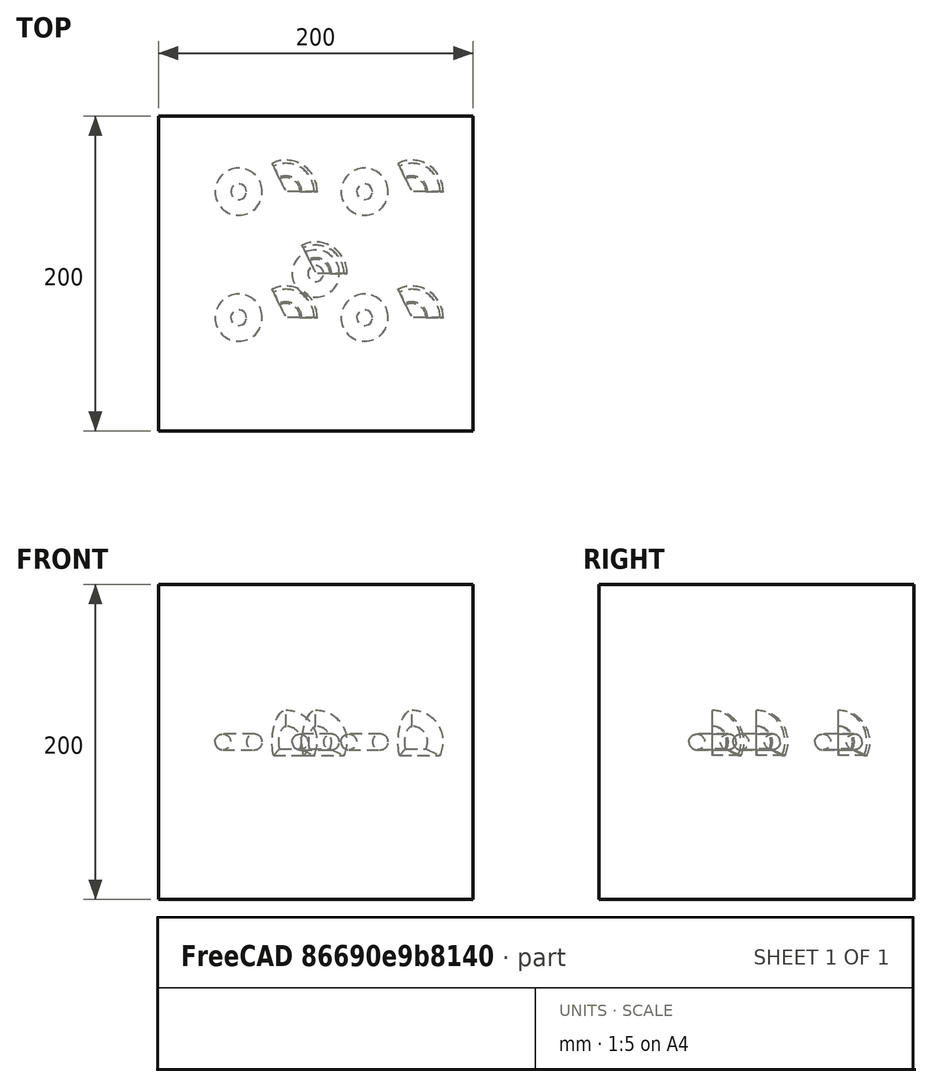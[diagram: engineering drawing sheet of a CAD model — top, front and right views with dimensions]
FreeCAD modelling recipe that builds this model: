
FCSTD DOCUMENT  (FreeCAD 0.19RUnknown)
Label: arrayTest-5
License: All rights reserved
LicenseURL: http://en.wikipedia.org/wiki/All_rights_reserved
objects: App::DocumentObjectGroupPython×1248, App::Part×5, Part::FeaturePython×4
note: 4 computed .brp shape members not serialized (recipe doc carries the construction recipe); baked Part::Feature solids carry a one-line shape summary decoded from their .brp

FEATURE [App::DocumentObjectGroupPython] HALFPI  # scripted group (container) (typed FeaturePython)
  name = HALFPI
  value = pi/2.
FEATURE [App::DocumentObjectGroupPython] PI  # scripted group (container) (typed FeaturePython)
  name = PI
  value = 1.*pi
FEATURE [App::DocumentObjectGroupPython] TWOPI  # scripted group (container) (typed FeaturePython)
  name = TWOPI
  value = 2.*pi
FEATURE [App::DocumentObjectGroupPython] Constants  # scripted group (container) (typed FeaturePython)
  Group = -> [HALFPI,PI,TWOPI]
FEATURE [App::DocumentObjectGroupPython] Variables  # scripted group (container) (typed FeaturePython)
FEATURE [App::DocumentObjectGroupPython] Quantities  # scripted group (container) (typed FeaturePython)
FEATURE [App::DocumentObjectGroupPython] Isotopes  # scripted group (container) (typed FeaturePython)
FEATURE [App::DocumentObjectGroupPython] Elements  # scripted group (container) (typed FeaturePython)
FEATURE [App::DocumentObjectGroupPython] G4Isotopes  # scripted group (container) (typed FeaturePython)
FEATURE [App::DocumentObjectGroupPython] H_element  # scripted group (container) (typed FeaturePython)
  Z = 1
  atom_value = 1.008
  formula = H
  name = H_element
FEATURE [App::DocumentObjectGroupPython] He_element  # scripted group (container) (typed FeaturePython)
  Z = 2
  atom_value = 4.0026
  formula = He
  name = He_element
FEATURE [App::DocumentObjectGroupPython] Li_element  # scripted group (container) (typed FeaturePython)
  Z = 3
  atom_value = 6.94
  formula = Li
  name = Li_element
FEATURE [App::DocumentObjectGroupPython] Be_element  # scripted group (container) (typed FeaturePython)
  Z = 4
  atom_value = 9.01218
  formula = Be
  name = Be_element
FEATURE [App::DocumentObjectGroupPython] B_element  # scripted group (container) (typed FeaturePython)
  Z = 5
  atom_value = 10.81
  formula = B
  name = B_element
FEATURE [App::DocumentObjectGroupPython] C_element  # scripted group (container) (typed FeaturePython)
  Z = 6
  atom_value = 12.011
  formula = C
  name = C_element
FEATURE [App::DocumentObjectGroupPython] N_element  # scripted group (container) (typed FeaturePython)
  Z = 7
  atom_value = 14.007
  formula = N
  name = N_element
FEATURE [App::DocumentObjectGroupPython] O_element  # scripted group (container) (typed FeaturePython)
  Z = 8
  atom_value = 15.999
  formula = O
  name = O_element
FEATURE [App::DocumentObjectGroupPython] F_element  # scripted group (container) (typed FeaturePython)
  Z = 9
  atom_value = 18.9984
  formula = F
  name = F_element
FEATURE [App::DocumentObjectGroupPython] Ne_element  # scripted group (container) (typed FeaturePython)
  Z = 10
  atom_value = 20.1797
  formula = Ne
  name = Ne_element
FEATURE [App::DocumentObjectGroupPython] Na_element  # scripted group (container) (typed FeaturePython)
  Z = 11
  atom_value = 22.9898
  formula = Na
  name = Na_element
FEATURE [App::DocumentObjectGroupPython] Mg_element  # scripted group (container) (typed FeaturePython)
  Z = 12
  atom_value = 24.305
  formula = Mg
  name = Mg_element
FEATURE [App::DocumentObjectGroupPython] Al_element  # scripted group (container) (typed FeaturePython)
  Z = 13
  atom_value = 26.9815
  formula = Al
  name = Al_element
FEATURE [App::DocumentObjectGroupPython] Si_element  # scripted group (container) (typed FeaturePython)
  Z = 14
  atom_value = 28.085
  formula = Si
  name = Si_element
FEATURE [App::DocumentObjectGroupPython] P_element  # scripted group (container) (typed FeaturePython)
  Z = 15
  atom_value = 30.9738
  formula = P
  name = P_element
FEATURE [App::DocumentObjectGroupPython] S_element  # scripted group (container) (typed FeaturePython)
  Z = 16
  atom_value = 32.06
  formula = S
  name = S_element
FEATURE [App::DocumentObjectGroupPython] Cl_element  # scripted group (container) (typed FeaturePython)
  Z = 17
  atom_value = 35.45
  formula = Cl
  name = Cl_element
FEATURE [App::DocumentObjectGroupPython] Ar_element  # scripted group (container) (typed FeaturePython)
  Z = 18
  atom_value = 39.95
  formula = Ar
  name = Ar_element
FEATURE [App::DocumentObjectGroupPython] K_element  # scripted group (container) (typed FeaturePython)
  Z = 19
  atom_value = 39.0983
  formula = K
  name = K_element
FEATURE [App::DocumentObjectGroupPython] Ca_element  # scripted group (container) (typed FeaturePython)
  Z = 20
  atom_value = 40.078
  formula = Ca
  name = Ca_element
FEATURE [App::DocumentObjectGroupPython] Sc_element  # scripted group (container) (typed FeaturePython)
  Z = 21
  atom_value = 44.9559
  formula = Sc
  name = Sc_element
FEATURE [App::DocumentObjectGroupPython] Ti_element  # scripted group (container) (typed FeaturePython)
  Z = 22
  atom_value = 47.867
  formula = Ti
  name = Ti_element
FEATURE [App::DocumentObjectGroupPython] V_element  # scripted group (container) (typed FeaturePython)
  Z = 23
  atom_value = 50.9415
  formula = V
  name = V_element
FEATURE [App::DocumentObjectGroupPython] Cr_element  # scripted group (container) (typed FeaturePython)
  Z = 24
  atom_value = 51.9961
  formula = Cr
  name = Cr_element
FEATURE [App::DocumentObjectGroupPython] Mn_element  # scripted group (container) (typed FeaturePython)
  Z = 25
  atom_value = 54.938
  formula = Mn
  name = Mn_element
FEATURE [App::DocumentObjectGroupPython] Fe_element  # scripted group (container) (typed FeaturePython)
  Z = 26
  atom_value = 55.845
  formula = Fe
  name = Fe_element
FEATURE [App::DocumentObjectGroupPython] Co_element  # scripted group (container) (typed FeaturePython)
  Z = 27
  atom_value = 58.9332
  formula = Co
  name = Co_element
FEATURE [App::DocumentObjectGroupPython] Ni_element  # scripted group (container) (typed FeaturePython)
  Z = 28
  atom_value = 58.6934
  formula = Ni
  name = Ni_element
FEATURE [App::DocumentObjectGroupPython] Cu_element  # scripted group (container) (typed FeaturePython)
  Z = 29
  atom_value = 63.546
  formula = Cu
  name = Cu_element
FEATURE [App::DocumentObjectGroupPython] Zn_element  # scripted group (container) (typed FeaturePython)
  Z = 30
  atom_value = 65.38
  formula = Zn
  name = Zn_element
FEATURE [App::DocumentObjectGroupPython] Ga_element  # scripted group (container) (typed FeaturePython)
  Z = 31
  atom_value = 69.723
  formula = Ga
  name = Ga_element
FEATURE [App::DocumentObjectGroupPython] Ge_element  # scripted group (container) (typed FeaturePython)
  Z = 32
  atom_value = 72.63
  formula = Ge
  name = Ge_element
FEATURE [App::DocumentObjectGroupPython] As_element  # scripted group (container) (typed FeaturePython)
  Z = 33
  atom_value = 74.9216
  formula = As
  name = As_element
FEATURE [App::DocumentObjectGroupPython] Se_element  # scripted group (container) (typed FeaturePython)
  Z = 34
  atom_value = 78.971
  formula = Se
  name = Se_element
FEATURE [App::DocumentObjectGroupPython] Br_element  # scripted group (container) (typed FeaturePython)
  Z = 35
  atom_value = 79.904
  formula = Br
  name = Br_element
FEATURE [App::DocumentObjectGroupPython] Kr_element  # scripted group (container) (typed FeaturePython)
  Z = 36
  atom_value = 83.798
  formula = Kr
  name = Kr_element
FEATURE [App::DocumentObjectGroupPython] Rb_element  # scripted group (container) (typed FeaturePython)
  Z = 37
  atom_value = 85.4678
  formula = Rb
  name = Rb_element
FEATURE [App::DocumentObjectGroupPython] Sr_element  # scripted group (container) (typed FeaturePython)
  Z = 38
  atom_value = 87.62
  formula = Sr
  name = Sr_element
FEATURE [App::DocumentObjectGroupPython] Y_element  # scripted group (container) (typed FeaturePython)
  Z = 39
  atom_value = 88.9058
  formula = Y
  name = Y_element
FEATURE [App::DocumentObjectGroupPython] Zr_element  # scripted group (container) (typed FeaturePython)
  Z = 40
  atom_value = 91.224
  formula = Zr
  name = Zr_element
FEATURE [App::DocumentObjectGroupPython] Nb_element  # scripted group (container) (typed FeaturePython)
  Z = 41
  atom_value = 92.9064
  formula = Nb
  name = Nb_element
FEATURE [App::DocumentObjectGroupPython] Mo_element  # scripted group (container) (typed FeaturePython)
  Z = 42
  atom_value = 95.95
  formula = Mo
  name = Mo_element
FEATURE [App::DocumentObjectGroupPython] Tc_element  # scripted group (container) (typed FeaturePython)
  Z = 43
  atom_value = 97
  formula = Tc
  name = Tc_element
FEATURE [App::DocumentObjectGroupPython] Ru_element  # scripted group (container) (typed FeaturePython)
  Z = 44
  atom_value = 101.07
  formula = Ru
  name = Ru_element
FEATURE [App::DocumentObjectGroupPython] Rh_element  # scripted group (container) (typed FeaturePython)
  Z = 45
  atom_value = 102.905
  formula = Rh
  name = Rh_element
FEATURE [App::DocumentObjectGroupPython] Pd_element  # scripted group (container) (typed FeaturePython)
  Z = 46
  atom_value = 106.42
  formula = Pd
  name = Pd_element
FEATURE [App::DocumentObjectGroupPython] Ag_element  # scripted group (container) (typed FeaturePython)
  Z = 47
  atom_value = 107.868
  formula = Ag
  name = Ag_element
FEATURE [App::DocumentObjectGroupPython] Cd_element  # scripted group (container) (typed FeaturePython)
  Z = 48
  atom_value = 112.414
  formula = Cd
  name = Cd_element
FEATURE [App::DocumentObjectGroupPython] In_element  # scripted group (container) (typed FeaturePython)
  Z = 49
  atom_value = 114.818
  formula = In
  name = In_element
FEATURE [App::DocumentObjectGroupPython] Sn_element  # scripted group (container) (typed FeaturePython)
  Z = 50
  atom_value = 118.71
  formula = Sn
  name = Sn_element
FEATURE [App::DocumentObjectGroupPython] Sb_element  # scripted group (container) (typed FeaturePython)
  Z = 51
  atom_value = 121.76
  formula = Sb
  name = Sb_element
FEATURE [App::DocumentObjectGroupPython] Te_element  # scripted group (container) (typed FeaturePython)
  Z = 52
  atom_value = 127.6
  formula = Te
  name = Te_element
FEATURE [App::DocumentObjectGroupPython] I_element  # scripted group (container) (typed FeaturePython)
  Z = 53
  atom_value = 126.904
  formula = I
  name = I_element
FEATURE [App::DocumentObjectGroupPython] Xe_element  # scripted group (container) (typed FeaturePython)
  Z = 54
  atom_value = 131.293
  formula = Xe
  name = Xe_element
FEATURE [App::DocumentObjectGroupPython] Cs_element  # scripted group (container) (typed FeaturePython)
  Z = 55
  atom_value = 132.905
  formula = Cs
  name = Cs_element
FEATURE [App::DocumentObjectGroupPython] Ba_element  # scripted group (container) (typed FeaturePython)
  Z = 56
  atom_value = 137.327
  formula = Ba
  name = Ba_element
FEATURE [App::DocumentObjectGroupPython] La_element  # scripted group (container) (typed FeaturePython)
  Z = 57
  atom_value = 138.905
  formula = La
  name = La_element
FEATURE [App::DocumentObjectGroupPython] Ce_element  # scripted group (container) (typed FeaturePython)
  Z = 58
  atom_value = 140.116
  formula = Ce
  name = Ce_element
FEATURE [App::DocumentObjectGroupPython] Pr_element  # scripted group (container) (typed FeaturePython)
  Z = 59
  atom_value = 140.908
  formula = Pr
  name = Pr_element
FEATURE [App::DocumentObjectGroupPython] Nd_element  # scripted group (container) (typed FeaturePython)
  Z = 60
  atom_value = 144.242
  formula = Nd
  name = Nd_element
FEATURE [App::DocumentObjectGroupPython] Pm_element  # scripted group (container) (typed FeaturePython)
  Z = 61
  atom_value = 145
  formula = Pm
  name = Pm_element
FEATURE [App::DocumentObjectGroupPython] Sm_element  # scripted group (container) (typed FeaturePython)
  Z = 62
  atom_value = 150.36
  formula = Sm
  name = Sm_element
FEATURE [App::DocumentObjectGroupPython] Eu_element  # scripted group (container) (typed FeaturePython)
  Z = 63
  atom_value = 151.964
  formula = Eu
  name = Eu_element
FEATURE [App::DocumentObjectGroupPython] Gd_element  # scripted group (container) (typed FeaturePython)
  Z = 64
  atom_value = 157.25
  formula = Gd
  name = Gd_element
FEATURE [App::DocumentObjectGroupPython] Tb_element  # scripted group (container) (typed FeaturePython)
  Z = 65
  atom_value = 158.925
  formula = Tb
  name = Tb_element
FEATURE [App::DocumentObjectGroupPython] Dy_element  # scripted group (container) (typed FeaturePython)
  Z = 66
  atom_value = 162.5
  formula = Dy
  name = Dy_element
FEATURE [App::DocumentObjectGroupPython] Ho_element  # scripted group (container) (typed FeaturePython)
  Z = 67
  atom_value = 164.93
  formula = Ho
  name = Ho_element
FEATURE [App::DocumentObjectGroupPython] Er_element  # scripted group (container) (typed FeaturePython)
  Z = 68
  atom_value = 167.259
  formula = Er
  name = Er_element
FEATURE [App::DocumentObjectGroupPython] Tm_element  # scripted group (container) (typed FeaturePython)
  Z = 69
  atom_value = 168.934
  formula = Tm
  name = Tm_element
FEATURE [App::DocumentObjectGroupPython] Yb_element  # scripted group (container) (typed FeaturePython)
  Z = 70
  atom_value = 173.045
  formula = Yb
  name = Yb_element
FEATURE [App::DocumentObjectGroupPython] Lu_element  # scripted group (container) (typed FeaturePython)
  Z = 71
  atom_value = 174.967
  formula = Lu
  name = Lu_element
FEATURE [App::DocumentObjectGroupPython] Hf_element  # scripted group (container) (typed FeaturePython)
  Z = 72
  atom_value = 178.49
  formula = Hf
  name = Hf_element
FEATURE [App::DocumentObjectGroupPython] Ta_element  # scripted group (container) (typed FeaturePython)
  Z = 73
  atom_value = 180.948
  formula = Ta
  name = Ta_element
FEATURE [App::DocumentObjectGroupPython] W_element  # scripted group (container) (typed FeaturePython)
  Z = 74
  atom_value = 183.84
  formula = W
  name = W_element
FEATURE [App::DocumentObjectGroupPython] Re_element  # scripted group (container) (typed FeaturePython)
  Z = 75
  atom_value = 186.207
  formula = Re
  name = Re_element
FEATURE [App::DocumentObjectGroupPython] Os_element  # scripted group (container) (typed FeaturePython)
  Z = 76
  atom_value = 190.23
  formula = Os
  name = Os_element
FEATURE [App::DocumentObjectGroupPython] Ir_element  # scripted group (container) (typed FeaturePython)
  Z = 77
  atom_value = 192.217
  formula = Ir
  name = Ir_element
FEATURE [App::DocumentObjectGroupPython] Pt_element  # scripted group (container) (typed FeaturePython)
  Z = 78
  atom_value = 195.084
  formula = Pt
  name = Pt_element
FEATURE [App::DocumentObjectGroupPython] Au_element  # scripted group (container) (typed FeaturePython)
  Z = 79
  atom_value = 196.967
  formula = Au
  name = Au_element
FEATURE [App::DocumentObjectGroupPython] Hg_element  # scripted group (container) (typed FeaturePython)
  Z = 80
  atom_value = 200.592
  formula = Hg
  name = Hg_element
FEATURE [App::DocumentObjectGroupPython] Tl_element  # scripted group (container) (typed FeaturePython)
  Z = 81
  atom_value = 204.38
  formula = Tl
  name = Tl_element
FEATURE [App::DocumentObjectGroupPython] Pb_element  # scripted group (container) (typed FeaturePython)
  Z = 82
  atom_value = 207.2
  formula = Pb
  name = Pb_element
FEATURE [App::DocumentObjectGroupPython] Bi_element  # scripted group (container) (typed FeaturePython)
  Z = 83
  atom_value = 208.98
  formula = Bi
  name = Bi_element
FEATURE [App::DocumentObjectGroupPython] Po_element  # scripted group (container) (typed FeaturePython)
  Z = 84
  atom_value = 209
  formula = Po
  name = Po_element
FEATURE [App::DocumentObjectGroupPython] At_element  # scripted group (container) (typed FeaturePython)
  Z = 85
  atom_value = 210
  formula = At
  name = At_element
FEATURE [App::DocumentObjectGroupPython] Rn_element  # scripted group (container) (typed FeaturePython)
  Z = 86
  atom_value = 222
  formula = Rn
  name = Rn_element
FEATURE [App::DocumentObjectGroupPython] Fr_element  # scripted group (container) (typed FeaturePython)
  Z = 87
  atom_value = 223
  formula = Fr
  name = Fr_element
FEATURE [App::DocumentObjectGroupPython] Ra_element  # scripted group (container) (typed FeaturePython)
  Z = 88
  atom_value = 226
  formula = Ra
  name = Ra_element
FEATURE [App::DocumentObjectGroupPython] Ac_element  # scripted group (container) (typed FeaturePython)
  Z = 89
  atom_value = 227
  formula = Ac
  name = Ac_element
FEATURE [App::DocumentObjectGroupPython] Th_element  # scripted group (container) (typed FeaturePython)
  Z = 90
  atom_value = 232.038
  formula = Th
  name = Th_element
FEATURE [App::DocumentObjectGroupPython] Pa_element  # scripted group (container) (typed FeaturePython)
  Z = 91
  atom_value = 231.036
  formula = Pa
  name = Pa_element
FEATURE [App::DocumentObjectGroupPython] U_element  # scripted group (container) (typed FeaturePython)
  Z = 92
  atom_value = 238.029
  formula = U
  name = U_element
FEATURE [App::DocumentObjectGroupPython] Np_element  # scripted group (container) (typed FeaturePython)
  Z = 93
  atom_value = 237
  formula = Np
  name = Np_element
FEATURE [App::DocumentObjectGroupPython] Pu_element  # scripted group (container) (typed FeaturePython)
  Z = 94
  atom_value = 244
  formula = Pu
  name = Pu_element
FEATURE [App::DocumentObjectGroupPython] Am_element  # scripted group (container) (typed FeaturePython)
  Z = 95
  atom_value = 243
  formula = Am
  name = Am_element
FEATURE [App::DocumentObjectGroupPython] Cm_element  # scripted group (container) (typed FeaturePython)
  Z = 96
  atom_value = 247
  formula = Cm
  name = Cm_element
FEATURE [App::DocumentObjectGroupPython] Bk_element  # scripted group (container) (typed FeaturePython)
  Z = 97
  atom_value = 247
  formula = Bk
  name = Bk_element
FEATURE [App::DocumentObjectGroupPython] Cf_element  # scripted group (container) (typed FeaturePython)
  Z = 98
  atom_value = 251
  formula = Cf
  name = Cf_element
FEATURE [App::DocumentObjectGroupPython] G4Elements  # scripted group (container) (typed FeaturePython)
  Group = -> [H_element,He_element,Li_element,Be_element,B_element,C_element,N_element,O_element,F_element,Ne_element,Na_element,Mg_element,Al_element,Si_element,P_element,S_element,Cl_element,Ar_element,K_element,Ca_element,Sc_element,Ti_element,V_element,Cr_element,Mn_element,Fe_element,Co_element,Ni_element,Cu_element,Zn_element,Ga_element,Ge_element,As_element,Se_element,Br_element,Kr_element,Rb_element,+61 more]
FEATURE [App::DocumentObjectGroupPython] H_element001  label="H_element : 0.101"  # scripted group (container) (typed FeaturePython)
  n = 0.101327
FEATURE [App::DocumentObjectGroupPython] C_element001  label="C_element : 0.775"  # scripted group (container) (typed FeaturePython)
  n = 0.7755
FEATURE [App::DocumentObjectGroupPython] N_element001  label="N_element : 0.035"  # scripted group (container) (typed FeaturePython)
  n = 0.035057
FEATURE [App::DocumentObjectGroupPython] O_element001  label="O_element : 0.052"  # scripted group (container) (typed FeaturePython)
  n = 0.0523159
FEATURE [App::DocumentObjectGroupPython] F_element001  label="F_element : 0.017"  # scripted group (container) (typed FeaturePython)
  n = 0.017422
FEATURE [App::DocumentObjectGroupPython] Ca_element001  label="Ca_element : 0.018"  # scripted group (container) (typed FeaturePython)
  n = 0.018378
FEATURE [App::DocumentObjectGroupPython] G4_A_150_TISSUE  label="G4_A-150_TISSUE"  # scripted group (container) (typed FeaturePython)
  Dunit = g/cm3
  Dvalue = 1.127
  Group = -> [H_element001,C_element001,N_element001,O_element001,F_element001,Ca_element001]
  conduct = 2
  density = 1
  expand = 3
  formula = G4_A-150_TISSUE
  name = G4_A-150_TISSUE
  specific = 4
FEATURE [App::DocumentObjectGroupPython] C_element002  label="C_element : 3"  # scripted group (container) (typed FeaturePython)
  n = 3
  ref = C_element
FEATURE [App::DocumentObjectGroupPython] H_element002  label="H_element : 6"  # scripted group (container) (typed FeaturePython)
  n = 6
  ref = H_element
FEATURE [App::DocumentObjectGroupPython] O_element002  label="O_element : 1"  # scripted group (container) (typed FeaturePython)
  n = 1
  ref = O_element
FEATURE [App::DocumentObjectGroupPython] G4_ACETONE  # scripted group (container) (typed FeaturePython)
  Dunit = g/cm3
  Dvalue = 0.7899
  Group = -> [C_element002,H_element002,O_element002]
  conduct = 2
  density = 1
  expand = 3
  formula = G4_ACETONE
  name = G4_ACETONE
  specific = 4
FEATURE [App::DocumentObjectGroupPython] C_element003  label="C_element : 2"  # scripted group (container) (typed FeaturePython)
  n = 2
  ref = C_element
FEATURE [App::DocumentObjectGroupPython] H_element003  label="H_element : 2"  # scripted group (container) (typed FeaturePython)
  n = 2
  ref = H_element
FEATURE [App::DocumentObjectGroupPython] G4_ACETYLENE  # scripted group (container) (typed FeaturePython)
  Dunit = g/cm3
  Dvalue = 0.0010967
  Group = -> [C_element003,H_element003]
  conduct = 2
  density = 1
  expand = 3
  formula = G4_ACETYLENE
  name = G4_ACETYLENE
  specific = 4
FEATURE [App::DocumentObjectGroupPython] C_element004  label="C_element : 5"  # scripted group (container) (typed FeaturePython)
  n = 5
  ref = C_element
FEATURE [App::DocumentObjectGroupPython] H_element004  label="H_element : 5"  # scripted group (container) (typed FeaturePython)
  n = 5
  ref = H_element
FEATURE [App::DocumentObjectGroupPython] N_element002  label="N_element : 5"  # scripted group (container) (typed FeaturePython)
  n = 5
  ref = N_element
FEATURE [App::DocumentObjectGroupPython] G4_ADENINE  # scripted group (container) (typed FeaturePython)
  Dunit = g/cm3
  Dvalue = 1.6
  Group = -> [C_element004,H_element004,N_element002]
  conduct = 2
  density = 1
  expand = 3
  formula = G4_ADENINE
  name = G4_ADENINE
  specific = 4
FEATURE [App::DocumentObjectGroupPython] H_element005  label="H_element : 0.114"  # scripted group (container) (typed FeaturePython)
  n = 0.114
FEATURE [App::DocumentObjectGroupPython] C_element005  label="C_element : 0.598"  # scripted group (container) (typed FeaturePython)
  n = 0.598
FEATURE [App::DocumentObjectGroupPython] N_element003  label="N_element : 0.007"  # scripted group (container) (typed FeaturePython)
  n = 0.007
FEATURE [App::DocumentObjectGroupPython] O_element003  label="O_element : 0.278"  # scripted group (container) (typed FeaturePython)
  n = 0.278
FEATURE [App::DocumentObjectGroupPython] Na_element001  label="Na_element : 0.001"  # scripted group (container) (typed FeaturePython)
  n = 0.001
FEATURE [App::DocumentObjectGroupPython] S_element001  label="S_element : 0.001"  # scripted group (container) (typed FeaturePython)
  n = 0.001
FEATURE [App::DocumentObjectGroupPython] Cl_element001  label="Cl_element : 0.001"  # scripted group (container) (typed FeaturePython)
  n = 0.001
FEATURE [App::DocumentObjectGroupPython] G4_ADIPOSE_TISSUE_ICRP  # scripted group (container) (typed FeaturePython)
  Dunit = g/cm3
  Dvalue = 0.95
  Group = -> [H_element005,C_element005,N_element003,O_element003,Na_element001,S_element001,Cl_element001]
  conduct = 2
  density = 1
  expand = 3
  formula = G4_ADIPOSE_TISSUE_ICRP
  name = G4_ADIPOSE_TISSUE_ICRP
  specific = 4
FEATURE [App::DocumentObjectGroupPython] C_element006  label="C_element : 0.000"  # scripted group (container) (typed FeaturePython)
  n = 0.000124
FEATURE [App::DocumentObjectGroupPython] N_element004  label="N_element : 0.755"  # scripted group (container) (typed FeaturePython)
  n = 0.755268
FEATURE [App::DocumentObjectGroupPython] O_element004  label="O_element : 0.232"  # scripted group (container) (typed FeaturePython)
  n = 0.231781
FEATURE [App::DocumentObjectGroupPython] Ar_element001  label="Ar_element : 0.013"  # scripted group (container) (typed FeaturePython)
  n = 0.012827
FEATURE [App::DocumentObjectGroupPython] G4_AIR  # scripted group (container) (typed FeaturePython)
  Dunit = g/cm3
  Dvalue = 0.00120479
  Group = -> [C_element006,N_element004,O_element004,Ar_element001]
  conduct = 2
  density = 1
  expand = 3
  formula = G4_AIR
  name = G4_AIR
  specific = 4
FEATURE [App::DocumentObjectGroupPython] C_element007  label="C_element : 006"  # scripted group (container) (typed FeaturePython)
  n = 3
  ref = C_element
FEATURE [App::DocumentObjectGroupPython] H_element006  label="H_element : 7"  # scripted group (container) (typed FeaturePython)
  n = 7
  ref = H_element
FEATURE [App::DocumentObjectGroupPython] N_element005  label="N_element : 1"  # scripted group (container) (typed FeaturePython)
  n = 1
  ref = N_element
FEATURE [App::DocumentObjectGroupPython] O_element005  label="O_element : 2"  # scripted group (container) (typed FeaturePython)
  n = 2
  ref = O_element
FEATURE [App::DocumentObjectGroupPython] G4_ALANINE  # scripted group (container) (typed FeaturePython)
  Dunit = g/cm3
  Dvalue = 1.42
  Group = -> [C_element007,H_element006,N_element005,O_element005]
  conduct = 2
  density = 1
  expand = 3
  formula = G4_ALANINE
  name = G4_ALANINE
  specific = 4
FEATURE [App::DocumentObjectGroupPython] Al_element001  label="Al_element : 2"  # scripted group (container) (typed FeaturePython)
  n = 2
  ref = Al_element
FEATURE [App::DocumentObjectGroupPython] O_element006  label="O_element : 3"  # scripted group (container) (typed FeaturePython)
  n = 3
  ref = O_element
FEATURE [App::DocumentObjectGroupPython] G4_ALUMINUM_OXIDE  # scripted group (container) (typed FeaturePython)
  Dunit = g/cm3
  Dvalue = 3.97
  Group = -> [Al_element001,O_element006]
  conduct = 2
  density = 1
  expand = 3
  formula = G4_ALUMINUM_OXIDE
  name = G4_ALUMINUM_OXIDE
  specific = 4
FEATURE [App::DocumentObjectGroupPython] H_element007  label="H_element : 0.106"  # scripted group (container) (typed FeaturePython)
  n = 0.10593
FEATURE [App::DocumentObjectGroupPython] C_element008  label="C_element : 0.789"  # scripted group (container) (typed FeaturePython)
  n = 0.788974
FEATURE [App::DocumentObjectGroupPython] O_element007  label="O_element : 0.105"  # scripted group (container) (typed FeaturePython)
  n = 0.105096
FEATURE [App::DocumentObjectGroupPython] G4_AMBER  # scripted group (container) (typed FeaturePython)
  Dunit = g/cm3
  Dvalue = 1.1
  Group = -> [H_element007,C_element008,O_element007]
  conduct = 2
  density = 1
  expand = 3
  formula = G4_AMBER
  name = G4_AMBER
  specific = 4
FEATURE [App::DocumentObjectGroupPython] N_element006  label="N_element : 006"  # scripted group (container) (typed FeaturePython)
  n = 1
  ref = N_element
FEATURE [App::DocumentObjectGroupPython] H_element008  label="H_element : 3"  # scripted group (container) (typed FeaturePython)
  n = 3
  ref = H_element
FEATURE [App::DocumentObjectGroupPython] G4_AMMONIA  # scripted group (container) (typed FeaturePython)
  Dunit = g/cm3
  Dvalue = 0.000826019
  Group = -> [N_element006,H_element008]
  conduct = 2
  density = 1
  expand = 3
  formula = G4_AMMONIA
  name = G4_AMMONIA
  specific = 4
FEATURE [App::DocumentObjectGroupPython] C_element009  label="C_element : 6"  # scripted group (container) (typed FeaturePython)
  n = 6
  ref = C_element
FEATURE [App::DocumentObjectGroupPython] H_element009  label="H_element : 008"  # scripted group (container) (typed FeaturePython)
  n = 7
  ref = H_element
FEATURE [App::DocumentObjectGroupPython] N_element007  label="N_element : 007"  # scripted group (container) (typed FeaturePython)
  n = 1
  ref = N_element
FEATURE [App::DocumentObjectGroupPython] G4_ANILINE  # scripted group (container) (typed FeaturePython)
  Dunit = g/cm3
  Dvalue = 1.0235
  Group = -> [C_element009,H_element009,N_element007]
  conduct = 2
  density = 1
  expand = 3
  formula = G4_ANILINE
  name = G4_ANILINE
  specific = 4
FEATURE [App::DocumentObjectGroupPython] C_element010  label="C_element : 14"  # scripted group (container) (typed FeaturePython)
  n = 14
  ref = C_element
FEATURE [App::DocumentObjectGroupPython] H_element010  label="H_element : 10"  # scripted group (container) (typed FeaturePython)
  n = 10
  ref = H_element
FEATURE [App::DocumentObjectGroupPython] G4_ANTHRACENE  # scripted group (container) (typed FeaturePython)
  Dunit = g/cm3
  Dvalue = 1.283
  Group = -> [C_element010,H_element010]
  conduct = 2
  density = 1
  expand = 3
  formula = G4_ANTHRACENE
  name = G4_ANTHRACENE
  specific = 4
FEATURE [App::DocumentObjectGroupPython] H_element011  label="H_element : 0.065"  # scripted group (container) (typed FeaturePython)
  n = 0.0654709
FEATURE [App::DocumentObjectGroupPython] C_element011  label="C_element : 0.537"  # scripted group (container) (typed FeaturePython)
  n = 0.536944
FEATURE [App::DocumentObjectGroupPython] N_element008  label="N_element : 0.021"  # scripted group (container) (typed FeaturePython)
  n = 0.0215
FEATURE [App::DocumentObjectGroupPython] O_element008  label="O_element : 0.032"  # scripted group (container) (typed FeaturePython)
  n = 0.032085
FEATURE [App::DocumentObjectGroupPython] F_element002  label="F_element : 0.167"  # scripted group (container) (typed FeaturePython)
  n = 0.167411
FEATURE [App::DocumentObjectGroupPython] Ca_element002  label="Ca_element : 0.177"  # scripted group (container) (typed FeaturePython)
  n = 0.176589
FEATURE [App::DocumentObjectGroupPython] G4_B_100_BONE  label="G4_B-100_BONE"  # scripted group (container) (typed FeaturePython)
  Dunit = g/cm3
  Dvalue = 1.45
  Group = -> [H_element011,C_element011,N_element008,O_element008,F_element002,Ca_element002]
  conduct = 2
  density = 1
  expand = 3
  formula = G4_B-100_BONE
  name = G4_B-100_BONE
  specific = 4
FEATURE [App::DocumentObjectGroupPython] H_element012  label="H_element : 0.057"  # scripted group (container) (typed FeaturePython)
  n = 0.057441
FEATURE [App::DocumentObjectGroupPython] C_element012  label="C_element : 0.790"  # scripted group (container) (typed FeaturePython)
  n = 0.774591
FEATURE [App::DocumentObjectGroupPython] O_element009  label="O_element : 0.168"  # scripted group (container) (typed FeaturePython)
  n = 0.167968
FEATURE [App::DocumentObjectGroupPython] G4_BAKELITE  # scripted group (container) (typed FeaturePython)
  Dunit = g/cm3
  Dvalue = 1.25
  Group = -> [H_element012,C_element012,O_element009]
  conduct = 2
  density = 1
  expand = 3
  formula = G4_BAKELITE
  name = G4_BAKELITE
  specific = 4
FEATURE [App::DocumentObjectGroupPython] Ba_element001  label="Ba_element : 1"  # scripted group (container) (typed FeaturePython)
  n = 1
  ref = Ba_element
FEATURE [App::DocumentObjectGroupPython] F_element003  label="F_element : 2"  # scripted group (container) (typed FeaturePython)
  n = 2
  ref = F_element
FEATURE [App::DocumentObjectGroupPython] G4_BARIUM_FLUORIDE  # scripted group (container) (typed FeaturePython)
  Dunit = g/cm3
  Dvalue = 4.89
  Group = -> [Ba_element001,F_element003]
  conduct = 2
  density = 1
  expand = 3
  formula = G4_BARIUM_FLUORIDE
  name = G4_BARIUM_FLUORIDE
  specific = 4
FEATURE [App::DocumentObjectGroupPython] Ba_element002  label="Ba_element : 002"  # scripted group (container) (typed FeaturePython)
  n = 1
  ref = Ba_element
FEATURE [App::DocumentObjectGroupPython] S_element002  label="S_element : 1"  # scripted group (container) (typed FeaturePython)
  n = 1
  ref = S_element
FEATURE [App::DocumentObjectGroupPython] O_element010  label="O_element : 4"  # scripted group (container) (typed FeaturePython)
  n = 4
  ref = O_element
FEATURE [App::DocumentObjectGroupPython] G4_BARIUM_SULFATE  # scripted group (container) (typed FeaturePython)
  Dunit = g/cm3
  Dvalue = 4.5
  Group = -> [Ba_element002,S_element002,O_element010]
  conduct = 2
  density = 1
  expand = 3
  formula = G4_BARIUM_SULFATE
  name = G4_BARIUM_SULFATE
  specific = 4
FEATURE [App::DocumentObjectGroupPython] C_element013  label="C_element : 007"  # scripted group (container) (typed FeaturePython)
  n = 6
  ref = C_element
FEATURE [App::DocumentObjectGroupPython] H_element013  label="H_element : 009"  # scripted group (container) (typed FeaturePython)
  n = 6
  ref = H_element
FEATURE [App::DocumentObjectGroupPython] G4_BENZENE  # scripted group (container) (typed FeaturePython)
  Dunit = g/cm3
  Dvalue = 0.87865
  Group = -> [C_element013,H_element013]
  conduct = 2
  density = 1
  expand = 3
  formula = G4_BENZENE
  name = G4_BENZENE
  specific = 4
FEATURE [App::DocumentObjectGroupPython] Be_element001  label="Be_element : 1"  # scripted group (container) (typed FeaturePython)
  n = 1
  ref = Be_element
FEATURE [App::DocumentObjectGroupPython] O_element011  label="O_element : 005"  # scripted group (container) (typed FeaturePython)
  n = 1
  ref = O_element
FEATURE [App::DocumentObjectGroupPython] G4_BERYLLIUM_OXIDE  # scripted group (container) (typed FeaturePython)
  Dunit = g/cm3
  Dvalue = 3.01
  Group = -> [Be_element001,O_element011]
  conduct = 2
  density = 1
  expand = 3
  formula = G4_BERYLLIUM_OXIDE
  name = G4_BERYLLIUM_OXIDE
  specific = 4
FEATURE [App::DocumentObjectGroupPython] Bi_element001  label="Bi_element : 4"  # scripted group (container) (typed FeaturePython)
  n = 4
  ref = Bi_element
FEATURE [App::DocumentObjectGroupPython] Ge_element001  label="Ge_element : 3"  # scripted group (container) (typed FeaturePython)
  n = 3
  ref = Ge_element
FEATURE [App::DocumentObjectGroupPython] O_element012  label="O_element : 12"  # scripted group (container) (typed FeaturePython)
  n = 12
  ref = O_element
FEATURE [App::DocumentObjectGroupPython] G4_BGO  # scripted group (container) (typed FeaturePython)
  Dunit = g/cm3
  Dvalue = 7.13
  Group = -> [Bi_element001,Ge_element001,O_element012]
  conduct = 2
  density = 1
  expand = 3
  formula = G4_BGO
  name = G4_BGO
  specific = 4
FEATURE [App::DocumentObjectGroupPython] H_element014  label="H_element : 0.102"  # scripted group (container) (typed FeaturePython)
  n = 0.102
FEATURE [App::DocumentObjectGroupPython] C_element014  label="C_element : 0.110"  # scripted group (container) (typed FeaturePython)
  n = 0.11
FEATURE [App::DocumentObjectGroupPython] N_element009  label="N_element : 0.033"  # scripted group (container) (typed FeaturePython)
  n = 0.033
FEATURE [App::DocumentObjectGroupPython] O_element013  label="O_element : 0.745"  # scripted group (container) (typed FeaturePython)
  n = 0.745
FEATURE [App::DocumentObjectGroupPython] Na_element002  label="Na_element : 0.002"  # scripted group (container) (typed FeaturePython)
  n = 0.001
FEATURE [App::DocumentObjectGroupPython] P_element001  label="P_element : 0.001"  # scripted group (container) (typed FeaturePython)
  n = 0.001
FEATURE [App::DocumentObjectGroupPython] S_element003  label="S_element : 0.002"  # scripted group (container) (typed FeaturePython)
  n = 0.002
FEATURE [App::DocumentObjectGroupPython] Cl_element002  label="Cl_element : 0.003"  # scripted group (container) (typed FeaturePython)
  n = 0.003
FEATURE [App::DocumentObjectGroupPython] K_element001  label="K_element : 0.002"  # scripted group (container) (typed FeaturePython)
  n = 0.002
FEATURE [App::DocumentObjectGroupPython] Fe_element001  label="Fe_element : 0.001"  # scripted group (container) (typed FeaturePython)
  n = 0.001
FEATURE [App::DocumentObjectGroupPython] G4_BLOOD_ICRP  # scripted group (container) (typed FeaturePython)
  Dunit = g/cm3
  Dvalue = 1.06
  Group = -> [H_element014,C_element014,N_element009,O_element013,Na_element002,P_element001,S_element003,Cl_element002,K_element001,Fe_element001]
  conduct = 2
  density = 1
  expand = 3
  formula = G4_BLOOD_ICRP
  name = G4_BLOOD_ICRP
  specific = 4
FEATURE [App::DocumentObjectGroupPython] H_element015  label="H_element : 0.064"  # scripted group (container) (typed FeaturePython)
  n = 0.064
FEATURE [App::DocumentObjectGroupPython] C_element015  label="C_element : 0.278"  # scripted group (container) (typed FeaturePython)
  n = 0.278
FEATURE [App::DocumentObjectGroupPython] N_element010  label="N_element : 0.027"  # scripted group (container) (typed FeaturePython)
  n = 0.027
FEATURE [App::DocumentObjectGroupPython] O_element014  label="O_element : 0.410"  # scripted group (container) (typed FeaturePython)
  n = 0.41
FEATURE [App::DocumentObjectGroupPython] Mg_element001  label="Mg_element : 0.002"  # scripted group (container) (typed FeaturePython)
  n = 0.002
FEATURE [App::DocumentObjectGroupPython] P_element002  label="P_element : 0.070"  # scripted group (container) (typed FeaturePython)
  n = 0.07
FEATURE [App::DocumentObjectGroupPython] S_element004  label="S_element : 0.003"  # scripted group (container) (typed FeaturePython)
  n = 0.002
FEATURE [App::DocumentObjectGroupPython] Ca_element003  label="Ca_element : 0.147"  # scripted group (container) (typed FeaturePython)
  n = 0.147
FEATURE [App::DocumentObjectGroupPython] G4_BONE_COMPACT_ICRU  # scripted group (container) (typed FeaturePython)
  Dunit = g/cm3
  Dvalue = 1.85
  Group = -> [H_element015,C_element015,N_element010,O_element014,Mg_element001,P_element002,S_element004,Ca_element003]
  conduct = 2
  density = 1
  expand = 3
  formula = G4_BONE_COMPACT_ICRU
  name = G4_BONE_COMPACT_ICRU
  specific = 4
FEATURE [App::DocumentObjectGroupPython] H_element016  label="H_element : 0.034"  # scripted group (container) (typed FeaturePython)
  n = 0.034
FEATURE [App::DocumentObjectGroupPython] C_element016  label="C_element : 0.155"  # scripted group (container) (typed FeaturePython)
  n = 0.155
FEATURE [App::DocumentObjectGroupPython] N_element011  label="N_element : 0.042"  # scripted group (container) (typed FeaturePython)
  n = 0.042
FEATURE [App::DocumentObjectGroupPython] O_element015  label="O_element : 0.435"  # scripted group (container) (typed FeaturePython)
  n = 0.435
FEATURE [App::DocumentObjectGroupPython] Na_element003  label="Na_element : 0.003"  # scripted group (container) (typed FeaturePython)
  n = 0.001
FEATURE [App::DocumentObjectGroupPython] Mg_element002  label="Mg_element : 0.003"  # scripted group (container) (typed FeaturePython)
  n = 0.002
FEATURE [App::DocumentObjectGroupPython] P_element003  label="P_element : 0.103"  # scripted group (container) (typed FeaturePython)
  n = 0.103
FEATURE [App::DocumentObjectGroupPython] S_element005  label="S_element : 0.004"  # scripted group (container) (typed FeaturePython)
  n = 0.003
FEATURE [App::DocumentObjectGroupPython] Ca_element004  label="Ca_element : 0.225"  # scripted group (container) (typed FeaturePython)
  n = 0.225
FEATURE [App::DocumentObjectGroupPython] G4_BONE_CORTICAL_ICRP  # scripted group (container) (typed FeaturePython)
  Dunit = g/cm3
  Dvalue = 1.92
  Group = -> [H_element016,C_element016,N_element011,O_element015,Na_element003,Mg_element002,P_element003,S_element005,Ca_element004]
  conduct = 2
  density = 1
  expand = 3
  formula = G4_BONE_CORTICAL_ICRP
  name = G4_BONE_CORTICAL_ICRP
  specific = 4
FEATURE [App::DocumentObjectGroupPython] B_element001  label="B_element : 4"  # scripted group (container) (typed FeaturePython)
  n = 4
  ref = B_element
FEATURE [App::DocumentObjectGroupPython] C_element017  label="C_element : 1"  # scripted group (container) (typed FeaturePython)
  n = 1
  ref = C_element
FEATURE [App::DocumentObjectGroupPython] G4_BORON_CARBIDE  # scripted group (container) (typed FeaturePython)
  Dunit = g/cm3
  Dvalue = 2.52
  Group = -> [B_element001,C_element017]
  conduct = 2
  density = 1
  expand = 3
  formula = G4_BORON_CARBIDE
  name = G4_BORON_CARBIDE
  specific = 4
FEATURE [App::DocumentObjectGroupPython] B_element002  label="B_element : 2"  # scripted group (container) (typed FeaturePython)
  n = 2
  ref = B_element
FEATURE [App::DocumentObjectGroupPython] O_element016  label="O_element : 006"  # scripted group (container) (typed FeaturePython)
  n = 3
  ref = O_element
FEATURE [App::DocumentObjectGroupPython] G4_BORON_OXIDE  # scripted group (container) (typed FeaturePython)
  Dunit = g/cm3
  Dvalue = 1.812
  Group = -> [B_element002,O_element016]
  conduct = 2
  density = 1
  expand = 3
  formula = G4_BORON_OXIDE
  name = G4_BORON_OXIDE
  specific = 4
FEATURE [App::DocumentObjectGroupPython] H_element017  label="H_element : 0.107"  # scripted group (container) (typed FeaturePython)
  n = 0.107
FEATURE [App::DocumentObjectGroupPython] C_element018  label="C_element : 0.145"  # scripted group (container) (typed FeaturePython)
  n = 0.145
FEATURE [App::DocumentObjectGroupPython] N_element012  label="N_element : 0.022"  # scripted group (container) (typed FeaturePython)
  n = 0.022
FEATURE [App::DocumentObjectGroupPython] O_element017  label="O_element : 0.712"  # scripted group (container) (typed FeaturePython)
  n = 0.712
FEATURE [App::DocumentObjectGroupPython] Na_element004  label="Na_element : 0.004"  # scripted group (container) (typed FeaturePython)
  n = 0.002
FEATURE [App::DocumentObjectGroupPython] P_element004  label="P_element : 0.004"  # scripted group (container) (typed FeaturePython)
  n = 0.004
FEATURE [App::DocumentObjectGroupPython] S_element006  label="S_element : 0.005"  # scripted group (container) (typed FeaturePython)
  n = 0.002
FEATURE [App::DocumentObjectGroupPython] Cl_element003  label="Cl_element : 0.004"  # scripted group (container) (typed FeaturePython)
  n = 0.003
FEATURE [App::DocumentObjectGroupPython] K_element002  label="K_element : 0.003"  # scripted group (container) (typed FeaturePython)
  n = 0.003
FEATURE [App::DocumentObjectGroupPython] G4_BRAIN_ICRP  # scripted group (container) (typed FeaturePython)
  Dunit = g/cm3
  Dvalue = 1.04
  Group = -> [H_element017,C_element018,N_element012,O_element017,Na_element004,P_element004,S_element006,Cl_element003,K_element002]
  conduct = 2
  density = 1
  expand = 3
  formula = G4_BRAIN_ICRP
  name = G4_BRAIN_ICRP
  specific = 4
FEATURE [App::DocumentObjectGroupPython] C_element019  label="C_element : 4"  # scripted group (container) (typed FeaturePython)
  n = 4
  ref = C_element
FEATURE [App::DocumentObjectGroupPython] H_element018  label="H_element : 010"  # scripted group (container) (typed FeaturePython)
  n = 10
  ref = H_element
FEATURE [App::DocumentObjectGroupPython] G4_BUTANE  # scripted group (container) (typed FeaturePython)
  Dunit = g/cm3
  Dvalue = 0.00249343
  Group = -> [C_element019,H_element018]
  conduct = 2
  density = 1
  expand = 3
  formula = G4_BUTANE
  name = G4_BUTANE
  specific = 4
FEATURE [App::DocumentObjectGroupPython] C_element020  label="C_element : 008"  # scripted group (container) (typed FeaturePython)
  n = 4
  ref = C_element
FEATURE [App::DocumentObjectGroupPython] H_element019  label="H_element : 011"  # scripted group (container) (typed FeaturePython)
  n = 10
  ref = H_element
FEATURE [App::DocumentObjectGroupPython] O_element018  label="O_element : 007"  # scripted group (container) (typed FeaturePython)
  n = 1
  ref = O_element
FEATURE [App::DocumentObjectGroupPython] G4_N_BUTYL_ALCOHOL  label="G4_N-BUTYL_ALCOHOL"  # scripted group (container) (typed FeaturePython)
  Dunit = g/cm3
  Dvalue = 0.8098
  Group = -> [C_element020,H_element019,O_element018]
  conduct = 2
  density = 1
  expand = 3
  formula = G4_N-BUTYL_ALCOHOL
  name = G4_N-BUTYL_ALCOHOL
  specific = 4
FEATURE [App::DocumentObjectGroupPython] H_element020  label="H_element : 0.025"  # scripted group (container) (typed FeaturePython)
  n = 0.02468
FEATURE [App::DocumentObjectGroupPython] C_element021  label="C_element : 0.502"  # scripted group (container) (typed FeaturePython)
  n = 0.501611
FEATURE [App::DocumentObjectGroupPython] O_element019  label="O_element : 0.005"  # scripted group (container) (typed FeaturePython)
  n = 0.004527
FEATURE [App::DocumentObjectGroupPython] F_element004  label="F_element : 0.465"  # scripted group (container) (typed FeaturePython)
  n = 0.465209
FEATURE [App::DocumentObjectGroupPython] Si_element001  label="Si_element : 0.004"  # scripted group (container) (typed FeaturePython)
  n = 0.003973
FEATURE [App::DocumentObjectGroupPython] G4_C_552  label="G4_C-552"  # scripted group (container) (typed FeaturePython)
  Dunit = g/cm3
  Dvalue = 1.76
  Group = -> [H_element020,C_element021,O_element019,F_element004,Si_element001]
  conduct = 2
  density = 1
  expand = 3
  formula = G4_C-552
  name = G4_C-552
  specific = 4
FEATURE [App::DocumentObjectGroupPython] Cd_element001  label="Cd_element : 1"  # scripted group (container) (typed FeaturePython)
  n = 1
  ref = Cd_element
FEATURE [App::DocumentObjectGroupPython] Te_element001  label="Te_element : 1"  # scripted group (container) (typed FeaturePython)
  n = 1
  ref = Te_element
FEATURE [App::DocumentObjectGroupPython] G4_CADMIUM_TELLURIDE  # scripted group (container) (typed FeaturePython)
  Dunit = g/cm3
  Dvalue = 6.2
  Group = -> [Cd_element001,Te_element001]
  conduct = 2
  density = 1
  expand = 3
  formula = G4_CADMIUM_TELLURIDE
  name = G4_CADMIUM_TELLURIDE
  specific = 4
FEATURE [App::DocumentObjectGroupPython] Cd_element002  label="Cd_element : 002"  # scripted group (container) (typed FeaturePython)
  n = 1
  ref = Cd_element
FEATURE [App::DocumentObjectGroupPython] W_element001  label="W_element : 1"  # scripted group (container) (typed FeaturePython)
  n = 1
  ref = W_element
FEATURE [App::DocumentObjectGroupPython] O_element020  label="O_element : 008"  # scripted group (container) (typed FeaturePython)
  n = 4
  ref = O_element
FEATURE [App::DocumentObjectGroupPython] G4_CADMIUM_TUNGSTATE  # scripted group (container) (typed FeaturePython)
  Dunit = g/cm3
  Dvalue = 7.9
  Group = -> [Cd_element002,W_element001,O_element020]
  conduct = 2
  density = 1
  expand = 3
  formula = G4_CADMIUM_TUNGSTATE
  name = G4_CADMIUM_TUNGSTATE
  specific = 4
FEATURE [App::DocumentObjectGroupPython] Ca_element005  label="Ca_element : 1"  # scripted group (container) (typed FeaturePython)
  n = 1
  ref = Ca_element
FEATURE [App::DocumentObjectGroupPython] C_element022  label="C_element : 009"  # scripted group (container) (typed FeaturePython)
  n = 1
  ref = C_element
FEATURE [App::DocumentObjectGroupPython] O_element021  label="O_element : 009"  # scripted group (container) (typed FeaturePython)
  n = 3
  ref = O_element
FEATURE [App::DocumentObjectGroupPython] G4_CALCIUM_CARBONATE  # scripted group (container) (typed FeaturePython)
  Dunit = g/cm3
  Dvalue = 2.8
  Group = -> [Ca_element005,C_element022,O_element021]
  conduct = 2
  density = 1
  expand = 3
  formula = G4_CALCIUM_CARBONATE
  name = G4_CALCIUM_CARBONATE
  specific = 4
FEATURE [App::DocumentObjectGroupPython] Ca_element006  label="Ca_element : 002"  # scripted group (container) (typed FeaturePython)
  n = 1
  ref = Ca_element
FEATURE [App::DocumentObjectGroupPython] F_element005  label="F_element : 003"  # scripted group (container) (typed FeaturePython)
  n = 2
  ref = F_element
FEATURE [App::DocumentObjectGroupPython] G4_CALCIUM_FLUORIDE  # scripted group (container) (typed FeaturePython)
  Dunit = g/cm3
  Dvalue = 3.18
  Group = -> [Ca_element006,F_element005]
  conduct = 2
  density = 1
  expand = 3
  formula = G4_CALCIUM_FLUORIDE
  name = G4_CALCIUM_FLUORIDE
  specific = 4
FEATURE [App::DocumentObjectGroupPython] Ca_element007  label="Ca_element : 003"  # scripted group (container) (typed FeaturePython)
  n = 1
  ref = Ca_element
FEATURE [App::DocumentObjectGroupPython] O_element022  label="O_element : 010"  # scripted group (container) (typed FeaturePython)
  n = 1
  ref = O_element
FEATURE [App::DocumentObjectGroupPython] G4_CALCIUM_OXIDE  # scripted group (container) (typed FeaturePython)
  Dunit = g/cm3
  Dvalue = 3.3
  Group = -> [Ca_element007,O_element022]
  conduct = 2
  density = 1
  expand = 3
  formula = G4_CALCIUM_OXIDE
  name = G4_CALCIUM_OXIDE
  specific = 4
FEATURE [App::DocumentObjectGroupPython] Ca_element008  label="Ca_element : 004"  # scripted group (container) (typed FeaturePython)
  n = 1
  ref = Ca_element
FEATURE [App::DocumentObjectGroupPython] S_element007  label="S_element : 002"  # scripted group (container) (typed FeaturePython)
  n = 1
  ref = S_element
FEATURE [App::DocumentObjectGroupPython] O_element023  label="O_element : 011"  # scripted group (container) (typed FeaturePython)
  n = 4
  ref = O_element
FEATURE [App::DocumentObjectGroupPython] G4_CALCIUM_SULFATE  # scripted group (container) (typed FeaturePython)
  Dunit = g/cm3
  Dvalue = 2.96
  Group = -> [Ca_element008,S_element007,O_element023]
  conduct = 2
  density = 1
  expand = 3
  formula = G4_CALCIUM_SULFATE
  name = G4_CALCIUM_SULFATE
  specific = 4
FEATURE [App::DocumentObjectGroupPython] Ca_element009  label="Ca_element : 005"  # scripted group (container) (typed FeaturePython)
  n = 1
  ref = Ca_element
FEATURE [App::DocumentObjectGroupPython] W_element002  label="W_element : 002"  # scripted group (container) (typed FeaturePython)
  n = 1
  ref = W_element
FEATURE [App::DocumentObjectGroupPython] O_element024  label="O_element : 012"  # scripted group (container) (typed FeaturePython)
  n = 4
  ref = O_element
FEATURE [App::DocumentObjectGroupPython] G4_CALCIUM_TUNGSTATE  # scripted group (container) (typed FeaturePython)
  Dunit = g/cm3
  Dvalue = 6.062
  Group = -> [Ca_element009,W_element002,O_element024]
  conduct = 2
  density = 1
  expand = 3
  formula = G4_CALCIUM_TUNGSTATE
  name = G4_CALCIUM_TUNGSTATE
  specific = 4
FEATURE [App::DocumentObjectGroupPython] C_element023  label="C_element : 010"  # scripted group (container) (typed FeaturePython)
  n = 1
  ref = C_element
FEATURE [App::DocumentObjectGroupPython] O_element025  label="O_element : 013"  # scripted group (container) (typed FeaturePython)
  n = 2
  ref = O_element
FEATURE [App::DocumentObjectGroupPython] G4_CARBON_DIOXIDE  # scripted group (container) (typed FeaturePython)
  Dunit = g/cm3
  Dvalue = 0.00184212
  Group = -> [C_element023,O_element025]
  conduct = 2
  density = 1
  expand = 3
  formula = G4_CARBON_DIOXIDE
  name = G4_CARBON_DIOXIDE
  specific = 4
FEATURE [App::DocumentObjectGroupPython] C_element024  label="C_element : 011"  # scripted group (container) (typed FeaturePython)
  n = 1
  ref = C_element
FEATURE [App::DocumentObjectGroupPython] Cl_element004  label="Cl_element : 4"  # scripted group (container) (typed FeaturePython)
  n = 4
  ref = Cl_element
FEATURE [App::DocumentObjectGroupPython] G4_CARBON_TETRACHLORIDE  # scripted group (container) (typed FeaturePython)
  Dunit = g/cm3
  Dvalue = 1.594
  Group = -> [C_element024,Cl_element004]
  conduct = 2
  density = 1
  expand = 3
  formula = G4_CARBON_TETRACHLORIDE
  name = G4_CARBON_TETRACHLORIDE
  specific = 4
FEATURE [App::DocumentObjectGroupPython] C_element025  label="C_element : 012"  # scripted group (container) (typed FeaturePython)
  n = 6
  ref = C_element
FEATURE [App::DocumentObjectGroupPython] H_element021  label="H_element : 012"  # scripted group (container) (typed FeaturePython)
  n = 10
  ref = H_element
FEATURE [App::DocumentObjectGroupPython] O_element026  label="O_element : 5"  # scripted group (container) (typed FeaturePython)
  n = 5
  ref = O_element
FEATURE [App::DocumentObjectGroupPython] G4_CELLULOSE_CELLOPHANE  # scripted group (container) (typed FeaturePython)
  Dunit = g/cm3
  Dvalue = 1.42
  Group = -> [C_element025,H_element021,O_element026]
  conduct = 2
  density = 1
  expand = 3
  formula = G4_CELLULOSE_CELLOPHANE
  name = G4_CELLULOSE_CELLOPHANE
  specific = 4
FEATURE [App::DocumentObjectGroupPython] H_element022  label="H_element : 0.067"  # scripted group (container) (typed FeaturePython)
  n = 0.067125
FEATURE [App::DocumentObjectGroupPython] C_element026  label="C_element : 0.545"  # scripted group (container) (typed FeaturePython)
  n = 0.545403
FEATURE [App::DocumentObjectGroupPython] O_element027  label="O_element : 0.387"  # scripted group (container) (typed FeaturePython)
  n = 0.387472
FEATURE [App::DocumentObjectGroupPython] G4_CELLULOSE_BUTYRATE  # scripted group (container) (typed FeaturePython)
  Dunit = g/cm3
  Dvalue = 1.2
  Group = -> [H_element022,C_element026,O_element027]
  conduct = 2
  density = 1
  expand = 3
  formula = G4_CELLULOSE_BUTYRATE
  name = G4_CELLULOSE_BUTYRATE
  specific = 4
FEATURE [App::DocumentObjectGroupPython] H_element023  label="H_element : 0.029"  # scripted group (container) (typed FeaturePython)
  n = 0.029216
FEATURE [App::DocumentObjectGroupPython] C_element027  label="C_element : 0.271"  # scripted group (container) (typed FeaturePython)
  n = 0.271296
FEATURE [App::DocumentObjectGroupPython] N_element013  label="N_element : 0.121"  # scripted group (container) (typed FeaturePython)
  n = 0.121276
FEATURE [App::DocumentObjectGroupPython] O_element028  label="O_element : 0.578"  # scripted group (container) (typed FeaturePython)
  n = 0.578212
FEATURE [App::DocumentObjectGroupPython] G4_CELLULOSE_NITRATE  # scripted group (container) (typed FeaturePython)
  Dunit = g/cm3
  Dvalue = 1.49
  Group = -> [H_element023,C_element027,N_element013,O_element028]
  conduct = 2
  density = 1
  expand = 3
  formula = G4_CELLULOSE_NITRATE
  name = G4_CELLULOSE_NITRATE
  specific = 4
FEATURE [App::DocumentObjectGroupPython] H_element024  label="H_element : 0.108"  # scripted group (container) (typed FeaturePython)
  n = 0.107596
FEATURE [App::DocumentObjectGroupPython] N_element014  label="N_element : 0.001"  # scripted group (container) (typed FeaturePython)
  n = 0.0008
FEATURE [App::DocumentObjectGroupPython] O_element029  label="O_element : 0.875"  # scripted group (container) (typed FeaturePython)
  n = 0.874976
FEATURE [App::DocumentObjectGroupPython] S_element008  label="S_element : 0.015"  # scripted group (container) (typed FeaturePython)
  n = 0.014627
FEATURE [App::DocumentObjectGroupPython] Ce_element001  label="Ce_element : 0.002"  # scripted group (container) (typed FeaturePython)
  n = 0.002001
FEATURE [App::DocumentObjectGroupPython] G4_CERIC_SULFATE  # scripted group (container) (typed FeaturePython)
  Dunit = g/cm3
  Dvalue = 1.03
  Group = -> [H_element024,N_element014,O_element029,S_element008,Ce_element001]
  conduct = 2
  density = 1
  expand = 3
  formula = G4_CERIC_SULFATE
  name = G4_CERIC_SULFATE
  specific = 4
FEATURE [App::DocumentObjectGroupPython] Cs_element001  label="Cs_element : 1"  # scripted group (container) (typed FeaturePython)
  n = 1
  ref = Cs_element
FEATURE [App::DocumentObjectGroupPython] F_element006  label="F_element : 1"  # scripted group (container) (typed FeaturePython)
  n = 1
  ref = F_element
FEATURE [App::DocumentObjectGroupPython] G4_CESIUM_FLUORIDE  # scripted group (container) (typed FeaturePython)
  Dunit = g/cm3
  Dvalue = 4.115
  Group = -> [Cs_element001,F_element006]
  conduct = 2
  density = 1
  expand = 3
  formula = G4_CESIUM_FLUORIDE
  name = G4_CESIUM_FLUORIDE
  specific = 4
FEATURE [App::DocumentObjectGroupPython] Cs_element002  label="Cs_element : 002"  # scripted group (container) (typed FeaturePython)
  n = 1
  ref = Cs_element
FEATURE [App::DocumentObjectGroupPython] I_element001  label="I_element : 1"  # scripted group (container) (typed FeaturePython)
  n = 1
  ref = I_element
FEATURE [App::DocumentObjectGroupPython] G4_CESIUM_IODIDE  # scripted group (container) (typed FeaturePython)
  Dunit = g/cm3
  Dvalue = 4.51
  Group = -> [Cs_element002,I_element001]
  conduct = 2
  density = 1
  expand = 3
  formula = G4_CESIUM_IODIDE
  name = G4_CESIUM_IODIDE
  specific = 4
FEATURE [App::DocumentObjectGroupPython] C_element028  label="C_element : 013"  # scripted group (container) (typed FeaturePython)
  n = 6
  ref = C_element
FEATURE [App::DocumentObjectGroupPython] H_element025  label="H_element : 013"  # scripted group (container) (typed FeaturePython)
  n = 5
  ref = H_element
FEATURE [App::DocumentObjectGroupPython] Cl_element005  label="Cl_element : 1"  # scripted group (container) (typed FeaturePython)
  n = 1
  ref = Cl_element
FEATURE [App::DocumentObjectGroupPython] G4_CHLOROBENZENE  # scripted group (container) (typed FeaturePython)
  Dunit = g/cm3
  Dvalue = 1.1058
  Group = -> [C_element028,H_element025,Cl_element005]
  conduct = 2
  density = 1
  expand = 3
  formula = G4_CHLOROBENZENE
  name = G4_CHLOROBENZENE
  specific = 4
FEATURE [App::DocumentObjectGroupPython] C_element029  label="C_element : 014"  # scripted group (container) (typed FeaturePython)
  n = 1
  ref = C_element
FEATURE [App::DocumentObjectGroupPython] H_element026  label="H_element : 1"  # scripted group (container) (typed FeaturePython)
  n = 1
  ref = H_element
FEATURE [App::DocumentObjectGroupPython] Cl_element006  label="Cl_element : 3"  # scripted group (container) (typed FeaturePython)
  n = 3
  ref = Cl_element
FEATURE [App::DocumentObjectGroupPython] G4_CHLOROFORM  # scripted group (container) (typed FeaturePython)
  Dunit = g/cm3
  Dvalue = 1.4832
  Group = -> [C_element029,H_element026,Cl_element006]
  conduct = 2
  density = 1
  expand = 3
  formula = G4_CHLOROFORM
  name = G4_CHLOROFORM
  specific = 4
FEATURE [App::DocumentObjectGroupPython] H_element027  label="H_element : 0.010"  # scripted group (container) (typed FeaturePython)
  n = 0.01
FEATURE [App::DocumentObjectGroupPython] C_element030  label="C_element : 0.001"  # scripted group (container) (typed FeaturePython)
  n = 0.001
FEATURE [App::DocumentObjectGroupPython] O_element030  label="O_element : 0.529"  # scripted group (container) (typed FeaturePython)
  n = 0.529107
FEATURE [App::DocumentObjectGroupPython] Na_element005  label="Na_element : 0.016"  # scripted group (container) (typed FeaturePython)
  n = 0.016
FEATURE [App::DocumentObjectGroupPython] Mg_element003  label="Mg_element : 0.004"  # scripted group (container) (typed FeaturePython)
  n = 0.002
FEATURE [App::DocumentObjectGroupPython] Al_element002  label="Al_element : 0.034"  # scripted group (container) (typed FeaturePython)
  n = 0.033872
FEATURE [App::DocumentObjectGroupPython] Si_element002  label="Si_element : 0.337"  # scripted group (container) (typed FeaturePython)
  n = 0.337021
FEATURE [App::DocumentObjectGroupPython] K_element003  label="K_element : 0.013"  # scripted group (container) (typed FeaturePython)
  n = 0.013
FEATURE [App::DocumentObjectGroupPython] Ca_element010  label="Ca_element : 0.044"  # scripted group (container) (typed FeaturePython)
  n = 0.044
FEATURE [App::DocumentObjectGroupPython] Fe_element002  label="Fe_element : 0.014"  # scripted group (container) (typed FeaturePython)
  n = 0.014
FEATURE [App::DocumentObjectGroupPython] G4_CONCRETE  # scripted group (container) (typed FeaturePython)
  Dunit = g/cm3
  Dvalue = 2.3
  Group = -> [H_element027,C_element030,O_element030,Na_element005,Mg_element003,Al_element002,Si_element002,K_element003,Ca_element010,Fe_element002]
  conduct = 2
  density = 1
  expand = 3
  formula = G4_CONCRETE
  name = G4_CONCRETE
  specific = 4
FEATURE [App::DocumentObjectGroupPython] C_element031  label="C_element : 015"  # scripted group (container) (typed FeaturePython)
  n = 6
  ref = C_element
FEATURE [App::DocumentObjectGroupPython] H_element028  label="H_element : 12"  # scripted group (container) (typed FeaturePython)
  n = 12
  ref = H_element
FEATURE [App::DocumentObjectGroupPython] G4_CYCLOHEXANE  # scripted group (container) (typed FeaturePython)
  Dunit = g/cm3
  Dvalue = 0.779
  Group = -> [C_element031,H_element028]
  conduct = 2
  density = 1
  expand = 3
  formula = G4_CYCLOHEXANE
  name = G4_CYCLOHEXANE
  specific = 4
FEATURE [App::DocumentObjectGroupPython] C_element032  label="C_element : 016"  # scripted group (container) (typed FeaturePython)
  n = 6
  ref = C_element
FEATURE [App::DocumentObjectGroupPython] H_element029  label="H_element : 4"  # scripted group (container) (typed FeaturePython)
  n = 4
  ref = H_element
FEATURE [App::DocumentObjectGroupPython] Cl_element007  label="Cl_element : 2"  # scripted group (container) (typed FeaturePython)
  n = 2
  ref = Cl_element
FEATURE [App::DocumentObjectGroupPython] G4_1_2_DICHLOROBENZENE  label="G4_1.2-DICHLOROBENZENE"  # scripted group (container) (typed FeaturePython)
  Dunit = g/cm3
  Dvalue = 1.3048
  Group = -> [C_element032,H_element029,Cl_element007]
  conduct = 2
  density = 1
  expand = 3
  formula = G4_1.2-DICHLOROBENZENE
  name = G4_1.2-DICHLOROBENZENE
  specific = 4
FEATURE [App::DocumentObjectGroupPython] C_element033  label="C_element : 017"  # scripted group (container) (typed FeaturePython)
  n = 4
  ref = C_element
FEATURE [App::DocumentObjectGroupPython] H_element030  label="H_element : 8"  # scripted group (container) (typed FeaturePython)
  n = 8
  ref = H_element
FEATURE [App::DocumentObjectGroupPython] O_element031  label="O_element : 014"  # scripted group (container) (typed FeaturePython)
  n = 1
  ref = O_element
FEATURE [App::DocumentObjectGroupPython] Cl_element008  label="Cl_element : 005"  # scripted group (container) (typed FeaturePython)
  n = 2
  ref = Cl_element
FEATURE [App::DocumentObjectGroupPython] G4_DICHLORODIETHYL_ETHER  # scripted group (container) (typed FeaturePython)
  Dunit = g/cm3
  Dvalue = 1.2199
  Group = -> [C_element033,H_element030,O_element031,Cl_element008]
  conduct = 2
  density = 1
  expand = 3
  formula = G4_DICHLORODIETHYL_ETHER
  name = G4_DICHLORODIETHYL_ETHER
  specific = 4
FEATURE [App::DocumentObjectGroupPython] C_element034  label="C_element : 018"  # scripted group (container) (typed FeaturePython)
  n = 2
  ref = C_element
FEATURE [App::DocumentObjectGroupPython] H_element031  label="H_element : 014"  # scripted group (container) (typed FeaturePython)
  n = 4
  ref = H_element
FEATURE [App::DocumentObjectGroupPython] Cl_element009  label="Cl_element : 006"  # scripted group (container) (typed FeaturePython)
  n = 2
  ref = Cl_element
FEATURE [App::DocumentObjectGroupPython] G4_1_2_DICHLOROETHANE  label="G4_1.2-DICHLOROETHANE"  # scripted group (container) (typed FeaturePython)
  Dunit = g/cm3
  Dvalue = 1.2351
  Group = -> [C_element034,H_element031,Cl_element009]
  conduct = 2
  density = 1
  expand = 3
  formula = G4_1.2-DICHLOROETHANE
  name = G4_1.2-DICHLOROETHANE
  specific = 4
FEATURE [App::DocumentObjectGroupPython] C_element035  label="C_element : 019"  # scripted group (container) (typed FeaturePython)
  n = 4
  ref = C_element
FEATURE [App::DocumentObjectGroupPython] H_element032  label="H_element : 015"  # scripted group (container) (typed FeaturePython)
  n = 10
  ref = H_element
FEATURE [App::DocumentObjectGroupPython] O_element032  label="O_element : 015"  # scripted group (container) (typed FeaturePython)
  n = 1
  ref = O_element
FEATURE [App::DocumentObjectGroupPython] G4_DIETHYL_ETHER  # scripted group (container) (typed FeaturePython)
  Dunit = g/cm3
  Dvalue = 0.71378
  Group = -> [C_element035,H_element032,O_element032]
  conduct = 2
  density = 1
  expand = 3
  formula = G4_DIETHYL_ETHER
  name = G4_DIETHYL_ETHER
  specific = 4
FEATURE [App::DocumentObjectGroupPython] C_element036  label="C_element : 020"  # scripted group (container) (typed FeaturePython)
  n = 3
  ref = C_element
FEATURE [App::DocumentObjectGroupPython] H_element033  label="H_element : 016"  # scripted group (container) (typed FeaturePython)
  n = 7
  ref = H_element
FEATURE [App::DocumentObjectGroupPython] N_element015  label="N_element : 008"  # scripted group (container) (typed FeaturePython)
  n = 1
  ref = N_element
FEATURE [App::DocumentObjectGroupPython] O_element033  label="O_element : 016"  # scripted group (container) (typed FeaturePython)
  n = 1
  ref = O_element
FEATURE [App::DocumentObjectGroupPython] G4_N_N_DIMETHYL_FORMAMIDE  label="G4_N.N-DIMETHYL_FORMAMIDE"  # scripted group (container) (typed FeaturePython)
  Dunit = g/cm3
  Dvalue = 0.9487
  Group = -> [C_element036,H_element033,N_element015,O_element033]
  conduct = 2
  density = 1
  expand = 3
  formula = G4_N.N-DIMETHYL_FORMAMIDE
  name = G4_N.N-DIMETHYL_FORMAMIDE
  specific = 4
FEATURE [App::DocumentObjectGroupPython] C_element037  label="C_element : 021"  # scripted group (container) (typed FeaturePython)
  n = 2
  ref = C_element
FEATURE [App::DocumentObjectGroupPython] H_element034  label="H_element : 017"  # scripted group (container) (typed FeaturePython)
  n = 6
  ref = H_element
FEATURE [App::DocumentObjectGroupPython] O_element034  label="O_element : 017"  # scripted group (container) (typed FeaturePython)
  n = 1
  ref = O_element
FEATURE [App::DocumentObjectGroupPython] S_element009  label="S_element : 003"  # scripted group (container) (typed FeaturePython)
  n = 1
  ref = S_element
FEATURE [App::DocumentObjectGroupPython] G4_DIMETHYL_SULFOXIDE  # scripted group (container) (typed FeaturePython)
  Dunit = g/cm3
  Dvalue = 1.1014
  Group = -> [C_element037,H_element034,O_element034,S_element009]
  conduct = 2
  density = 1
  expand = 3
  formula = G4_DIMETHYL_SULFOXIDE
  name = G4_DIMETHYL_SULFOXIDE
  specific = 4
FEATURE [App::DocumentObjectGroupPython] C_element038  label="C_element : 022"  # scripted group (container) (typed FeaturePython)
  n = 2
  ref = C_element
FEATURE [App::DocumentObjectGroupPython] H_element035  label="H_element : 018"  # scripted group (container) (typed FeaturePython)
  n = 6
  ref = H_element
FEATURE [App::DocumentObjectGroupPython] G4_ETHANE  # scripted group (container) (typed FeaturePython)
  Dunit = g/cm3
  Dvalue = 0.00125324
  Group = -> [C_element038,H_element035]
  conduct = 2
  density = 1
  expand = 3
  formula = G4_ETHANE
  name = G4_ETHANE
  specific = 4
FEATURE [App::DocumentObjectGroupPython] C_element039  label="C_element : 023"  # scripted group (container) (typed FeaturePython)
  n = 2
  ref = C_element
FEATURE [App::DocumentObjectGroupPython] H_element036  label="H_element : 019"  # scripted group (container) (typed FeaturePython)
  n = 6
  ref = H_element
FEATURE [App::DocumentObjectGroupPython] O_element035  label="O_element : 018"  # scripted group (container) (typed FeaturePython)
  n = 1
  ref = O_element
FEATURE [App::DocumentObjectGroupPython] G4_ETHYL_ALCOHOL  # scripted group (container) (typed FeaturePython)
  Dunit = g/cm3
  Dvalue = 0.7893
  Group = -> [C_element039,H_element036,O_element035]
  conduct = 2
  density = 1
  expand = 3
  formula = G4_ETHYL_ALCOHOL
  name = G4_ETHYL_ALCOHOL
  specific = 4
FEATURE [App::DocumentObjectGroupPython] H_element037  label="H_element : 0.090"  # scripted group (container) (typed FeaturePython)
  n = 0.090027
FEATURE [App::DocumentObjectGroupPython] C_element040  label="C_element : 0.585"  # scripted group (container) (typed FeaturePython)
  n = 0.585182
FEATURE [App::DocumentObjectGroupPython] O_element036  label="O_element : 0.325"  # scripted group (container) (typed FeaturePython)
  n = 0.324791
FEATURE [App::DocumentObjectGroupPython] G4_ETHYL_CELLULOSE  # scripted group (container) (typed FeaturePython)
  Dunit = g/cm3
  Dvalue = 1.13
  Group = -> [H_element037,C_element040,O_element036]
  conduct = 2
  density = 1
  expand = 3
  formula = G4_ETHYL_CELLULOSE
  name = G4_ETHYL_CELLULOSE
  specific = 4
FEATURE [App::DocumentObjectGroupPython] C_element041  label="C_element : 024"  # scripted group (container) (typed FeaturePython)
  n = 2
  ref = C_element
FEATURE [App::DocumentObjectGroupPython] H_element038  label="H_element : 020"  # scripted group (container) (typed FeaturePython)
  n = 4
  ref = H_element
FEATURE [App::DocumentObjectGroupPython] G4_ETHYLENE  # scripted group (container) (typed FeaturePython)
  Dunit = g/cm3
  Dvalue = 0.00117497
  Group = -> [C_element041,H_element038]
  conduct = 2
  density = 1
  expand = 3
  formula = G4_ETHYLENE
  name = G4_ETHYLENE
  specific = 4
FEATURE [App::DocumentObjectGroupPython] H_element039  label="H_element : 0.096"  # scripted group (container) (typed FeaturePython)
  n = 0.096
FEATURE [App::DocumentObjectGroupPython] C_element042  label="C_element : 0.195"  # scripted group (container) (typed FeaturePython)
  n = 0.195
FEATURE [App::DocumentObjectGroupPython] N_element016  label="N_element : 0.057"  # scripted group (container) (typed FeaturePython)
  n = 0.057
FEATURE [App::DocumentObjectGroupPython] O_element037  label="O_element : 0.646"  # scripted group (container) (typed FeaturePython)
  n = 0.646
FEATURE [App::DocumentObjectGroupPython] Na_element006  label="Na_element : 0.017"  # scripted group (container) (typed FeaturePython)
  n = 0.001
FEATURE [App::DocumentObjectGroupPython] P_element005  label="P_element : 0.104"  # scripted group (container) (typed FeaturePython)
  n = 0.001
FEATURE [App::DocumentObjectGroupPython] S_element010  label="S_element : 0.016"  # scripted group (container) (typed FeaturePython)
  n = 0.003
FEATURE [App::DocumentObjectGroupPython] Cl_element010  label="Cl_element : 0.005"  # scripted group (container) (typed FeaturePython)
  n = 0.001
FEATURE [App::DocumentObjectGroupPython] G4_EYE_LENS_ICRP  # scripted group (container) (typed FeaturePython)
  Dunit = g/cm3
  Dvalue = 1.07
  Group = -> [H_element039,C_element042,N_element016,O_element037,Na_element006,P_element005,S_element010,Cl_element010]
  conduct = 2
  density = 1
  expand = 3
  formula = G4_EYE_LENS_ICRP
  name = G4_EYE_LENS_ICRP
  specific = 4
FEATURE [App::DocumentObjectGroupPython] Fe_element003  label="Fe_element : 2"  # scripted group (container) (typed FeaturePython)
  n = 2
  ref = Fe_element
FEATURE [App::DocumentObjectGroupPython] O_element038  label="O_element : 019"  # scripted group (container) (typed FeaturePython)
  n = 3
  ref = O_element
FEATURE [App::DocumentObjectGroupPython] G4_FERRIC_OXIDE  # scripted group (container) (typed FeaturePython)
  Dunit = g/cm3
  Dvalue = 5.2
  Group = -> [Fe_element003,O_element038]
  conduct = 2
  density = 1
  expand = 3
  formula = G4_FERRIC_OXIDE
  name = G4_FERRIC_OXIDE
  specific = 4
FEATURE [App::DocumentObjectGroupPython] Fe_element004  label="Fe_element : 1"  # scripted group (container) (typed FeaturePython)
  n = 1
  ref = Fe_element
FEATURE [App::DocumentObjectGroupPython] B_element003  label="B_element : 1"  # scripted group (container) (typed FeaturePython)
  n = 1
  ref = B_element
FEATURE [App::DocumentObjectGroupPython] G4_FERROBORIDE  # scripted group (container) (typed FeaturePython)
  Dunit = g/cm3
  Dvalue = 7.15
  Group = -> [Fe_element004,B_element003]
  conduct = 2
  density = 1
  expand = 3
  formula = G4_FERROBORIDE
  name = G4_FERROBORIDE
  specific = 4
FEATURE [App::DocumentObjectGroupPython] Fe_element005  label="Fe_element : 003"  # scripted group (container) (typed FeaturePython)
  n = 1
  ref = Fe_element
FEATURE [App::DocumentObjectGroupPython] O_element039  label="O_element : 020"  # scripted group (container) (typed FeaturePython)
  n = 1
  ref = O_element
FEATURE [App::DocumentObjectGroupPython] G4_FERROUS_OXIDE  # scripted group (container) (typed FeaturePython)
  Dunit = g/cm3
  Dvalue = 5.7
  Group = -> [Fe_element005,O_element039]
  conduct = 2
  density = 1
  expand = 3
  formula = G4_FERROUS_OXIDE
  name = G4_FERROUS_OXIDE
  specific = 4
FEATURE [App::DocumentObjectGroupPython] H_element040  label="H_element : 0.115"  # scripted group (container) (typed FeaturePython)
  n = 0.108259
FEATURE [App::DocumentObjectGroupPython] N_element017  label="N_element : 0.000"  # scripted group (container) (typed FeaturePython)
  n = 2.7e-05
FEATURE [App::DocumentObjectGroupPython] O_element040  label="O_element : 0.879"  # scripted group (container) (typed FeaturePython)
  n = 0.878636
FEATURE [App::DocumentObjectGroupPython] Na_element007  label="Na_element : 0.000"  # scripted group (container) (typed FeaturePython)
  n = 2.2e-05
FEATURE [App::DocumentObjectGroupPython] S_element011  label="S_element : 0.013"  # scripted group (container) (typed FeaturePython)
  n = 0.012968
FEATURE [App::DocumentObjectGroupPython] Cl_element011  label="Cl_element : 0.000"  # scripted group (container) (typed FeaturePython)
  n = 3.4e-05
FEATURE [App::DocumentObjectGroupPython] Fe_element006  label="Fe_element : 0.000"  # scripted group (container) (typed FeaturePython)
  n = 5.4e-05
FEATURE [App::DocumentObjectGroupPython] G4_FERROUS_SULFATE  # scripted group (container) (typed FeaturePython)
  Dunit = g/cm3
  Dvalue = 1.024
  Group = -> [H_element040,N_element017,O_element040,Na_element007,S_element011,Cl_element011,Fe_element006]
  conduct = 2
  density = 1
  expand = 3
  formula = G4_FERROUS_SULFATE
  name = G4_FERROUS_SULFATE
  specific = 4
FEATURE [App::DocumentObjectGroupPython] C_element043  label="C_element : 0.099"  # scripted group (container) (typed FeaturePython)
  n = 0.099335
FEATURE [App::DocumentObjectGroupPython] F_element007  label="F_element : 0.314"  # scripted group (container) (typed FeaturePython)
  n = 0.314247
FEATURE [App::DocumentObjectGroupPython] Cl_element012  label="Cl_element : 0.586"  # scripted group (container) (typed FeaturePython)
  n = 0.586418
FEATURE [App::DocumentObjectGroupPython] G4_FREON_12  label="G4_FREON-12"  # scripted group (container) (typed FeaturePython)
  Dunit = g/cm3
  Dvalue = 1.12
  Group = -> [C_element043,F_element007,Cl_element012]
  conduct = 2
  density = 1
  expand = 3
  formula = G4_FREON-12
  name = G4_FREON-12
  specific = 4
FEATURE [App::DocumentObjectGroupPython] C_element044  label="C_element : 0.057"  # scripted group (container) (typed FeaturePython)
  n = 0.057245
FEATURE [App::DocumentObjectGroupPython] F_element008  label="F_element : 0.181"  # scripted group (container) (typed FeaturePython)
  n = 0.181096
FEATURE [App::DocumentObjectGroupPython] Br_element001  label="Br_element : 0.762"  # scripted group (container) (typed FeaturePython)
  n = 0.761659
FEATURE [App::DocumentObjectGroupPython] G4_FREON_12B2  label="G4_FREON-12B2"  # scripted group (container) (typed FeaturePython)
  Dunit = g/cm3
  Dvalue = 1.8
  Group = -> [C_element044,F_element008,Br_element001]
  conduct = 2
  density = 1
  expand = 3
  formula = G4_FREON-12B2
  name = G4_FREON-12B2
  specific = 4
FEATURE [App::DocumentObjectGroupPython] C_element045  label="C_element : 0.115"  # scripted group (container) (typed FeaturePython)
  n = 0.114983
FEATURE [App::DocumentObjectGroupPython] F_element009  label="F_element : 0.546"  # scripted group (container) (typed FeaturePython)
  n = 0.545621
FEATURE [App::DocumentObjectGroupPython] Cl_element013  label="Cl_element : 0.339"  # scripted group (container) (typed FeaturePython)
  n = 0.339396
FEATURE [App::DocumentObjectGroupPython] G4_FREON_13  label="G4_FREON-13"  # scripted group (container) (typed FeaturePython)
  Dunit = g/cm3
  Dvalue = 0.95
  Group = -> [C_element045,F_element009,Cl_element013]
  conduct = 2
  density = 1
  expand = 3
  formula = G4_FREON-13
  name = G4_FREON-13
  specific = 4
FEATURE [App::DocumentObjectGroupPython] C_element046  label="C_element : 025"  # scripted group (container) (typed FeaturePython)
  n = 1
  ref = C_element
FEATURE [App::DocumentObjectGroupPython] F_element010  label="F_element : 3"  # scripted group (container) (typed FeaturePython)
  n = 3
  ref = F_element
FEATURE [App::DocumentObjectGroupPython] Br_element002  label="Br_element : 1"  # scripted group (container) (typed FeaturePython)
  n = 1
  ref = Br_element
FEATURE [App::DocumentObjectGroupPython] G4_FREON_13B1  label="G4_FREON-13B1"  # scripted group (container) (typed FeaturePython)
  Dunit = g/cm3
  Dvalue = 1.5
  Group = -> [C_element046,F_element010,Br_element002]
  conduct = 2
  density = 1
  expand = 3
  formula = G4_FREON-13B1
  name = G4_FREON-13B1
  specific = 4
FEATURE [App::DocumentObjectGroupPython] C_element047  label="C_element : 0.061"  # scripted group (container) (typed FeaturePython)
  n = 0.061309
FEATURE [App::DocumentObjectGroupPython] F_element011  label="F_element : 0.291"  # scripted group (container) (typed FeaturePython)
  n = 0.290924
FEATURE [App::DocumentObjectGroupPython] I_element002  label="I_element : 0.648"  # scripted group (container) (typed FeaturePython)
  n = 0.647767
FEATURE [App::DocumentObjectGroupPython] G4_FREON_13I1  label="G4_FREON-13I1"  # scripted group (container) (typed FeaturePython)
  Dunit = g/cm3
  Dvalue = 1.8
  Group = -> [C_element047,F_element011,I_element002]
  conduct = 2
  density = 1
  expand = 3
  formula = G4_FREON-13I1
  name = G4_FREON-13I1
  specific = 4
FEATURE [App::DocumentObjectGroupPython] Gd_element001  label="Gd_element : 2"  # scripted group (container) (typed FeaturePython)
  n = 2
  ref = Gd_element
FEATURE [App::DocumentObjectGroupPython] O_element041  label="O_element : 021"  # scripted group (container) (typed FeaturePython)
  n = 2
  ref = O_element
FEATURE [App::DocumentObjectGroupPython] S_element012  label="S_element : 004"  # scripted group (container) (typed FeaturePython)
  n = 1
  ref = S_element
FEATURE [App::DocumentObjectGroupPython] G4_GADOLINIUM_OXYSULFIDE  # scripted group (container) (typed FeaturePython)
  Dunit = g/cm3
  Dvalue = 7.44
  Group = -> [Gd_element001,O_element041,S_element012]
  conduct = 2
  density = 1
  expand = 3
  formula = G4_GADOLINIUM_OXYSULFIDE
  name = G4_GADOLINIUM_OXYSULFIDE
  specific = 4
FEATURE [App::DocumentObjectGroupPython] Ga_element001  label="Ga_element : 1"  # scripted group (container) (typed FeaturePython)
  n = 1
  ref = Ga_element
FEATURE [App::DocumentObjectGroupPython] As_element001  label="As_element : 1"  # scripted group (container) (typed FeaturePython)
  n = 1
  ref = As_element
FEATURE [App::DocumentObjectGroupPython] G4_GALLIUM_ARSENIDE  # scripted group (container) (typed FeaturePython)
  Dunit = g/cm3
  Dvalue = 5.31
  Group = -> [Ga_element001,As_element001]
  conduct = 2
  density = 1
  expand = 3
  formula = G4_GALLIUM_ARSENIDE
  name = G4_GALLIUM_ARSENIDE
  specific = 4
FEATURE [App::DocumentObjectGroupPython] H_element041  label="H_element : 0.081"  # scripted group (container) (typed FeaturePython)
  n = 0.08118
FEATURE [App::DocumentObjectGroupPython] C_element048  label="C_element : 0.416"  # scripted group (container) (typed FeaturePython)
  n = 0.41606
FEATURE [App::DocumentObjectGroupPython] N_element018  label="N_element : 0.111"  # scripted group (container) (typed FeaturePython)
  n = 0.11124
FEATURE [App::DocumentObjectGroupPython] O_element042  label="O_element : 0.381"  # scripted group (container) (typed FeaturePython)
  n = 0.38064
FEATURE [App::DocumentObjectGroupPython] S_element013  label="S_element : 0.011"  # scripted group (container) (typed FeaturePython)
  n = 0.01088
FEATURE [App::DocumentObjectGroupPython] G4_GEL_PHOTO_EMULSION  # scripted group (container) (typed FeaturePython)
  Dunit = g/cm3
  Dvalue = 1.2914
  Group = -> [H_element041,C_element048,N_element018,O_element042,S_element013]
  conduct = 2
  density = 1
  expand = 3
  formula = G4_GEL_PHOTO_EMULSION
  name = G4_GEL_PHOTO_EMULSION
  specific = 4
FEATURE [App::DocumentObjectGroupPython] B_element004  label="B_element : 0.040"  # scripted group (container) (typed FeaturePython)
  n = 0.0400639
FEATURE [App::DocumentObjectGroupPython] O_element043  label="O_element : 0.540"  # scripted group (container) (typed FeaturePython)
  n = 0.539561
FEATURE [App::DocumentObjectGroupPython] Na_element008  label="Na_element : 0.028"  # scripted group (container) (typed FeaturePython)
  n = 0.0281909
FEATURE [App::DocumentObjectGroupPython] Al_element003  label="Al_element : 0.012"  # scripted group (container) (typed FeaturePython)
  n = 0.011644
FEATURE [App::DocumentObjectGroupPython] Si_element003  label="Si_element : 0.377"  # scripted group (container) (typed FeaturePython)
  n = 0.377219
FEATURE [App::DocumentObjectGroupPython] K_element004  label="K_element : 0.014"  # scripted group (container) (typed FeaturePython)
  n = 0.00332099
FEATURE [App::DocumentObjectGroupPython] G4_Pyrex_Glass  # scripted group (container) (typed FeaturePython)
  Dunit = g/cm3
  Dvalue = 2.23
  Group = -> [B_element004,O_element043,Na_element008,Al_element003,Si_element003,K_element004]
  conduct = 2
  density = 1
  expand = 3
  formula = G4_Pyrex_Glass
  name = G4_Pyrex_Glass
  specific = 4
FEATURE [App::DocumentObjectGroupPython] O_element044  label="O_element : 0.156"  # scripted group (container) (typed FeaturePython)
  n = 0.156453
FEATURE [App::DocumentObjectGroupPython] Si_element004  label="Si_element : 0.081"  # scripted group (container) (typed FeaturePython)
  n = 0.080866
FEATURE [App::DocumentObjectGroupPython] Ti_element001  label="Ti_element : 0.008"  # scripted group (container) (typed FeaturePython)
  n = 0.008092
FEATURE [App::DocumentObjectGroupPython] As_element002  label="As_element : 0.003"  # scripted group (container) (typed FeaturePython)
  n = 0.002651
FEATURE [App::DocumentObjectGroupPython] Pb_element001  label="Pb_element : 0.752"  # scripted group (container) (typed FeaturePython)
  n = 0.751938
FEATURE [App::DocumentObjectGroupPython] G4_GLASS_LEAD  # scripted group (container) (typed FeaturePython)
  Dunit = g/cm3
  Dvalue = 6.22
  Group = -> [O_element044,Si_element004,Ti_element001,As_element002,Pb_element001]
  conduct = 2
  density = 1
  expand = 3
  formula = G4_GLASS_LEAD
  name = G4_GLASS_LEAD
  specific = 4
FEATURE [App::DocumentObjectGroupPython] O_element045  label="O_element : 0.460"  # scripted group (container) (typed FeaturePython)
  n = 0.4598
FEATURE [App::DocumentObjectGroupPython] Na_element009  label="Na_element : 0.096"  # scripted group (container) (typed FeaturePython)
  n = 0.0964411
FEATURE [App::DocumentObjectGroupPython] Si_element005  label="Si_element : 0.378"  # scripted group (container) (typed FeaturePython)
  n = 0.336553
FEATURE [App::DocumentObjectGroupPython] Ca_element011  label="Ca_element : 0.107"  # scripted group (container) (typed FeaturePython)
  n = 0.107205
FEATURE [App::DocumentObjectGroupPython] G4_GLASS_PLATE  # scripted group (container) (typed FeaturePython)
  Dunit = g/cm3
  Dvalue = 2.4
  Group = -> [O_element045,Na_element009,Si_element005,Ca_element011]
  conduct = 2
  density = 1
  expand = 3
  formula = G4_GLASS_PLATE
  name = G4_GLASS_PLATE
  specific = 4
FEATURE [App::DocumentObjectGroupPython] C_element049  label="C_element : 026"  # scripted group (container) (typed FeaturePython)
  n = 5
  ref = C_element
FEATURE [App::DocumentObjectGroupPython] H_element042  label="H_element : 021"  # scripted group (container) (typed FeaturePython)
  n = 10
  ref = H_element
FEATURE [App::DocumentObjectGroupPython] N_element019  label="N_element : 2"  # scripted group (container) (typed FeaturePython)
  n = 2
  ref = N_element
FEATURE [App::DocumentObjectGroupPython] O_element046  label="O_element : 022"  # scripted group (container) (typed FeaturePython)
  n = 3
  ref = O_element
FEATURE [App::DocumentObjectGroupPython] G4_GLUTAMINE  # scripted group (container) (typed FeaturePython)
  Dunit = g/cm3
  Dvalue = 1.46
  Group = -> [C_element049,H_element042,N_element019,O_element046]
  conduct = 2
  density = 1
  expand = 3
  formula = G4_GLUTAMINE
  name = G4_GLUTAMINE
  specific = 4
FEATURE [App::DocumentObjectGroupPython] C_element050  label="C_element : 027"  # scripted group (container) (typed FeaturePython)
  n = 3
  ref = C_element
FEATURE [App::DocumentObjectGroupPython] H_element043  label="H_element : 022"  # scripted group (container) (typed FeaturePython)
  n = 8
  ref = H_element
FEATURE [App::DocumentObjectGroupPython] O_element047  label="O_element : 023"  # scripted group (container) (typed FeaturePython)
  n = 3
  ref = O_element
FEATURE [App::DocumentObjectGroupPython] G4_GLYCEROL  # scripted group (container) (typed FeaturePython)
  Dunit = g/cm3
  Dvalue = 1.2613
  Group = -> [C_element050,H_element043,O_element047]
  conduct = 2
  density = 1
  expand = 3
  formula = G4_GLYCEROL
  name = G4_GLYCEROL
  specific = 4
FEATURE [App::DocumentObjectGroupPython] C_element051  label="C_element : 028"  # scripted group (container) (typed FeaturePython)
  n = 5
  ref = C_element
FEATURE [App::DocumentObjectGroupPython] H_element044  label="H_element : 023"  # scripted group (container) (typed FeaturePython)
  n = 5
  ref = H_element
FEATURE [App::DocumentObjectGroupPython] N_element020  label="N_element : 009"  # scripted group (container) (typed FeaturePython)
  n = 5
  ref = N_element
FEATURE [App::DocumentObjectGroupPython] O_element048  label="O_element : 024"  # scripted group (container) (typed FeaturePython)
  n = 1
  ref = O_element
FEATURE [App::DocumentObjectGroupPython] G4_GUANINE  # scripted group (container) (typed FeaturePython)
  Dunit = g/cm3
  Dvalue = 2.2
  Group = -> [C_element051,H_element044,N_element020,O_element048]
  conduct = 2
  density = 1
  expand = 3
  formula = G4_GUANINE
  name = G4_GUANINE
  specific = 4
FEATURE [App::DocumentObjectGroupPython] Ca_element012  label="Ca_element : 006"  # scripted group (container) (typed FeaturePython)
  n = 1
  ref = Ca_element
FEATURE [App::DocumentObjectGroupPython] S_element014  label="S_element : 005"  # scripted group (container) (typed FeaturePython)
  n = 1
  ref = S_element
FEATURE [App::DocumentObjectGroupPython] O_element049  label="O_element : 6"  # scripted group (container) (typed FeaturePython)
  n = 6
  ref = O_element
FEATURE [App::DocumentObjectGroupPython] H_element045  label="H_element : 024"  # scripted group (container) (typed FeaturePython)
  n = 4
  ref = H_element
FEATURE [App::DocumentObjectGroupPython] G4_GYPSUM  # scripted group (container) (typed FeaturePython)
  Dunit = g/cm3
  Dvalue = 2.32
  Group = -> [Ca_element012,S_element014,O_element049,H_element045]
  conduct = 2
  density = 1
  expand = 3
  formula = G4_GYPSUM
  name = G4_GYPSUM
  specific = 4
FEATURE [App::DocumentObjectGroupPython] C_element052  label="C_element : 7"  # scripted group (container) (typed FeaturePython)
  n = 7
  ref = C_element
FEATURE [App::DocumentObjectGroupPython] H_element046  label="H_element : 16"  # scripted group (container) (typed FeaturePython)
  n = 16
  ref = H_element
FEATURE [App::DocumentObjectGroupPython] G4_N_HEPTANE  label="G4_N-HEPTANE"  # scripted group (container) (typed FeaturePython)
  Dunit = g/cm3
  Dvalue = 0.68376
  Group = -> [C_element052,H_element046]
  conduct = 2
  density = 1
  expand = 3
  formula = G4_N-HEPTANE
  name = G4_N-HEPTANE
  specific = 4
FEATURE [App::DocumentObjectGroupPython] C_element053  label="C_element : 029"  # scripted group (container) (typed FeaturePython)
  n = 6
  ref = C_element
FEATURE [App::DocumentObjectGroupPython] H_element047  label="H_element : 14"  # scripted group (container) (typed FeaturePython)
  n = 14
  ref = H_element
FEATURE [App::DocumentObjectGroupPython] G4_N_HEXANE  label="G4_N-HEXANE"  # scripted group (container) (typed FeaturePython)
  Dunit = g/cm3
  Dvalue = 0.6603
  Group = -> [C_element053,H_element047]
  conduct = 2
  density = 1
  expand = 3
  formula = G4_N-HEXANE
  name = G4_N-HEXANE
  specific = 4
FEATURE [App::DocumentObjectGroupPython] C_element054  label="C_element : 22"  # scripted group (container) (typed FeaturePython)
  n = 22
  ref = C_element
FEATURE [App::DocumentObjectGroupPython] H_element048  label="H_element : 025"  # scripted group (container) (typed FeaturePython)
  n = 10
  ref = H_element
FEATURE [App::DocumentObjectGroupPython] N_element021  label="N_element : 010"  # scripted group (container) (typed FeaturePython)
  n = 2
  ref = N_element
FEATURE [App::DocumentObjectGroupPython] O_element050  label="O_element : 025"  # scripted group (container) (typed FeaturePython)
  n = 5
  ref = O_element
FEATURE [App::DocumentObjectGroupPython] G4_KAPTON  # scripted group (container) (typed FeaturePython)
  Dunit = g/cm3
  Dvalue = 1.42
  Group = -> [C_element054,H_element048,N_element021,O_element050]
  conduct = 2
  density = 1
  expand = 3
  formula = G4_KAPTON
  name = G4_KAPTON
  specific = 4
FEATURE [App::DocumentObjectGroupPython] La_element001  label="La_element : 1"  # scripted group (container) (typed FeaturePython)
  n = 1
  ref = La_element
FEATURE [App::DocumentObjectGroupPython] Br_element003  label="Br_element : 002"  # scripted group (container) (typed FeaturePython)
  n = 1
  ref = Br_element
FEATURE [App::DocumentObjectGroupPython] O_element051  label="O_element : 026"  # scripted group (container) (typed FeaturePython)
  n = 1
  ref = O_element
FEATURE [App::DocumentObjectGroupPython] G4_LANTHANUM_OXYBROMIDE  # scripted group (container) (typed FeaturePython)
  Dunit = g/cm3
  Dvalue = 6.28
  Group = -> [La_element001,Br_element003,O_element051]
  conduct = 2
  density = 1
  expand = 3
  formula = G4_LANTHANUM_OXYBROMIDE
  name = G4_LANTHANUM_OXYBROMIDE
  specific = 4
FEATURE [App::DocumentObjectGroupPython] La_element002  label="La_element : 2"  # scripted group (container) (typed FeaturePython)
  n = 2
  ref = La_element
FEATURE [App::DocumentObjectGroupPython] O_element052  label="O_element : 027"  # scripted group (container) (typed FeaturePython)
  n = 2
  ref = O_element
FEATURE [App::DocumentObjectGroupPython] S_element015  label="S_element : 006"  # scripted group (container) (typed FeaturePython)
  n = 1
  ref = S_element
FEATURE [App::DocumentObjectGroupPython] G4_LANTHANUM_OXYSULFIDE  # scripted group (container) (typed FeaturePython)
  Dunit = g/cm3
  Dvalue = 5.86
  Group = -> [La_element002,O_element052,S_element015]
  conduct = 2
  density = 1
  expand = 3
  formula = G4_LANTHANUM_OXYSULFIDE
  name = G4_LANTHANUM_OXYSULFIDE
  specific = 4
FEATURE [App::DocumentObjectGroupPython] O_element053  label="O_element : 0.072"  # scripted group (container) (typed FeaturePython)
  n = 0.071682
FEATURE [App::DocumentObjectGroupPython] Pb_element002  label="Pb_element : 0.928"  # scripted group (container) (typed FeaturePython)
  n = 0.928318
FEATURE [App::DocumentObjectGroupPython] G4_LEAD_OXIDE  # scripted group (container) (typed FeaturePython)
  Dunit = g/cm3
  Dvalue = 9.53
  Group = -> [O_element053,Pb_element002]
  conduct = 2
  density = 1
  expand = 3
  formula = G4_LEAD_OXIDE
  name = G4_LEAD_OXIDE
  specific = 4
FEATURE [App::DocumentObjectGroupPython] Li_element001  label="Li_element : 1"  # scripted group (container) (typed FeaturePython)
  n = 1
  ref = Li_element
FEATURE [App::DocumentObjectGroupPython] N_element022  label="N_element : 011"  # scripted group (container) (typed FeaturePython)
  n = 1
  ref = N_element
FEATURE [App::DocumentObjectGroupPython] H_element049  label="H_element : 026"  # scripted group (container) (typed FeaturePython)
  n = 2
  ref = H_element
FEATURE [App::DocumentObjectGroupPython] G4_LITHIUM_AMIDE  # scripted group (container) (typed FeaturePython)
  Dunit = g/cm3
  Dvalue = 1.178
  Group = -> [Li_element001,N_element022,H_element049]
  conduct = 2
  density = 1
  expand = 3
  formula = G4_LITHIUM_AMIDE
  name = G4_LITHIUM_AMIDE
  specific = 4
FEATURE [App::DocumentObjectGroupPython] Li_element002  label="Li_element : 2"  # scripted group (container) (typed FeaturePython)
  n = 2
  ref = Li_element
FEATURE [App::DocumentObjectGroupPython] C_element055  label="C_element : 030"  # scripted group (container) (typed FeaturePython)
  n = 1
  ref = C_element
FEATURE [App::DocumentObjectGroupPython] O_element054  label="O_element : 028"  # scripted group (container) (typed FeaturePython)
  n = 3
  ref = O_element
FEATURE [App::DocumentObjectGroupPython] G4_LITHIUM_CARBONATE  # scripted group (container) (typed FeaturePython)
  Dunit = g/cm3
  Dvalue = 2.11
  Group = -> [Li_element002,C_element055,O_element054]
  conduct = 2
  density = 1
  expand = 3
  formula = G4_LITHIUM_CARBONATE
  name = G4_LITHIUM_CARBONATE
  specific = 4
FEATURE [App::DocumentObjectGroupPython] Li_element003  label="Li_element : 003"  # scripted group (container) (typed FeaturePython)
  n = 1
  ref = Li_element
FEATURE [App::DocumentObjectGroupPython] F_element012  label="F_element : 004"  # scripted group (container) (typed FeaturePython)
  n = 1
  ref = F_element
FEATURE [App::DocumentObjectGroupPython] G4_LITHIUM_FLUORIDE  # scripted group (container) (typed FeaturePython)
  Dunit = g/cm3
  Dvalue = 2.635
  Group = -> [Li_element003,F_element012]
  conduct = 2
  density = 1
  expand = 3
  formula = G4_LITHIUM_FLUORIDE
  name = G4_LITHIUM_FLUORIDE
  specific = 4
FEATURE [App::DocumentObjectGroupPython] Li_element004  label="Li_element : 004"  # scripted group (container) (typed FeaturePython)
  n = 1
  ref = Li_element
FEATURE [App::DocumentObjectGroupPython] H_element050  label="H_element : 027"  # scripted group (container) (typed FeaturePython)
  n = 1
  ref = H_element
FEATURE [App::DocumentObjectGroupPython] G4_LITHIUM_HYDRIDE  # scripted group (container) (typed FeaturePython)
  Dunit = g/cm3
  Dvalue = 0.82
  Group = -> [Li_element004,H_element050]
  conduct = 2
  density = 1
  expand = 3
  formula = G4_LITHIUM_HYDRIDE
  name = G4_LITHIUM_HYDRIDE
  specific = 4
FEATURE [App::DocumentObjectGroupPython] Li_element005  label="Li_element : 005"  # scripted group (container) (typed FeaturePython)
  n = 1
  ref = Li_element
FEATURE [App::DocumentObjectGroupPython] I_element003  label="I_element : 002"  # scripted group (container) (typed FeaturePython)
  n = 1
  ref = I_element
FEATURE [App::DocumentObjectGroupPython] G4_LITHIUM_IODIDE  # scripted group (container) (typed FeaturePython)
  Dunit = g/cm3
  Dvalue = 3.494
  Group = -> [Li_element005,I_element003]
  conduct = 2
  density = 1
  expand = 3
  formula = G4_LITHIUM_IODIDE
  name = G4_LITHIUM_IODIDE
  specific = 4
FEATURE [App::DocumentObjectGroupPython] Li_element006  label="Li_element : 006"  # scripted group (container) (typed FeaturePython)
  n = 2
  ref = Li_element
FEATURE [App::DocumentObjectGroupPython] O_element055  label="O_element : 029"  # scripted group (container) (typed FeaturePython)
  n = 1
  ref = O_element
FEATURE [App::DocumentObjectGroupPython] G4_LITHIUM_OXIDE  # scripted group (container) (typed FeaturePython)
  Dunit = g/cm3
  Dvalue = 2.013
  Group = -> [Li_element006,O_element055]
  conduct = 2
  density = 1
  expand = 3
  formula = G4_LITHIUM_OXIDE
  name = G4_LITHIUM_OXIDE
  specific = 4
FEATURE [App::DocumentObjectGroupPython] Li_element007  label="Li_element : 007"  # scripted group (container) (typed FeaturePython)
  n = 2
  ref = Li_element
FEATURE [App::DocumentObjectGroupPython] B_element005  label="B_element : 005"  # scripted group (container) (typed FeaturePython)
  n = 4
  ref = B_element
FEATURE [App::DocumentObjectGroupPython] O_element056  label="O_element : 7"  # scripted group (container) (typed FeaturePython)
  n = 7
  ref = O_element
FEATURE [App::DocumentObjectGroupPython] G4_LITHIUM_TETRABORATE  # scripted group (container) (typed FeaturePython)
  Dunit = g/cm3
  Dvalue = 2.44
  Group = -> [Li_element007,B_element005,O_element056]
  conduct = 2
  density = 1
  expand = 3
  formula = G4_LITHIUM_TETRABORATE
  name = G4_LITHIUM_TETRABORATE
  specific = 4
FEATURE [App::DocumentObjectGroupPython] H_element051  label="H_element : 0.105"  # scripted group (container) (typed FeaturePython)
  n = 0.105
FEATURE [App::DocumentObjectGroupPython] C_element056  label="C_element : 0.083"  # scripted group (container) (typed FeaturePython)
  n = 0.083
FEATURE [App::DocumentObjectGroupPython] N_element023  label="N_element : 0.023"  # scripted group (container) (typed FeaturePython)
  n = 0.023
FEATURE [App::DocumentObjectGroupPython] O_element057  label="O_element : 0.779"  # scripted group (container) (typed FeaturePython)
  n = 0.779
FEATURE [App::DocumentObjectGroupPython] Na_element010  label="Na_element : 0.097"  # scripted group (container) (typed FeaturePython)
  n = 0.002
FEATURE [App::DocumentObjectGroupPython] P_element006  label="P_element : 0.105"  # scripted group (container) (typed FeaturePython)
  n = 0.001
FEATURE [App::DocumentObjectGroupPython] S_element016  label="S_element : 0.017"  # scripted group (container) (typed FeaturePython)
  n = 0.002
FEATURE [App::DocumentObjectGroupPython] Cl_element014  label="Cl_element : 0.587"  # scripted group (container) (typed FeaturePython)
  n = 0.003
FEATURE [App::DocumentObjectGroupPython] K_element005  label="K_element : 0.015"  # scripted group (container) (typed FeaturePython)
  n = 0.002
FEATURE [App::DocumentObjectGroupPython] G4_LUNG_ICRP  # scripted group (container) (typed FeaturePython)
  Dunit = g/cm3
  Dvalue = 1.04
  Group = -> [H_element051,C_element056,N_element023,O_element057,Na_element010,P_element006,S_element016,Cl_element014,K_element005]
  conduct = 2
  density = 1
  expand = 3
  formula = G4_LUNG_ICRP
  name = G4_LUNG_ICRP
  specific = 4
FEATURE [App::DocumentObjectGroupPython] H_element052  label="H_element : 0.116"  # scripted group (container) (typed FeaturePython)
  n = 0.114318
FEATURE [App::DocumentObjectGroupPython] C_element057  label="C_element : 0.656"  # scripted group (container) (typed FeaturePython)
  n = 0.655824
FEATURE [App::DocumentObjectGroupPython] O_element058  label="O_element : 0.092"  # scripted group (container) (typed FeaturePython)
  n = 0.0921831
FEATURE [App::DocumentObjectGroupPython] Mg_element004  label="Mg_element : 0.135"  # scripted group (container) (typed FeaturePython)
  n = 0.134792
FEATURE [App::DocumentObjectGroupPython] Ca_element013  label="Ca_element : 0.003"  # scripted group (container) (typed FeaturePython)
  n = 0.002883
FEATURE [App::DocumentObjectGroupPython] G4_M3_WAX  # scripted group (container) (typed FeaturePython)
  Dunit = g/cm3
  Dvalue = 1.05
  Group = -> [H_element052,C_element057,O_element058,Mg_element004,Ca_element013]
  conduct = 2
  density = 1
  expand = 3
  formula = G4_M3_WAX
  name = G4_M3_WAX
  specific = 4
FEATURE [App::DocumentObjectGroupPython] Mg_element005  label="Mg_element : 1"  # scripted group (container) (typed FeaturePython)
  n = 1
  ref = Mg_element
FEATURE [App::DocumentObjectGroupPython] C_element058  label="C_element : 031"  # scripted group (container) (typed FeaturePython)
  n = 1
  ref = C_element
FEATURE [App::DocumentObjectGroupPython] O_element059  label="O_element : 030"  # scripted group (container) (typed FeaturePython)
  n = 3
  ref = O_element
FEATURE [App::DocumentObjectGroupPython] G4_MAGNESIUM_CARBONATE  # scripted group (container) (typed FeaturePython)
  Dunit = g/cm3
  Dvalue = 2.958
  Group = -> [Mg_element005,C_element058,O_element059]
  conduct = 2
  density = 1
  expand = 3
  formula = G4_MAGNESIUM_CARBONATE
  name = G4_MAGNESIUM_CARBONATE
  specific = 4
FEATURE [App::DocumentObjectGroupPython] Mg_element006  label="Mg_element : 002"  # scripted group (container) (typed FeaturePython)
  n = 1
  ref = Mg_element
FEATURE [App::DocumentObjectGroupPython] F_element013  label="F_element : 005"  # scripted group (container) (typed FeaturePython)
  n = 2
  ref = F_element
FEATURE [App::DocumentObjectGroupPython] G4_MAGNESIUM_FLUORIDE  # scripted group (container) (typed FeaturePython)
  Dunit = g/cm3
  Dvalue = 3
  Group = -> [Mg_element006,F_element013]
  conduct = 2
  density = 1
  expand = 3
  formula = G4_MAGNESIUM_FLUORIDE
  name = G4_MAGNESIUM_FLUORIDE
  specific = 4
FEATURE [App::DocumentObjectGroupPython] Mg_element007  label="Mg_element : 003"  # scripted group (container) (typed FeaturePython)
  n = 1
  ref = Mg_element
FEATURE [App::DocumentObjectGroupPython] O_element060  label="O_element : 031"  # scripted group (container) (typed FeaturePython)
  n = 1
  ref = O_element
FEATURE [App::DocumentObjectGroupPython] G4_MAGNESIUM_OXIDE  # scripted group (container) (typed FeaturePython)
  Dunit = g/cm3
  Dvalue = 3.58
  Group = -> [Mg_element007,O_element060]
  conduct = 2
  density = 1
  expand = 3
  formula = G4_MAGNESIUM_OXIDE
  name = G4_MAGNESIUM_OXIDE
  specific = 4
FEATURE [App::DocumentObjectGroupPython] Mg_element008  label="Mg_element : 004"  # scripted group (container) (typed FeaturePython)
  n = 1
  ref = Mg_element
FEATURE [App::DocumentObjectGroupPython] B_element006  label="B_element : 006"  # scripted group (container) (typed FeaturePython)
  n = 4
  ref = B_element
FEATURE [App::DocumentObjectGroupPython] O_element061  label="O_element : 032"  # scripted group (container) (typed FeaturePython)
  n = 7
  ref = O_element
FEATURE [App::DocumentObjectGroupPython] G4_MAGNESIUM_TETRABORATE  # scripted group (container) (typed FeaturePython)
  Dunit = g/cm3
  Dvalue = 2.53
  Group = -> [Mg_element008,B_element006,O_element061]
  conduct = 2
  density = 1
  expand = 3
  formula = G4_MAGNESIUM_TETRABORATE
  name = G4_MAGNESIUM_TETRABORATE
  specific = 4
FEATURE [App::DocumentObjectGroupPython] Hg_element001  label="Hg_element : 1"  # scripted group (container) (typed FeaturePython)
  n = 1
  ref = Hg_element
FEATURE [App::DocumentObjectGroupPython] I_element004  label="I_element : 2"  # scripted group (container) (typed FeaturePython)
  n = 2
  ref = I_element
FEATURE [App::DocumentObjectGroupPython] G4_MERCURIC_IODIDE  # scripted group (container) (typed FeaturePython)
  Dunit = g/cm3
  Dvalue = 6.36
  Group = -> [Hg_element001,I_element004]
  conduct = 2
  density = 1
  expand = 3
  formula = G4_MERCURIC_IODIDE
  name = G4_MERCURIC_IODIDE
  specific = 4
FEATURE [App::DocumentObjectGroupPython] C_element059  label="C_element : 032"  # scripted group (container) (typed FeaturePython)
  n = 1
  ref = C_element
FEATURE [App::DocumentObjectGroupPython] H_element053  label="H_element : 028"  # scripted group (container) (typed FeaturePython)
  n = 4
  ref = H_element
FEATURE [App::DocumentObjectGroupPython] G4_METHANE  # scripted group (container) (typed FeaturePython)
  Dunit = g/cm3
  Dvalue = 0.000667151
  Group = -> [C_element059,H_element053]
  conduct = 2
  density = 1
  expand = 3
  formula = G4_METHANE
  name = G4_METHANE
  specific = 4
FEATURE [App::DocumentObjectGroupPython] C_element060  label="C_element : 033"  # scripted group (container) (typed FeaturePython)
  n = 1
  ref = C_element
FEATURE [App::DocumentObjectGroupPython] H_element054  label="H_element : 029"  # scripted group (container) (typed FeaturePython)
  n = 4
  ref = H_element
FEATURE [App::DocumentObjectGroupPython] O_element062  label="O_element : 033"  # scripted group (container) (typed FeaturePython)
  n = 1
  ref = O_element
FEATURE [App::DocumentObjectGroupPython] G4_METHANOL  # scripted group (container) (typed FeaturePython)
  Dunit = g/cm3
  Dvalue = 0.7914
  Group = -> [C_element060,H_element054,O_element062]
  conduct = 2
  density = 1
  expand = 3
  formula = G4_METHANOL
  name = G4_METHANOL
  specific = 4
FEATURE [App::DocumentObjectGroupPython] H_element055  label="H_element : 0.134"  # scripted group (container) (typed FeaturePython)
  n = 0.13404
FEATURE [App::DocumentObjectGroupPython] C_element061  label="C_element : 0.778"  # scripted group (container) (typed FeaturePython)
  n = 0.77796
FEATURE [App::DocumentObjectGroupPython] O_element063  label="O_element : 0.035"  # scripted group (container) (typed FeaturePython)
  n = 0.03502
FEATURE [App::DocumentObjectGroupPython] Mg_element009  label="Mg_element : 0.039"  # scripted group (container) (typed FeaturePython)
  n = 0.038594
FEATURE [App::DocumentObjectGroupPython] Ti_element002  label="Ti_element : 0.014"  # scripted group (container) (typed FeaturePython)
  n = 0.014386
FEATURE [App::DocumentObjectGroupPython] G4_MIX_D_WAX  # scripted group (container) (typed FeaturePython)
  Dunit = g/cm3
  Dvalue = 0.99
  Group = -> [H_element055,C_element061,O_element063,Mg_element009,Ti_element002]
  conduct = 2
  density = 1
  expand = 3
  formula = G4_MIX_D_WAX
  name = G4_MIX_D_WAX
  specific = 4
FEATURE [App::DocumentObjectGroupPython] H_element056  label="H_element : 0.135"  # scripted group (container) (typed FeaturePython)
  n = 0.081192
FEATURE [App::DocumentObjectGroupPython] C_element062  label="C_element : 0.583"  # scripted group (container) (typed FeaturePython)
  n = 0.583442
FEATURE [App::DocumentObjectGroupPython] N_element024  label="N_element : 0.018"  # scripted group (container) (typed FeaturePython)
  n = 0.017798
FEATURE [App::DocumentObjectGroupPython] O_element064  label="O_element : 0.186"  # scripted group (container) (typed FeaturePython)
  n = 0.186381
FEATURE [App::DocumentObjectGroupPython] Mg_element010  label="Mg_element : 0.130"  # scripted group (container) (typed FeaturePython)
  n = 0.130287
FEATURE [App::DocumentObjectGroupPython] Cl_element015  label="Cl_element : 0.588"  # scripted group (container) (typed FeaturePython)
  n = 0.0009
FEATURE [App::DocumentObjectGroupPython] G4_MS20_TISSUE  # scripted group (container) (typed FeaturePython)
  Dunit = g/cm3
  Dvalue = 1
  Group = -> [H_element056,C_element062,N_element024,O_element064,Mg_element010,Cl_element015]
  conduct = 2
  density = 1
  expand = 3
  formula = G4_MS20_TISSUE
  name = G4_MS20_TISSUE
  specific = 4
FEATURE [App::DocumentObjectGroupPython] H_element057  label="H_element : 0.136"  # scripted group (container) (typed FeaturePython)
  n = 0.102
FEATURE [App::DocumentObjectGroupPython] C_element063  label="C_element : 0.143"  # scripted group (container) (typed FeaturePython)
  n = 0.143
FEATURE [App::DocumentObjectGroupPython] N_element025  label="N_element : 0.034"  # scripted group (container) (typed FeaturePython)
  n = 0.034
FEATURE [App::DocumentObjectGroupPython] O_element065  label="O_element : 0.710"  # scripted group (container) (typed FeaturePython)
  n = 0.71
FEATURE [App::DocumentObjectGroupPython] Na_element011  label="Na_element : 0.098"  # scripted group (container) (typed FeaturePython)
  n = 0.001
FEATURE [App::DocumentObjectGroupPython] P_element007  label="P_element : 0.002"  # scripted group (container) (typed FeaturePython)
  n = 0.002
FEATURE [App::DocumentObjectGroupPython] S_element017  label="S_element : 0.018"  # scripted group (container) (typed FeaturePython)
  n = 0.003
FEATURE [App::DocumentObjectGroupPython] Cl_element016  label="Cl_element : 0.589"  # scripted group (container) (typed FeaturePython)
  n = 0.001
FEATURE [App::DocumentObjectGroupPython] K_element006  label="K_element : 0.004"  # scripted group (container) (typed FeaturePython)
  n = 0.004
FEATURE [App::DocumentObjectGroupPython] G4_MUSCLE_SKELETAL_ICRP  # scripted group (container) (typed FeaturePython)
  Dunit = g/cm3
  Dvalue = 1.05
  Group = -> [H_element057,C_element063,N_element025,O_element065,Na_element011,P_element007,S_element017,Cl_element016,K_element006]
  conduct = 2
  density = 1
  expand = 3
  formula = G4_MUSCLE_SKELETAL_ICRP
  name = G4_MUSCLE_SKELETAL_ICRP
  specific = 4
FEATURE [App::DocumentObjectGroupPython] H_element058  label="H_element : 0.137"  # scripted group (container) (typed FeaturePython)
  n = 0.102102
FEATURE [App::DocumentObjectGroupPython] C_element064  label="C_element : 0.123"  # scripted group (container) (typed FeaturePython)
  n = 0.123123
FEATURE [App::DocumentObjectGroupPython] N_element026  label="N_element : 0.756"  # scripted group (container) (typed FeaturePython)
  n = 0.035035
FEATURE [App::DocumentObjectGroupPython] O_element066  label="O_element : 0.730"  # scripted group (container) (typed FeaturePython)
  n = 0.72973
FEATURE [App::DocumentObjectGroupPython] Na_element012  label="Na_element : 0.099"  # scripted group (container) (typed FeaturePython)
  n = 0.001001
FEATURE [App::DocumentObjectGroupPython] P_element008  label="P_element : 0.106"  # scripted group (container) (typed FeaturePython)
  n = 0.002002
FEATURE [App::DocumentObjectGroupPython] S_element018  label="S_element : 0.019"  # scripted group (container) (typed FeaturePython)
  n = 0.004004
FEATURE [App::DocumentObjectGroupPython] K_element007  label="K_element : 0.016"  # scripted group (container) (typed FeaturePython)
  n = 0.003003
FEATURE [App::DocumentObjectGroupPython] G4_MUSCLE_STRIATED_ICRU  # scripted group (container) (typed FeaturePython)
  Dunit = g/cm3
  Dvalue = 1.04
  Group = -> [H_element058,C_element064,N_element026,O_element066,Na_element012,P_element008,S_element018,K_element007]
  conduct = 2
  density = 1
  expand = 3
  formula = G4_MUSCLE_STRIATED_ICRU
  name = G4_MUSCLE_STRIATED_ICRU
  specific = 4
FEATURE [App::DocumentObjectGroupPython] H_element059  label="H_element : 0.098"  # scripted group (container) (typed FeaturePython)
  n = 0.0982341
FEATURE [App::DocumentObjectGroupPython] C_element065  label="C_element : 0.156"  # scripted group (container) (typed FeaturePython)
  n = 0.156214
FEATURE [App::DocumentObjectGroupPython] N_element027  label="N_element : 0.757"  # scripted group (container) (typed FeaturePython)
  n = 0.035451
FEATURE [App::DocumentObjectGroupPython] O_element067  label="O_element : 0.880"  # scripted group (container) (typed FeaturePython)
  n = 0.710101
FEATURE [App::DocumentObjectGroupPython] G4_MUSCLE_WITH_SUCROSE  # scripted group (container) (typed FeaturePython)
  Dunit = g/cm3
  Dvalue = 1.11
  Group = -> [H_element059,C_element065,N_element027,O_element067]
  conduct = 2
  density = 1
  expand = 3
  formula = G4_MUSCLE_WITH_SUCROSE
  name = G4_MUSCLE_WITH_SUCROSE
  specific = 4
FEATURE [App::DocumentObjectGroupPython] H_element060  label="H_element : 0.138"  # scripted group (container) (typed FeaturePython)
  n = 0.101969
FEATURE [App::DocumentObjectGroupPython] C_element066  label="C_element : 0.120"  # scripted group (container) (typed FeaturePython)
  n = 0.120058
FEATURE [App::DocumentObjectGroupPython] N_element028  label="N_element : 0.758"  # scripted group (container) (typed FeaturePython)
  n = 0.035451
FEATURE [App::DocumentObjectGroupPython] O_element068  label="O_element : 0.743"  # scripted group (container) (typed FeaturePython)
  n = 0.742522
FEATURE [App::DocumentObjectGroupPython] G4_MUSCLE_WITHOUT_SUCROSE  # scripted group (container) (typed FeaturePython)
  Dunit = g/cm3
  Dvalue = 1.07
  Group = -> [H_element060,C_element066,N_element028,O_element068]
  conduct = 2
  density = 1
  expand = 3
  formula = G4_MUSCLE_WITHOUT_SUCROSE
  name = G4_MUSCLE_WITHOUT_SUCROSE
  specific = 4
FEATURE [App::DocumentObjectGroupPython] C_element067  label="C_element : 10"  # scripted group (container) (typed FeaturePython)
  n = 10
  ref = C_element
FEATURE [App::DocumentObjectGroupPython] H_element061  label="H_element : 030"  # scripted group (container) (typed FeaturePython)
  n = 8
  ref = H_element
FEATURE [App::DocumentObjectGroupPython] G4_NAPHTHALENE  # scripted group (container) (typed FeaturePython)
  Dunit = g/cm3
  Dvalue = 1.145
  Group = -> [C_element067,H_element061]
  conduct = 2
  density = 1
  expand = 3
  formula = G4_NAPHTHALENE
  name = G4_NAPHTHALENE
  specific = 4
FEATURE [App::DocumentObjectGroupPython] C_element068  label="C_element : 034"  # scripted group (container) (typed FeaturePython)
  n = 6
  ref = C_element
FEATURE [App::DocumentObjectGroupPython] H_element062  label="H_element : 031"  # scripted group (container) (typed FeaturePython)
  n = 5
  ref = H_element
FEATURE [App::DocumentObjectGroupPython] N_element029  label="N_element : 012"  # scripted group (container) (typed FeaturePython)
  n = 1
  ref = N_element
FEATURE [App::DocumentObjectGroupPython] O_element069  label="O_element : 034"  # scripted group (container) (typed FeaturePython)
  n = 2
  ref = O_element
FEATURE [App::DocumentObjectGroupPython] G4_NITROBENZENE  # scripted group (container) (typed FeaturePython)
  Dunit = g/cm3
  Dvalue = 1.19867
  Group = -> [C_element068,H_element062,N_element029,O_element069]
  conduct = 2
  density = 1
  expand = 3
  formula = G4_NITROBENZENE
  name = G4_NITROBENZENE
  specific = 4
FEATURE [App::DocumentObjectGroupPython] N_element030  label="N_element : 013"  # scripted group (container) (typed FeaturePython)
  n = 2
  ref = N_element
FEATURE [App::DocumentObjectGroupPython] O_element070  label="O_element : 035"  # scripted group (container) (typed FeaturePython)
  n = 1
  ref = O_element
FEATURE [App::DocumentObjectGroupPython] G4_NITROUS_OXIDE  # scripted group (container) (typed FeaturePython)
  Dunit = g/cm3
  Dvalue = 0.00183094
  Group = -> [N_element030,O_element070]
  conduct = 2
  density = 1
  expand = 3
  formula = G4_NITROUS_OXIDE
  name = G4_NITROUS_OXIDE
  specific = 4
FEATURE [App::DocumentObjectGroupPython] H_element063  label="H_element : 0.104"  # scripted group (container) (typed FeaturePython)
  n = 0.103509
FEATURE [App::DocumentObjectGroupPython] C_element069  label="C_element : 0.648"  # scripted group (container) (typed FeaturePython)
  n = 0.648416
FEATURE [App::DocumentObjectGroupPython] N_element031  label="N_element : 0.100"  # scripted group (container) (typed FeaturePython)
  n = 0.0995361
FEATURE [App::DocumentObjectGroupPython] O_element071  label="O_element : 0.149"  # scripted group (container) (typed FeaturePython)
  n = 0.148539
FEATURE [App::DocumentObjectGroupPython] G4_NYLON_8062  label="G4_NYLON-8062"  # scripted group (container) (typed FeaturePython)
  Dunit = g/cm3
  Dvalue = 1.08
  Group = -> [H_element063,C_element069,N_element031,O_element071]
  conduct = 2
  density = 1
  expand = 3
  formula = G4_NYLON-8062
  name = G4_NYLON-8062
  specific = 4
FEATURE [App::DocumentObjectGroupPython] C_element070  label="C_element : 035"  # scripted group (container) (typed FeaturePython)
  n = 6
  ref = C_element
FEATURE [App::DocumentObjectGroupPython] H_element064  label="H_element : 11"  # scripted group (container) (typed FeaturePython)
  n = 11
  ref = H_element
FEATURE [App::DocumentObjectGroupPython] N_element032  label="N_element : 014"  # scripted group (container) (typed FeaturePython)
  n = 1
  ref = N_element
FEATURE [App::DocumentObjectGroupPython] O_element072  label="O_element : 036"  # scripted group (container) (typed FeaturePython)
  n = 1
  ref = O_element
FEATURE [App::DocumentObjectGroupPython] G4_NYLON_6_6  label="G4_NYLON-6-6"  # scripted group (container) (typed FeaturePython)
  Dunit = g/cm3
  Dvalue = 1.14
  Group = -> [C_element070,H_element064,N_element032,O_element072]
  conduct = 2
  density = 1
  expand = 3
  formula = G4_NYLON-6-6
  name = G4_NYLON-6-6
  specific = 4
FEATURE [App::DocumentObjectGroupPython] H_element065  label="H_element : 0.139"  # scripted group (container) (typed FeaturePython)
  n = 0.107062
FEATURE [App::DocumentObjectGroupPython] C_element071  label="C_element : 0.680"  # scripted group (container) (typed FeaturePython)
  n = 0.680449
FEATURE [App::DocumentObjectGroupPython] N_element033  label="N_element : 0.099"  # scripted group (container) (typed FeaturePython)
  n = 0.099189
FEATURE [App::DocumentObjectGroupPython] O_element073  label="O_element : 0.113"  # scripted group (container) (typed FeaturePython)
  n = 0.1133
FEATURE [App::DocumentObjectGroupPython] G4_NYLON_6_10  label="G4_NYLON-6-10"  # scripted group (container) (typed FeaturePython)
  Dunit = g/cm3
  Dvalue = 1.14
  Group = -> [H_element065,C_element071,N_element033,O_element073]
  conduct = 2
  density = 1
  expand = 3
  formula = G4_NYLON-6-10
  name = G4_NYLON-6-10
  specific = 4
FEATURE [App::DocumentObjectGroupPython] H_element066  label="H_element : 0.140"  # scripted group (container) (typed FeaturePython)
  n = 0.115476
FEATURE [App::DocumentObjectGroupPython] C_element072  label="C_element : 0.721"  # scripted group (container) (typed FeaturePython)
  n = 0.720818
FEATURE [App::DocumentObjectGroupPython] N_element034  label="N_element : 0.076"  # scripted group (container) (typed FeaturePython)
  n = 0.0764169
FEATURE [App::DocumentObjectGroupPython] O_element074  label="O_element : 0.087"  # scripted group (container) (typed FeaturePython)
  n = 0.0872889
FEATURE [App::DocumentObjectGroupPython] G4_NYLON_11_RILSAN  label="G4_NYLON-11_RILSAN"  # scripted group (container) (typed FeaturePython)
  Dunit = g/cm3
  Dvalue = 1.425
  Group = -> [H_element066,C_element072,N_element034,O_element074]
  conduct = 2
  density = 1
  expand = 3
  formula = G4_NYLON-11_RILSAN
  name = G4_NYLON-11_RILSAN
  specific = 4
FEATURE [App::DocumentObjectGroupPython] C_element073  label="C_element : 8"  # scripted group (container) (typed FeaturePython)
  n = 8
  ref = C_element
FEATURE [App::DocumentObjectGroupPython] H_element067  label="H_element : 18"  # scripted group (container) (typed FeaturePython)
  n = 18
  ref = H_element
FEATURE [App::DocumentObjectGroupPython] G4_OCTANE  # scripted group (container) (typed FeaturePython)
  Dunit = g/cm3
  Dvalue = 0.7026
  Group = -> [C_element073,H_element067]
  conduct = 2
  density = 1
  expand = 3
  formula = G4_OCTANE
  name = G4_OCTANE
  specific = 4
FEATURE [App::DocumentObjectGroupPython] C_element074  label="C_element : 25"  # scripted group (container) (typed FeaturePython)
  n = 25
  ref = C_element
FEATURE [App::DocumentObjectGroupPython] H_element068  label="H_element : 52"  # scripted group (container) (typed FeaturePython)
  n = 52
  ref = H_element
FEATURE [App::DocumentObjectGroupPython] G4_PARAFFIN  # scripted group (container) (typed FeaturePython)
  Dunit = g/cm3
  Dvalue = 0.93
  Group = -> [C_element074,H_element068]
  conduct = 2
  density = 1
  expand = 3
  formula = G4_PARAFFIN
  name = G4_PARAFFIN
  specific = 4
FEATURE [App::DocumentObjectGroupPython] C_element075  label="C_element : 036"  # scripted group (container) (typed FeaturePython)
  n = 5
  ref = C_element
FEATURE [App::DocumentObjectGroupPython] H_element069  label="H_element : 032"  # scripted group (container) (typed FeaturePython)
  n = 12
  ref = H_element
FEATURE [App::DocumentObjectGroupPython] G4_N_PENTANE  label="G4_N-PENTANE"  # scripted group (container) (typed FeaturePython)
  Dunit = g/cm3
  Dvalue = 0.6262
  Group = -> [C_element075,H_element069]
  conduct = 2
  density = 1
  expand = 3
  formula = G4_N-PENTANE
  name = G4_N-PENTANE
  specific = 4
FEATURE [App::DocumentObjectGroupPython] H_element070  label="H_element : 0.014"  # scripted group (container) (typed FeaturePython)
  n = 0.0141
FEATURE [App::DocumentObjectGroupPython] C_element076  label="C_element : 0.072"  # scripted group (container) (typed FeaturePython)
  n = 0.072261
FEATURE [App::DocumentObjectGroupPython] N_element035  label="N_element : 0.019"  # scripted group (container) (typed FeaturePython)
  n = 0.01932
FEATURE [App::DocumentObjectGroupPython] O_element075  label="O_element : 0.066"  # scripted group (container) (typed FeaturePython)
  n = 0.066101
FEATURE [App::DocumentObjectGroupPython] S_element019  label="S_element : 0.020"  # scripted group (container) (typed FeaturePython)
  n = 0.00189
FEATURE [App::DocumentObjectGroupPython] Br_element004  label="Br_element : 0.349"  # scripted group (container) (typed FeaturePython)
  n = 0.349103
FEATURE [App::DocumentObjectGroupPython] Ag_element001  label="Ag_element : 0.474"  # scripted group (container) (typed FeaturePython)
  n = 0.474105
FEATURE [App::DocumentObjectGroupPython] I_element005  label="I_element : 0.003"  # scripted group (container) (typed FeaturePython)
  n = 0.00312
FEATURE [App::DocumentObjectGroupPython] G4_PHOTO_EMULSION  # scripted group (container) (typed FeaturePython)
  Dunit = g/cm3
  Dvalue = 3.815
  Group = -> [H_element070,C_element076,N_element035,O_element075,S_element019,Br_element004,Ag_element001,I_element005]
  conduct = 2
  density = 1
  expand = 3
  formula = G4_PHOTO_EMULSION
  name = G4_PHOTO_EMULSION
  specific = 4
FEATURE [App::DocumentObjectGroupPython] C_element077  label="C_element : 9"  # scripted group (container) (typed FeaturePython)
  n = 9
  ref = C_element
FEATURE [App::DocumentObjectGroupPython] H_element071  label="H_element : 033"  # scripted group (container) (typed FeaturePython)
  n = 10
  ref = H_element
FEATURE [App::DocumentObjectGroupPython] G4_PLASTIC_SC_VINYLTOLUENE  # scripted group (container) (typed FeaturePython)
  Dunit = g/cm3
  Dvalue = 1.032
  Group = -> [C_element077,H_element071]
  conduct = 2
  density = 1
  expand = 3
  formula = G4_PLASTIC_SC_VINYLTOLUENE
  name = G4_PLASTIC_SC_VINYLTOLUENE
  specific = 4
FEATURE [App::DocumentObjectGroupPython] Pu_element001  label="Pu_element : 1"  # scripted group (container) (typed FeaturePython)
  n = 1
  ref = Pu_element
FEATURE [App::DocumentObjectGroupPython] O_element076  label="O_element : 037"  # scripted group (container) (typed FeaturePython)
  n = 2
  ref = O_element
FEATURE [App::DocumentObjectGroupPython] G4_PLUTONIUM_DIOXIDE  # scripted group (container) (typed FeaturePython)
  Dunit = g/cm3
  Dvalue = 11.46
  Group = -> [Pu_element001,O_element076]
  conduct = 2
  density = 1
  expand = 3
  formula = G4_PLUTONIUM_DIOXIDE
  name = G4_PLUTONIUM_DIOXIDE
  specific = 4
FEATURE [App::DocumentObjectGroupPython] C_element078  label="C_element : 037"  # scripted group (container) (typed FeaturePython)
  n = 3
  ref = C_element
FEATURE [App::DocumentObjectGroupPython] H_element072  label="H_element : 034"  # scripted group (container) (typed FeaturePython)
  n = 3
  ref = H_element
FEATURE [App::DocumentObjectGroupPython] N_element036  label="N_element : 015"  # scripted group (container) (typed FeaturePython)
  n = 1
  ref = N_element
FEATURE [App::DocumentObjectGroupPython] G4_POLYACRYLONITRILE  # scripted group (container) (typed FeaturePython)
  Dunit = g/cm3
  Dvalue = 1.17
  Group = -> [C_element078,H_element072,N_element036]
  conduct = 2
  density = 1
  expand = 3
  formula = G4_POLYACRYLONITRILE
  name = G4_POLYACRYLONITRILE
  specific = 4
FEATURE [App::DocumentObjectGroupPython] C_element079  label="C_element : 16"  # scripted group (container) (typed FeaturePython)
  n = 16
  ref = C_element
FEATURE [App::DocumentObjectGroupPython] H_element073  label="H_element : 035"  # scripted group (container) (typed FeaturePython)
  n = 14
  ref = H_element
FEATURE [App::DocumentObjectGroupPython] O_element077  label="O_element : 038"  # scripted group (container) (typed FeaturePython)
  n = 3
  ref = O_element
FEATURE [App::DocumentObjectGroupPython] G4_POLYCARBONATE  # scripted group (container) (typed FeaturePython)
  Dunit = g/cm3
  Dvalue = 1.2
  Group = -> [C_element079,H_element073,O_element077]
  conduct = 2
  density = 1
  expand = 3
  formula = G4_POLYCARBONATE
  name = G4_POLYCARBONATE
  specific = 4
FEATURE [App::DocumentObjectGroupPython] C_element080  label="C_element : 038"  # scripted group (container) (typed FeaturePython)
  n = 8
  ref = C_element
FEATURE [App::DocumentObjectGroupPython] H_element074  label="H_element : 036"  # scripted group (container) (typed FeaturePython)
  n = 7
  ref = H_element
FEATURE [App::DocumentObjectGroupPython] Cl_element017  label="Cl_element : 007"  # scripted group (container) (typed FeaturePython)
  n = 1
  ref = Cl_element
FEATURE [App::DocumentObjectGroupPython] G4_POLYCHLOROSTYRENE  # scripted group (container) (typed FeaturePython)
  Dunit = g/cm3
  Dvalue = 1.3
  Group = -> [C_element080,H_element074,Cl_element017]
  conduct = 2
  density = 1
  expand = 3
  formula = G4_POLYCHLOROSTYRENE
  name = G4_POLYCHLOROSTYRENE
  specific = 4
FEATURE [App::DocumentObjectGroupPython] C_element081  label="C_element : 039"  # scripted group (container) (typed FeaturePython)
  n = 1
  ref = C_element
FEATURE [App::DocumentObjectGroupPython] H_element075  label="H_element : 037"  # scripted group (container) (typed FeaturePython)
  n = 2
  ref = H_element
FEATURE [App::DocumentObjectGroupPython] G4_POLYETHYLENE  # scripted group (container) (typed FeaturePython)
  Dunit = g/cm3
  Dvalue = 0.94
  Group = -> [C_element081,H_element075]
  conduct = 2
  density = 1
  expand = 3
  formula = G4_POLYETHYLENE
  name = G4_POLYETHYLENE
  specific = 4
FEATURE [App::DocumentObjectGroupPython] C_element082  label="C_element : 040"  # scripted group (container) (typed FeaturePython)
  n = 10
  ref = C_element
FEATURE [App::DocumentObjectGroupPython] H_element076  label="H_element : 038"  # scripted group (container) (typed FeaturePython)
  n = 8
  ref = H_element
FEATURE [App::DocumentObjectGroupPython] O_element078  label="O_element : 039"  # scripted group (container) (typed FeaturePython)
  n = 4
  ref = O_element
FEATURE [App::DocumentObjectGroupPython] G4_MYLAR  # scripted group (container) (typed FeaturePython)
  Dunit = g/cm3
  Dvalue = 1.4
  Group = -> [C_element082,H_element076,O_element078]
  conduct = 2
  density = 1
  expand = 3
  formula = G4_MYLAR
  name = G4_MYLAR
  specific = 4
FEATURE [App::DocumentObjectGroupPython] C_element083  label="C_element : 041"  # scripted group (container) (typed FeaturePython)
  n = 5
  ref = C_element
FEATURE [App::DocumentObjectGroupPython] H_element077  label="H_element : 039"  # scripted group (container) (typed FeaturePython)
  n = 8
  ref = H_element
FEATURE [App::DocumentObjectGroupPython] O_element079  label="O_element : 040"  # scripted group (container) (typed FeaturePython)
  n = 2
  ref = O_element
FEATURE [App::DocumentObjectGroupPython] G4_PLEXIGLASS  # scripted group (container) (typed FeaturePython)
  Dunit = g/cm3
  Dvalue = 1.19
  Group = -> [C_element083,H_element077,O_element079]
  conduct = 2
  density = 1
  expand = 3
  formula = G4_PLEXIGLASS
  name = G4_PLEXIGLASS
  specific = 4
FEATURE [App::DocumentObjectGroupPython] C_element084  label="C_element : 042"  # scripted group (container) (typed FeaturePython)
  n = 1
  ref = C_element
FEATURE [App::DocumentObjectGroupPython] H_element078  label="H_element : 040"  # scripted group (container) (typed FeaturePython)
  n = 2
  ref = H_element
FEATURE [App::DocumentObjectGroupPython] O_element080  label="O_element : 041"  # scripted group (container) (typed FeaturePython)
  n = 1
  ref = O_element
FEATURE [App::DocumentObjectGroupPython] G4_POLYOXYMETHYLENE  # scripted group (container) (typed FeaturePython)
  Dunit = g/cm3
  Dvalue = 1.425
  Group = -> [C_element084,H_element078,O_element080]
  conduct = 2
  density = 1
  expand = 3
  formula = G4_POLYOXYMETHYLENE
  name = G4_POLYOXYMETHYLENE
  specific = 4
FEATURE [App::DocumentObjectGroupPython] C_element085  label="C_element : 043"  # scripted group (container) (typed FeaturePython)
  n = 2
  ref = C_element
FEATURE [App::DocumentObjectGroupPython] H_element079  label="H_element : 041"  # scripted group (container) (typed FeaturePython)
  n = 4
  ref = H_element
FEATURE [App::DocumentObjectGroupPython] G4_POLYPROPYLENE  # scripted group (container) (typed FeaturePython)
  Dunit = g/cm3
  Dvalue = 0.9
  Group = -> [C_element085,H_element079]
  conduct = 2
  density = 1
  expand = 3
  formula = G4_POLYPROPYLENE
  name = G4_POLYPROPYLENE
  specific = 4
FEATURE [App::DocumentObjectGroupPython] C_element086  label="C_element : 044"  # scripted group (container) (typed FeaturePython)
  n = 8
  ref = C_element
FEATURE [App::DocumentObjectGroupPython] H_element080  label="H_element : 042"  # scripted group (container) (typed FeaturePython)
  n = 8
  ref = H_element
FEATURE [App::DocumentObjectGroupPython] G4_POLYSTYRENE  # scripted group (container) (typed FeaturePython)
  Dunit = g/cm3
  Dvalue = 1.06
  Group = -> [C_element086,H_element080]
  conduct = 2
  density = 1
  expand = 3
  formula = G4_POLYSTYRENE
  name = G4_POLYSTYRENE
  specific = 4
FEATURE [App::DocumentObjectGroupPython] C_element087  label="C_element : 045"  # scripted group (container) (typed FeaturePython)
  n = 2
  ref = C_element
FEATURE [App::DocumentObjectGroupPython] F_element014  label="F_element : 4"  # scripted group (container) (typed FeaturePython)
  n = 4
  ref = F_element
FEATURE [App::DocumentObjectGroupPython] G4_TEFLON  # scripted group (container) (typed FeaturePython)
  Dunit = g/cm3
  Dvalue = 2.2
  Group = -> [C_element087,F_element014]
  conduct = 2
  density = 1
  expand = 3
  formula = G4_TEFLON
  name = G4_TEFLON
  specific = 4
FEATURE [App::DocumentObjectGroupPython] C_element088  label="C_element : 046"  # scripted group (container) (typed FeaturePython)
  n = 2
  ref = C_element
FEATURE [App::DocumentObjectGroupPython] F_element015  label="F_element : 006"  # scripted group (container) (typed FeaturePython)
  n = 3
  ref = F_element
FEATURE [App::DocumentObjectGroupPython] Cl_element018  label="Cl_element : 008"  # scripted group (container) (typed FeaturePython)
  n = 1
  ref = Cl_element
FEATURE [App::DocumentObjectGroupPython] G4_POLYTRIFLUOROCHLOROETHYLENE  # scripted group (container) (typed FeaturePython)
  Dunit = g/cm3
  Dvalue = 2.1
  Group = -> [C_element088,F_element015,Cl_element018]
  conduct = 2
  density = 1
  expand = 3
  formula = G4_POLYTRIFLUOROCHLOROETHYLENE
  name = G4_POLYTRIFLUOROCHLOROETHYLENE
  specific = 4
FEATURE [App::DocumentObjectGroupPython] C_element089  label="C_element : 047"  # scripted group (container) (typed FeaturePython)
  n = 4
  ref = C_element
FEATURE [App::DocumentObjectGroupPython] H_element081  label="H_element : 043"  # scripted group (container) (typed FeaturePython)
  n = 6
  ref = H_element
FEATURE [App::DocumentObjectGroupPython] O_element081  label="O_element : 042"  # scripted group (container) (typed FeaturePython)
  n = 2
  ref = O_element
FEATURE [App::DocumentObjectGroupPython] G4_POLYVINYL_ACETATE  # scripted group (container) (typed FeaturePython)
  Dunit = g/cm3
  Dvalue = 1.19
  Group = -> [C_element089,H_element081,O_element081]
  conduct = 2
  density = 1
  expand = 3
  formula = G4_POLYVINYL_ACETATE
  name = G4_POLYVINYL_ACETATE
  specific = 4
FEATURE [App::DocumentObjectGroupPython] C_element090  label="C_element : 048"  # scripted group (container) (typed FeaturePython)
  n = 2
  ref = C_element
FEATURE [App::DocumentObjectGroupPython] H_element082  label="H_element : 044"  # scripted group (container) (typed FeaturePython)
  n = 4
  ref = H_element
FEATURE [App::DocumentObjectGroupPython] O_element082  label="O_element : 043"  # scripted group (container) (typed FeaturePython)
  n = 1
  ref = O_element
FEATURE [App::DocumentObjectGroupPython] G4_POLYVINYL_ALCOHOL  # scripted group (container) (typed FeaturePython)
  Dunit = g/cm3
  Dvalue = 1.3
  Group = -> [C_element090,H_element082,O_element082]
  conduct = 2
  density = 1
  expand = 3
  formula = G4_POLYVINYL_ALCOHOL
  name = G4_POLYVINYL_ALCOHOL
  specific = 4
FEATURE [App::DocumentObjectGroupPython] C_element091  label="C_element : 049"  # scripted group (container) (typed FeaturePython)
  n = 8
  ref = C_element
FEATURE [App::DocumentObjectGroupPython] H_element083  label="H_element : 045"  # scripted group (container) (typed FeaturePython)
  n = 14
  ref = H_element
FEATURE [App::DocumentObjectGroupPython] O_element083  label="O_element : 044"  # scripted group (container) (typed FeaturePython)
  n = 2
  ref = O_element
FEATURE [App::DocumentObjectGroupPython] G4_POLYVINYL_BUTYRAL  # scripted group (container) (typed FeaturePython)
  Dunit = g/cm3
  Dvalue = 1.12
  Group = -> [C_element091,H_element083,O_element083]
  conduct = 2
  density = 1
  expand = 3
  formula = G4_POLYVINYL_BUTYRAL
  name = G4_POLYVINYL_BUTYRAL
  specific = 4
FEATURE [App::DocumentObjectGroupPython] C_element092  label="C_element : 050"  # scripted group (container) (typed FeaturePython)
  n = 2
  ref = C_element
FEATURE [App::DocumentObjectGroupPython] H_element084  label="H_element : 046"  # scripted group (container) (typed FeaturePython)
  n = 3
  ref = H_element
FEATURE [App::DocumentObjectGroupPython] Cl_element019  label="Cl_element : 009"  # scripted group (container) (typed FeaturePython)
  n = 1
  ref = Cl_element
FEATURE [App::DocumentObjectGroupPython] G4_POLYVINYL_CHLORIDE  # scripted group (container) (typed FeaturePython)
  Dunit = g/cm3
  Dvalue = 1.3
  Group = -> [C_element092,H_element084,Cl_element019]
  conduct = 2
  density = 1
  expand = 3
  formula = G4_POLYVINYL_CHLORIDE
  name = G4_POLYVINYL_CHLORIDE
  specific = 4
FEATURE [App::DocumentObjectGroupPython] C_element093  label="C_element : 051"  # scripted group (container) (typed FeaturePython)
  n = 2
  ref = C_element
FEATURE [App::DocumentObjectGroupPython] H_element085  label="H_element : 047"  # scripted group (container) (typed FeaturePython)
  n = 2
  ref = H_element
FEATURE [App::DocumentObjectGroupPython] Cl_element020  label="Cl_element : 010"  # scripted group (container) (typed FeaturePython)
  n = 2
  ref = Cl_element
FEATURE [App::DocumentObjectGroupPython] G4_POLYVINYLIDENE_CHLORIDE  # scripted group (container) (typed FeaturePython)
  Dunit = g/cm3
  Dvalue = 1.7
  Group = -> [C_element093,H_element085,Cl_element020]
  conduct = 2
  density = 1
  expand = 3
  formula = G4_POLYVINYLIDENE_CHLORIDE
  name = G4_POLYVINYLIDENE_CHLORIDE
  specific = 4
FEATURE [App::DocumentObjectGroupPython] C_element094  label="C_element : 052"  # scripted group (container) (typed FeaturePython)
  n = 2
  ref = C_element
FEATURE [App::DocumentObjectGroupPython] H_element086  label="H_element : 048"  # scripted group (container) (typed FeaturePython)
  n = 2
  ref = H_element
FEATURE [App::DocumentObjectGroupPython] F_element016  label="F_element : 007"  # scripted group (container) (typed FeaturePython)
  n = 2
  ref = F_element
FEATURE [App::DocumentObjectGroupPython] G4_POLYVINYLIDENE_FLUORIDE  # scripted group (container) (typed FeaturePython)
  Dunit = g/cm3
  Dvalue = 1.76
  Group = -> [C_element094,H_element086,F_element016]
  conduct = 2
  density = 1
  expand = 3
  formula = G4_POLYVINYLIDENE_FLUORIDE
  name = G4_POLYVINYLIDENE_FLUORIDE
  specific = 4
FEATURE [App::DocumentObjectGroupPython] C_element095  label="C_element : 053"  # scripted group (container) (typed FeaturePython)
  n = 6
  ref = C_element
FEATURE [App::DocumentObjectGroupPython] H_element087  label="H_element : 9"  # scripted group (container) (typed FeaturePython)
  n = 9
  ref = H_element
FEATURE [App::DocumentObjectGroupPython] N_element037  label="N_element : 016"  # scripted group (container) (typed FeaturePython)
  n = 1
  ref = N_element
FEATURE [App::DocumentObjectGroupPython] O_element084  label="O_element : 045"  # scripted group (container) (typed FeaturePython)
  n = 1
  ref = O_element
FEATURE [App::DocumentObjectGroupPython] G4_POLYVINYL_PYRROLIDONE  # scripted group (container) (typed FeaturePython)
  Dunit = g/cm3
  Dvalue = 1.25
  Group = -> [C_element095,H_element087,N_element037,O_element084]
  conduct = 2
  density = 1
  expand = 3
  formula = G4_POLYVINYL_PYRROLIDONE
  name = G4_POLYVINYL_PYRROLIDONE
  specific = 4
FEATURE [App::DocumentObjectGroupPython] K_element008  label="K_element : 1"  # scripted group (container) (typed FeaturePython)
  n = 1
  ref = K_element
FEATURE [App::DocumentObjectGroupPython] I_element006  label="I_element : 003"  # scripted group (container) (typed FeaturePython)
  n = 1
  ref = I_element
FEATURE [App::DocumentObjectGroupPython] G4_POTASSIUM_IODIDE  # scripted group (container) (typed FeaturePython)
  Dunit = g/cm3
  Dvalue = 3.13
  Group = -> [K_element008,I_element006]
  conduct = 2
  density = 1
  expand = 3
  formula = G4_POTASSIUM_IODIDE
  name = G4_POTASSIUM_IODIDE
  specific = 4
FEATURE [App::DocumentObjectGroupPython] K_element009  label="K_element : 2"  # scripted group (container) (typed FeaturePython)
  n = 2
  ref = K_element
FEATURE [App::DocumentObjectGroupPython] O_element085  label="O_element : 046"  # scripted group (container) (typed FeaturePython)
  n = 1
  ref = O_element
FEATURE [App::DocumentObjectGroupPython] G4_POTASSIUM_OXIDE  # scripted group (container) (typed FeaturePython)
  Dunit = g/cm3
  Dvalue = 2.32
  Group = -> [K_element009,O_element085]
  conduct = 2
  density = 1
  expand = 3
  formula = G4_POTASSIUM_OXIDE
  name = G4_POTASSIUM_OXIDE
  specific = 4
FEATURE [App::DocumentObjectGroupPython] C_element096  label="C_element : 054"  # scripted group (container) (typed FeaturePython)
  n = 3
  ref = C_element
FEATURE [App::DocumentObjectGroupPython] H_element088  label="H_element : 049"  # scripted group (container) (typed FeaturePython)
  n = 8
  ref = H_element
FEATURE [App::DocumentObjectGroupPython] G4_PROPANE  # scripted group (container) (typed FeaturePython)
  Dunit = g/cm3
  Dvalue = 0.00187939
  Group = -> [C_element096,H_element088]
  conduct = 2
  density = 1
  expand = 3
  formula = G4_PROPANE
  name = G4_PROPANE
  specific = 4
FEATURE [App::DocumentObjectGroupPython] C_element097  label="C_element : 055"  # scripted group (container) (typed FeaturePython)
  n = 3
  ref = C_element
FEATURE [App::DocumentObjectGroupPython] H_element089  label="H_element : 050"  # scripted group (container) (typed FeaturePython)
  n = 8
  ref = H_element
FEATURE [App::DocumentObjectGroupPython] G4_lPROPANE  # scripted group (container) (typed FeaturePython)
  Dunit = g/cm3
  Dvalue = 0.43
  Group = -> [C_element097,H_element089]
  conduct = 2
  density = 1
  expand = 3
  formula = G4_lPROPANE
  name = G4_lPROPANE
  specific = 4
FEATURE [App::DocumentObjectGroupPython] C_element098  label="C_element : 056"  # scripted group (container) (typed FeaturePython)
  n = 3
  ref = C_element
FEATURE [App::DocumentObjectGroupPython] H_element090  label="H_element : 051"  # scripted group (container) (typed FeaturePython)
  n = 8
  ref = H_element
FEATURE [App::DocumentObjectGroupPython] O_element086  label="O_element : 047"  # scripted group (container) (typed FeaturePython)
  n = 1
  ref = O_element
FEATURE [App::DocumentObjectGroupPython] G4_N_PROPYL_ALCOHOL  label="G4_N-PROPYL_ALCOHOL"  # scripted group (container) (typed FeaturePython)
  Dunit = g/cm3
  Dvalue = 0.8035
  Group = -> [C_element098,H_element090,O_element086]
  conduct = 2
  density = 1
  expand = 3
  formula = G4_N-PROPYL_ALCOHOL
  name = G4_N-PROPYL_ALCOHOL
  specific = 4
FEATURE [App::DocumentObjectGroupPython] C_element099  label="C_element : 057"  # scripted group (container) (typed FeaturePython)
  n = 5
  ref = C_element
FEATURE [App::DocumentObjectGroupPython] H_element091  label="H_element : 052"  # scripted group (container) (typed FeaturePython)
  n = 5
  ref = H_element
FEATURE [App::DocumentObjectGroupPython] N_element038  label="N_element : 017"  # scripted group (container) (typed FeaturePython)
  n = 1
  ref = N_element
FEATURE [App::DocumentObjectGroupPython] G4_PYRIDINE  # scripted group (container) (typed FeaturePython)
  Dunit = g/cm3
  Dvalue = 0.9819
  Group = -> [C_element099,H_element091,N_element038]
  conduct = 2
  density = 1
  expand = 3
  formula = G4_PYRIDINE
  name = G4_PYRIDINE
  specific = 4
FEATURE [App::DocumentObjectGroupPython] H_element092  label="H_element : 0.144"  # scripted group (container) (typed FeaturePython)
  n = 0.143711
FEATURE [App::DocumentObjectGroupPython] C_element100  label="C_element : 0.856"  # scripted group (container) (typed FeaturePython)
  n = 0.856289
FEATURE [App::DocumentObjectGroupPython] G4_RUBBER_BUTYL  # scripted group (container) (typed FeaturePython)
  Dunit = g/cm3
  Dvalue = 0.92
  Group = -> [H_element092,C_element100]
  conduct = 2
  density = 1
  expand = 3
  formula = G4_RUBBER_BUTYL
  name = G4_RUBBER_BUTYL
  specific = 4
FEATURE [App::DocumentObjectGroupPython] H_element093  label="H_element : 0.118"  # scripted group (container) (typed FeaturePython)
  n = 0.118371
FEATURE [App::DocumentObjectGroupPython] C_element101  label="C_element : 0.882"  # scripted group (container) (typed FeaturePython)
  n = 0.881629
FEATURE [App::DocumentObjectGroupPython] G4_RUBBER_NATURAL  # scripted group (container) (typed FeaturePython)
  Dunit = g/cm3
  Dvalue = 0.92
  Group = -> [H_element093,C_element101]
  conduct = 2
  density = 1
  expand = 3
  formula = G4_RUBBER_NATURAL
  name = G4_RUBBER_NATURAL
  specific = 4
FEATURE [App::DocumentObjectGroupPython] H_element094  label="H_element : 0.145"  # scripted group (container) (typed FeaturePython)
  n = 0.05692
FEATURE [App::DocumentObjectGroupPython] C_element102  label="C_element : 0.543"  # scripted group (container) (typed FeaturePython)
  n = 0.542646
FEATURE [App::DocumentObjectGroupPython] Cl_element021  label="Cl_element : 0.400"  # scripted group (container) (typed FeaturePython)
  n = 0.400434
FEATURE [App::DocumentObjectGroupPython] G4_RUBBER_NEOPRENE  # scripted group (container) (typed FeaturePython)
  Dunit = g/cm3
  Dvalue = 1.23
  Group = -> [H_element094,C_element102,Cl_element021]
  conduct = 2
  density = 1
  expand = 3
  formula = G4_RUBBER_NEOPRENE
  name = G4_RUBBER_NEOPRENE
  specific = 4
FEATURE [App::DocumentObjectGroupPython] Si_element006  label="Si_element : 1"  # scripted group (container) (typed FeaturePython)
  n = 1
  ref = Si_element
FEATURE [App::DocumentObjectGroupPython] O_element087  label="O_element : 048"  # scripted group (container) (typed FeaturePython)
  n = 2
  ref = O_element
FEATURE [App::DocumentObjectGroupPython] G4_SILICON_DIOXIDE  # scripted group (container) (typed FeaturePython)
  Dunit = g/cm3
  Dvalue = 2.32
  Group = -> [Si_element006,O_element087]
  conduct = 2
  density = 1
  expand = 3
  formula = G4_SILICON_DIOXIDE
  name = G4_SILICON_DIOXIDE
  specific = 4
FEATURE [App::DocumentObjectGroupPython] Ag_element002  label="Ag_element : 1"  # scripted group (container) (typed FeaturePython)
  n = 1
  ref = Ag_element
FEATURE [App::DocumentObjectGroupPython] Br_element005  label="Br_element : 003"  # scripted group (container) (typed FeaturePython)
  n = 1
  ref = Br_element
FEATURE [App::DocumentObjectGroupPython] G4_SILVER_BROMIDE  # scripted group (container) (typed FeaturePython)
  Dunit = g/cm3
  Dvalue = 6.473
  Group = -> [Ag_element002,Br_element005]
  conduct = 2
  density = 1
  expand = 3
  formula = G4_SILVER_BROMIDE
  name = G4_SILVER_BROMIDE
  specific = 4
FEATURE [App::DocumentObjectGroupPython] Ag_element003  label="Ag_element : 002"  # scripted group (container) (typed FeaturePython)
  n = 1
  ref = Ag_element
FEATURE [App::DocumentObjectGroupPython] Cl_element022  label="Cl_element : 011"  # scripted group (container) (typed FeaturePython)
  n = 1
  ref = Cl_element
FEATURE [App::DocumentObjectGroupPython] G4_SILVER_CHLORIDE  # scripted group (container) (typed FeaturePython)
  Dunit = g/cm3
  Dvalue = 5.56
  Group = -> [Ag_element003,Cl_element022]
  conduct = 2
  density = 1
  expand = 3
  formula = G4_SILVER_CHLORIDE
  name = G4_SILVER_CHLORIDE
  specific = 4
FEATURE [App::DocumentObjectGroupPython] Br_element006  label="Br_element : 0.423"  # scripted group (container) (typed FeaturePython)
  n = 0.422895
FEATURE [App::DocumentObjectGroupPython] Ag_element004  label="Ag_element : 0.574"  # scripted group (container) (typed FeaturePython)
  n = 0.573748
FEATURE [App::DocumentObjectGroupPython] I_element007  label="I_element : 0.649"  # scripted group (container) (typed FeaturePython)
  n = 0.003357
FEATURE [App::DocumentObjectGroupPython] G4_SILVER_HALIDES  # scripted group (container) (typed FeaturePython)
  Dunit = g/cm3
  Dvalue = 6.47
  Group = -> [Br_element006,Ag_element004,I_element007]
  conduct = 2
  density = 1
  expand = 3
  formula = G4_SILVER_HALIDES
  name = G4_SILVER_HALIDES
  specific = 4
FEATURE [App::DocumentObjectGroupPython] Ag_element005  label="Ag_element : 003"  # scripted group (container) (typed FeaturePython)
  n = 1
  ref = Ag_element
FEATURE [App::DocumentObjectGroupPython] I_element008  label="I_element : 004"  # scripted group (container) (typed FeaturePython)
  n = 1
  ref = I_element
FEATURE [App::DocumentObjectGroupPython] G4_SILVER_IODIDE  # scripted group (container) (typed FeaturePython)
  Dunit = g/cm3
  Dvalue = 6.01
  Group = -> [Ag_element005,I_element008]
  conduct = 2
  density = 1
  expand = 3
  formula = G4_SILVER_IODIDE
  name = G4_SILVER_IODIDE
  specific = 4
FEATURE [App::DocumentObjectGroupPython] H_element095  label="H_element : 0.100"  # scripted group (container) (typed FeaturePython)
  n = 0.1
FEATURE [App::DocumentObjectGroupPython] C_element103  label="C_element : 0.204"  # scripted group (container) (typed FeaturePython)
  n = 0.204
FEATURE [App::DocumentObjectGroupPython] N_element039  label="N_element : 0.759"  # scripted group (container) (typed FeaturePython)
  n = 0.042
FEATURE [App::DocumentObjectGroupPython] O_element088  label="O_element : 0.645"  # scripted group (container) (typed FeaturePython)
  n = 0.645
FEATURE [App::DocumentObjectGroupPython] Na_element013  label="Na_element : 0.100"  # scripted group (container) (typed FeaturePython)
  n = 0.002
FEATURE [App::DocumentObjectGroupPython] P_element009  label="P_element : 0.107"  # scripted group (container) (typed FeaturePython)
  n = 0.001
FEATURE [App::DocumentObjectGroupPython] S_element020  label="S_element : 0.021"  # scripted group (container) (typed FeaturePython)
  n = 0.002
FEATURE [App::DocumentObjectGroupPython] Cl_element023  label="Cl_element : 0.590"  # scripted group (container) (typed FeaturePython)
  n = 0.003
FEATURE [App::DocumentObjectGroupPython] K_element010  label="K_element : 0.001"  # scripted group (container) (typed FeaturePython)
  n = 0.001
FEATURE [App::DocumentObjectGroupPython] G4_SKIN_ICRP  # scripted group (container) (typed FeaturePython)
  Dunit = g/cm3
  Dvalue = 1.09
  Group = -> [H_element095,C_element103,N_element039,O_element088,Na_element013,P_element009,S_element020,Cl_element023,K_element010]
  conduct = 2
  density = 1
  expand = 3
  formula = G4_SKIN_ICRP
  name = G4_SKIN_ICRP
  specific = 4
FEATURE [App::DocumentObjectGroupPython] Na_element014  label="Na_element : 2"  # scripted group (container) (typed FeaturePython)
  n = 2
  ref = Na_element
FEATURE [App::DocumentObjectGroupPython] C_element104  label="C_element : 058"  # scripted group (container) (typed FeaturePython)
  n = 1
  ref = C_element
FEATURE [App::DocumentObjectGroupPython] O_element089  label="O_element : 049"  # scripted group (container) (typed FeaturePython)
  n = 3
  ref = O_element
FEATURE [App::DocumentObjectGroupPython] G4_SODIUM_CARBONATE  # scripted group (container) (typed FeaturePython)
  Dunit = g/cm3
  Dvalue = 2.532
  Group = -> [Na_element014,C_element104,O_element089]
  conduct = 2
  density = 1
  expand = 3
  formula = G4_SODIUM_CARBONATE
  name = G4_SODIUM_CARBONATE
  specific = 4
FEATURE [App::DocumentObjectGroupPython] Na_element015  label="Na_element : 1"  # scripted group (container) (typed FeaturePython)
  n = 1
  ref = Na_element
FEATURE [App::DocumentObjectGroupPython] I_element009  label="I_element : 005"  # scripted group (container) (typed FeaturePython)
  n = 1
  ref = I_element
FEATURE [App::DocumentObjectGroupPython] G4_SODIUM_IODIDE  # scripted group (container) (typed FeaturePython)
  Dunit = g/cm3
  Dvalue = 3.667
  Group = -> [Na_element015,I_element009]
  conduct = 2
  density = 1
  expand = 3
  formula = G4_SODIUM_IODIDE
  name = G4_SODIUM_IODIDE
  specific = 4
FEATURE [App::DocumentObjectGroupPython] Na_element016  label="Na_element : 003"  # scripted group (container) (typed FeaturePython)
  n = 2
  ref = Na_element
FEATURE [App::DocumentObjectGroupPython] O_element090  label="O_element : 050"  # scripted group (container) (typed FeaturePython)
  n = 1
  ref = O_element
FEATURE [App::DocumentObjectGroupPython] G4_SODIUM_MONOXIDE  # scripted group (container) (typed FeaturePython)
  Dunit = g/cm3
  Dvalue = 2.27
  Group = -> [Na_element016,O_element090]
  conduct = 2
  density = 1
  expand = 3
  formula = G4_SODIUM_MONOXIDE
  name = G4_SODIUM_MONOXIDE
  specific = 4
FEATURE [App::DocumentObjectGroupPython] Na_element017  label="Na_element : 004"  # scripted group (container) (typed FeaturePython)
  n = 1
  ref = Na_element
FEATURE [App::DocumentObjectGroupPython] N_element040  label="N_element : 018"  # scripted group (container) (typed FeaturePython)
  n = 1
  ref = N_element
FEATURE [App::DocumentObjectGroupPython] O_element091  label="O_element : 051"  # scripted group (container) (typed FeaturePython)
  n = 3
  ref = O_element
FEATURE [App::DocumentObjectGroupPython] G4_SODIUM_NITRATE  # scripted group (container) (typed FeaturePython)
  Dunit = g/cm3
  Dvalue = 2.261
  Group = -> [Na_element017,N_element040,O_element091]
  conduct = 2
  density = 1
  expand = 3
  formula = G4_SODIUM_NITRATE
  name = G4_SODIUM_NITRATE
  specific = 4
FEATURE [App::DocumentObjectGroupPython] C_element105  label="C_element : 059"  # scripted group (container) (typed FeaturePython)
  n = 14
  ref = C_element
FEATURE [App::DocumentObjectGroupPython] H_element096  label="H_element : 053"  # scripted group (container) (typed FeaturePython)
  n = 12
  ref = H_element
FEATURE [App::DocumentObjectGroupPython] G4_STILBENE  # scripted group (container) (typed FeaturePython)
  Dunit = g/cm3
  Dvalue = 0.9707
  Group = -> [C_element105,H_element096]
  conduct = 2
  density = 1
  expand = 3
  formula = G4_STILBENE
  name = G4_STILBENE
  specific = 4
FEATURE [App::DocumentObjectGroupPython] C_element106  label="C_element : 12"  # scripted group (container) (typed FeaturePython)
  n = 12
  ref = C_element
FEATURE [App::DocumentObjectGroupPython] H_element097  label="H_element : 22"  # scripted group (container) (typed FeaturePython)
  n = 22
  ref = H_element
FEATURE [App::DocumentObjectGroupPython] O_element092  label="O_element : 11"  # scripted group (container) (typed FeaturePython)
  n = 11
  ref = O_element
FEATURE [App::DocumentObjectGroupPython] G4_SUCROSE  # scripted group (container) (typed FeaturePython)
  Dunit = g/cm3
  Dvalue = 1.5805
  Group = -> [C_element106,H_element097,O_element092]
  conduct = 2
  density = 1
  expand = 3
  formula = G4_SUCROSE
  name = G4_SUCROSE
  specific = 4
FEATURE [App::DocumentObjectGroupPython] C_element107  label="C_element : 18"  # scripted group (container) (typed FeaturePython)
  n = 18
  ref = C_element
FEATURE [App::DocumentObjectGroupPython] H_element098  label="H_element : 054"  # scripted group (container) (typed FeaturePython)
  n = 14
  ref = H_element
FEATURE [App::DocumentObjectGroupPython] G4_TERPHENYL  # scripted group (container) (typed FeaturePython)
  Dunit = g/cm3
  Dvalue = 1.24
  Group = -> [C_element107,H_element098]
  conduct = 2
  density = 1
  expand = 3
  formula = G4_TERPHENYL
  name = G4_TERPHENYL
  specific = 4
FEATURE [App::DocumentObjectGroupPython] H_element099  label="H_element : 0.146"  # scripted group (container) (typed FeaturePython)
  n = 0.106
FEATURE [App::DocumentObjectGroupPython] C_element108  label="C_element : 0.883"  # scripted group (container) (typed FeaturePython)
  n = 0.099
FEATURE [App::DocumentObjectGroupPython] N_element041  label="N_element : 0.020"  # scripted group (container) (typed FeaturePython)
  n = 0.02
FEATURE [App::DocumentObjectGroupPython] O_element093  label="O_element : 0.766"  # scripted group (container) (typed FeaturePython)
  n = 0.766
FEATURE [App::DocumentObjectGroupPython] Na_element018  label="Na_element : 0.101"  # scripted group (container) (typed FeaturePython)
  n = 0.002
FEATURE [App::DocumentObjectGroupPython] P_element010  label="P_element : 0.108"  # scripted group (container) (typed FeaturePython)
  n = 0.001
FEATURE [App::DocumentObjectGroupPython] S_element021  label="S_element : 0.022"  # scripted group (container) (typed FeaturePython)
  n = 0.002
FEATURE [App::DocumentObjectGroupPython] Cl_element024  label="Cl_element : 0.002"  # scripted group (container) (typed FeaturePython)
  n = 0.002
FEATURE [App::DocumentObjectGroupPython] K_element011  label="K_element : 0.017"  # scripted group (container) (typed FeaturePython)
  n = 0.002
FEATURE [App::DocumentObjectGroupPython] G4_TESTIS_ICRP  # scripted group (container) (typed FeaturePython)
  Dunit = g/cm3
  Dvalue = 1.04
  Group = -> [H_element099,C_element108,N_element041,O_element093,Na_element018,P_element010,S_element021,Cl_element024,K_element011]
  conduct = 2
  density = 1
  expand = 3
  formula = G4_TESTIS_ICRP
  name = G4_TESTIS_ICRP
  specific = 4
FEATURE [App::DocumentObjectGroupPython] C_element109  label="C_element : 060"  # scripted group (container) (typed FeaturePython)
  n = 2
  ref = C_element
FEATURE [App::DocumentObjectGroupPython] Cl_element025  label="Cl_element : 012"  # scripted group (container) (typed FeaturePython)
  n = 4
  ref = Cl_element
FEATURE [App::DocumentObjectGroupPython] G4_TETRACHLOROETHYLENE  # scripted group (container) (typed FeaturePython)
  Dunit = g/cm3
  Dvalue = 1.625
  Group = -> [C_element109,Cl_element025]
  conduct = 2
  density = 1
  expand = 3
  formula = G4_TETRACHLOROETHYLENE
  name = G4_TETRACHLOROETHYLENE
  specific = 4
FEATURE [App::DocumentObjectGroupPython] Tl_element001  label="Tl_element : 1"  # scripted group (container) (typed FeaturePython)
  n = 1
  ref = Tl_element
FEATURE [App::DocumentObjectGroupPython] Cl_element026  label="Cl_element : 013"  # scripted group (container) (typed FeaturePython)
  n = 1
  ref = Cl_element
FEATURE [App::DocumentObjectGroupPython] G4_THALLIUM_CHLORIDE  # scripted group (container) (typed FeaturePython)
  Dunit = g/cm3
  Dvalue = 7.004
  Group = -> [Tl_element001,Cl_element026]
  conduct = 2
  density = 1
  expand = 3
  formula = G4_THALLIUM_CHLORIDE
  name = G4_THALLIUM_CHLORIDE
  specific = 4
FEATURE [App::DocumentObjectGroupPython] H_element100  label="H_element : 0.147"  # scripted group (container) (typed FeaturePython)
  n = 0.105
FEATURE [App::DocumentObjectGroupPython] C_element110  label="C_element : 0.256"  # scripted group (container) (typed FeaturePython)
  n = 0.256
FEATURE [App::DocumentObjectGroupPython] N_element042  label="N_element : 0.760"  # scripted group (container) (typed FeaturePython)
  n = 0.027
FEATURE [App::DocumentObjectGroupPython] O_element094  label="O_element : 0.602"  # scripted group (container) (typed FeaturePython)
  n = 0.602
FEATURE [App::DocumentObjectGroupPython] Na_element019  label="Na_element : 0.102"  # scripted group (container) (typed FeaturePython)
  n = 0.001
FEATURE [App::DocumentObjectGroupPython] P_element011  label="P_element : 0.109"  # scripted group (container) (typed FeaturePython)
  n = 0.002
FEATURE [App::DocumentObjectGroupPython] S_element022  label="S_element : 0.023"  # scripted group (container) (typed FeaturePython)
  n = 0.003
FEATURE [App::DocumentObjectGroupPython] Cl_element027  label="Cl_element : 0.591"  # scripted group (container) (typed FeaturePython)
  n = 0.002
FEATURE [App::DocumentObjectGroupPython] K_element012  label="K_element : 0.018"  # scripted group (container) (typed FeaturePython)
  n = 0.002
FEATURE [App::DocumentObjectGroupPython] G4_TISSUE_SOFT_ICRP  # scripted group (container) (typed FeaturePython)
  Dunit = g/cm3
  Dvalue = 1.03
  Group = -> [H_element100,C_element110,N_element042,O_element094,Na_element019,P_element011,S_element022,Cl_element027,K_element012]
  conduct = 2
  density = 1
  expand = 3
  formula = G4_TISSUE_SOFT_ICRP
  name = G4_TISSUE_SOFT_ICRP
  specific = 4
FEATURE [App::DocumentObjectGroupPython] H_element101  label="H_element : 0.148"  # scripted group (container) (typed FeaturePython)
  n = 0.101
FEATURE [App::DocumentObjectGroupPython] C_element111  label="C_element : 0.111"  # scripted group (container) (typed FeaturePython)
  n = 0.111
FEATURE [App::DocumentObjectGroupPython] N_element043  label="N_element : 0.026"  # scripted group (container) (typed FeaturePython)
  n = 0.026
FEATURE [App::DocumentObjectGroupPython] O_element095  label="O_element : 0.762"  # scripted group (container) (typed FeaturePython)
  n = 0.762
FEATURE [App::DocumentObjectGroupPython] G4_TISSUE_SOFT_ICRU_4  label="G4_TISSUE_SOFT_ICRU-4"  # scripted group (container) (typed FeaturePython)
  Dunit = g/cm3
  Dvalue = 1
  Group = -> [H_element101,C_element111,N_element043,O_element095]
  conduct = 2
  density = 1
  expand = 3
  formula = G4_TISSUE_SOFT_ICRU-4
  name = G4_TISSUE_SOFT_ICRU-4
  specific = 4
FEATURE [App::DocumentObjectGroupPython] H_element102  label="H_element : 0.149"  # scripted group (container) (typed FeaturePython)
  n = 0.101869
FEATURE [App::DocumentObjectGroupPython] C_element112  label="C_element : 0.456"  # scripted group (container) (typed FeaturePython)
  n = 0.456179
FEATURE [App::DocumentObjectGroupPython] N_element044  label="N_element : 0.761"  # scripted group (container) (typed FeaturePython)
  n = 0.035172
FEATURE [App::DocumentObjectGroupPython] O_element096  label="O_element : 0.407"  # scripted group (container) (typed FeaturePython)
  n = 0.40678
FEATURE [App::DocumentObjectGroupPython] G4_TISSUE_METHANE  label="G4_TISSUE-METHANE"  # scripted group (container) (typed FeaturePython)
  Dunit = g/cm3
  Dvalue = 0.00106409
  Group = -> [H_element102,C_element112,N_element044,O_element096]
  conduct = 2
  density = 1
  expand = 3
  formula = G4_TISSUE-METHANE
  name = G4_TISSUE-METHANE
  specific = 4
FEATURE [App::DocumentObjectGroupPython] H_element103  label="H_element : 0.103"  # scripted group (container) (typed FeaturePython)
  n = 0.102672
FEATURE [App::DocumentObjectGroupPython] C_element113  label="C_element : 0.569"  # scripted group (container) (typed FeaturePython)
  n = 0.56894
FEATURE [App::DocumentObjectGroupPython] N_element045  label="N_element : 0.762"  # scripted group (container) (typed FeaturePython)
  n = 0.035022
FEATURE [App::DocumentObjectGroupPython] O_element097  label="O_element : 0.293"  # scripted group (container) (typed FeaturePython)
  n = 0.293366
FEATURE [App::DocumentObjectGroupPython] G4_TISSUE_PROPANE  label="G4_TISSUE-PROPANE"  # scripted group (container) (typed FeaturePython)
  Dunit = g/cm3
  Dvalue = 0.00182628
  Group = -> [H_element103,C_element113,N_element045,O_element097]
  conduct = 2
  density = 1
  expand = 3
  formula = G4_TISSUE-PROPANE
  name = G4_TISSUE-PROPANE
  specific = 4
FEATURE [App::DocumentObjectGroupPython] Ti_element003  label="Ti_element : 1"  # scripted group (container) (typed FeaturePython)
  n = 1
  ref = Ti_element
FEATURE [App::DocumentObjectGroupPython] O_element098  label="O_element : 052"  # scripted group (container) (typed FeaturePython)
  n = 2
  ref = O_element
FEATURE [App::DocumentObjectGroupPython] G4_TITANIUM_DIOXIDE  # scripted group (container) (typed FeaturePython)
  Dunit = g/cm3
  Dvalue = 4.26
  Group = -> [Ti_element003,O_element098]
  conduct = 2
  density = 1
  expand = 3
  formula = G4_TITANIUM_DIOXIDE
  name = G4_TITANIUM_DIOXIDE
  specific = 4
FEATURE [App::DocumentObjectGroupPython] C_element114  label="C_element : 061"  # scripted group (container) (typed FeaturePython)
  n = 7
  ref = C_element
FEATURE [App::DocumentObjectGroupPython] H_element104  label="H_element : 055"  # scripted group (container) (typed FeaturePython)
  n = 8
  ref = H_element
FEATURE [App::DocumentObjectGroupPython] G4_TOLUENE  # scripted group (container) (typed FeaturePython)
  Dunit = g/cm3
  Dvalue = 0.8669
  Group = -> [C_element114,H_element104]
  conduct = 2
  density = 1
  expand = 3
  formula = G4_TOLUENE
  name = G4_TOLUENE
  specific = 4
FEATURE [App::DocumentObjectGroupPython] C_element115  label="C_element : 062"  # scripted group (container) (typed FeaturePython)
  n = 2
  ref = C_element
FEATURE [App::DocumentObjectGroupPython] H_element105  label="H_element : 056"  # scripted group (container) (typed FeaturePython)
  n = 1
  ref = H_element
FEATURE [App::DocumentObjectGroupPython] Cl_element028  label="Cl_element : 014"  # scripted group (container) (typed FeaturePython)
  n = 3
  ref = Cl_element
FEATURE [App::DocumentObjectGroupPython] G4_TRICHLOROETHYLENE  # scripted group (container) (typed FeaturePython)
  Dunit = g/cm3
  Dvalue = 1.46
  Group = -> [C_element115,H_element105,Cl_element028]
  conduct = 2
  density = 1
  expand = 3
  formula = G4_TRICHLOROETHYLENE
  name = G4_TRICHLOROETHYLENE
  specific = 4
FEATURE [App::DocumentObjectGroupPython] C_element116  label="C_element : 063"  # scripted group (container) (typed FeaturePython)
  n = 6
  ref = C_element
FEATURE [App::DocumentObjectGroupPython] H_element106  label="H_element : 15"  # scripted group (container) (typed FeaturePython)
  n = 15
  ref = H_element
FEATURE [App::DocumentObjectGroupPython] O_element099  label="O_element : 053"  # scripted group (container) (typed FeaturePython)
  n = 4
  ref = O_element
FEATURE [App::DocumentObjectGroupPython] P_element012  label="P_element : 1"  # scripted group (container) (typed FeaturePython)
  n = 1
  ref = P_element
FEATURE [App::DocumentObjectGroupPython] G4_TRIETHYL_PHOSPHATE  # scripted group (container) (typed FeaturePython)
  Dunit = g/cm3
  Dvalue = 1.07
  Group = -> [C_element116,H_element106,O_element099,P_element012]
  conduct = 2
  density = 1
  expand = 3
  formula = G4_TRIETHYL_PHOSPHATE
  name = G4_TRIETHYL_PHOSPHATE
  specific = 4
FEATURE [App::DocumentObjectGroupPython] W_element003  label="W_element : 003"  # scripted group (container) (typed FeaturePython)
  n = 1
  ref = W_element
FEATURE [App::DocumentObjectGroupPython] F_element017  label="F_element : 6"  # scripted group (container) (typed FeaturePython)
  n = 6
  ref = F_element
FEATURE [App::DocumentObjectGroupPython] G4_TUNGSTEN_HEXAFLUORIDE  # scripted group (container) (typed FeaturePython)
  Dunit = g/cm3
  Dvalue = 2.4
  Group = -> [W_element003,F_element017]
  conduct = 2
  density = 1
  expand = 3
  formula = G4_TUNGSTEN_HEXAFLUORIDE
  name = G4_TUNGSTEN_HEXAFLUORIDE
  specific = 4
FEATURE [App::DocumentObjectGroupPython] U_element001  label="U_element : 1"  # scripted group (container) (typed FeaturePython)
  n = 1
  ref = U_element
FEATURE [App::DocumentObjectGroupPython] C_element117  label="C_element : 064"  # scripted group (container) (typed FeaturePython)
  n = 2
  ref = C_element
FEATURE [App::DocumentObjectGroupPython] G4_URANIUM_DICARBIDE  # scripted group (container) (typed FeaturePython)
  Dunit = g/cm3
  Dvalue = 11.28
  Group = -> [U_element001,C_element117]
  conduct = 2
  density = 1
  expand = 3
  formula = G4_URANIUM_DICARBIDE
  name = G4_URANIUM_DICARBIDE
  specific = 4
FEATURE [App::DocumentObjectGroupPython] U_element002  label="U_element : 002"  # scripted group (container) (typed FeaturePython)
  n = 1
  ref = U_element
FEATURE [App::DocumentObjectGroupPython] C_element118  label="C_element : 065"  # scripted group (container) (typed FeaturePython)
  n = 1
  ref = C_element
FEATURE [App::DocumentObjectGroupPython] G4_URANIUM_MONOCARBIDE  # scripted group (container) (typed FeaturePython)
  Dunit = g/cm3
  Dvalue = 13.63
  Group = -> [U_element002,C_element118]
  conduct = 2
  density = 1
  expand = 3
  formula = G4_URANIUM_MONOCARBIDE
  name = G4_URANIUM_MONOCARBIDE
  specific = 4
FEATURE [App::DocumentObjectGroupPython] U_element003  label="U_element : 003"  # scripted group (container) (typed FeaturePython)
  n = 1
  ref = U_element
FEATURE [App::DocumentObjectGroupPython] O_element100  label="O_element : 054"  # scripted group (container) (typed FeaturePython)
  n = 2
  ref = O_element
FEATURE [App::DocumentObjectGroupPython] G4_URANIUM_OXIDE  # scripted group (container) (typed FeaturePython)
  Dunit = g/cm3
  Dvalue = 10.96
  Group = -> [U_element003,O_element100]
  conduct = 2
  density = 1
  expand = 3
  formula = G4_URANIUM_OXIDE
  name = G4_URANIUM_OXIDE
  specific = 4
FEATURE [App::DocumentObjectGroupPython] C_element119  label="C_element : 066"  # scripted group (container) (typed FeaturePython)
  n = 1
  ref = C_element
FEATURE [App::DocumentObjectGroupPython] H_element107  label="H_element : 057"  # scripted group (container) (typed FeaturePython)
  n = 4
  ref = H_element
FEATURE [App::DocumentObjectGroupPython] N_element046  label="N_element : 019"  # scripted group (container) (typed FeaturePython)
  n = 2
  ref = N_element
FEATURE [App::DocumentObjectGroupPython] O_element101  label="O_element : 055"  # scripted group (container) (typed FeaturePython)
  n = 1
  ref = O_element
FEATURE [App::DocumentObjectGroupPython] G4_UREA  # scripted group (container) (typed FeaturePython)
  Dunit = g/cm3
  Dvalue = 1.323
  Group = -> [C_element119,H_element107,N_element046,O_element101]
  conduct = 2
  density = 1
  expand = 3
  formula = G4_UREA
  name = G4_UREA
  specific = 4
FEATURE [App::DocumentObjectGroupPython] C_element120  label="C_element : 067"  # scripted group (container) (typed FeaturePython)
  n = 5
  ref = C_element
FEATURE [App::DocumentObjectGroupPython] H_element108  label="H_element : 058"  # scripted group (container) (typed FeaturePython)
  n = 11
  ref = H_element
FEATURE [App::DocumentObjectGroupPython] N_element047  label="N_element : 020"  # scripted group (container) (typed FeaturePython)
  n = 1
  ref = N_element
FEATURE [App::DocumentObjectGroupPython] O_element102  label="O_element : 056"  # scripted group (container) (typed FeaturePython)
  n = 2
  ref = O_element
FEATURE [App::DocumentObjectGroupPython] G4_VALINE  # scripted group (container) (typed FeaturePython)
  Dunit = g/cm3
  Dvalue = 1.23
  Group = -> [C_element120,H_element108,N_element047,O_element102]
  conduct = 2
  density = 1
  expand = 3
  formula = G4_VALINE
  name = G4_VALINE
  specific = 4
FEATURE [App::DocumentObjectGroupPython] H_element109  label="H_element : 0.009"  # scripted group (container) (typed FeaturePython)
  n = 0.009417
FEATURE [App::DocumentObjectGroupPython] C_element121  label="C_element : 0.281"  # scripted group (container) (typed FeaturePython)
  n = 0.280555
FEATURE [App::DocumentObjectGroupPython] F_element018  label="F_element : 0.710"  # scripted group (container) (typed FeaturePython)
  n = 0.710028
FEATURE [App::DocumentObjectGroupPython] G4_VITON  # scripted group (container) (typed FeaturePython)
  Dunit = g/cm3
  Dvalue = 1.8
  Group = -> [H_element109,C_element121,F_element018]
  conduct = 2
  density = 1
  expand = 3
  formula = G4_VITON
  name = G4_VITON
  specific = 4
FEATURE [App::DocumentObjectGroupPython] H_element110  label="H_element : 059"  # scripted group (container) (typed FeaturePython)
  n = 2
  ref = H_element
FEATURE [App::DocumentObjectGroupPython] O_element103  label="O_element : 057"  # scripted group (container) (typed FeaturePython)
  n = 1
  ref = O_element
FEATURE [App::DocumentObjectGroupPython] G4_WATER  # scripted group (container) (typed FeaturePython)
  Dunit = g/cm3
  Dvalue = 1
  Group = -> [H_element110,O_element103]
  conduct = 2
  density = 1
  expand = 3
  formula = G4_WATER
  name = G4_WATER
  specific = 4
FEATURE [App::DocumentObjectGroupPython] H_element111  label="H_element : 060"  # scripted group (container) (typed FeaturePython)
  n = 2
  ref = H_element
FEATURE [App::DocumentObjectGroupPython] O_element104  label="O_element : 058"  # scripted group (container) (typed FeaturePython)
  n = 1
  ref = O_element
FEATURE [App::DocumentObjectGroupPython] G4_WATER_VAPOR  # scripted group (container) (typed FeaturePython)
  Dunit = g/cm3
  Dvalue = 0.000756182
  Group = -> [H_element111,O_element104]
  conduct = 2
  density = 1
  expand = 3
  formula = G4_WATER_VAPOR
  name = G4_WATER_VAPOR
  specific = 4
FEATURE [App::DocumentObjectGroupPython] C_element122  label="C_element : 068"  # scripted group (container) (typed FeaturePython)
  n = 8
  ref = C_element
FEATURE [App::DocumentObjectGroupPython] H_element112  label="H_element : 061"  # scripted group (container) (typed FeaturePython)
  n = 10
  ref = H_element
FEATURE [App::DocumentObjectGroupPython] G4_XYLENE  # scripted group (container) (typed FeaturePython)
  Dunit = g/cm3
  Dvalue = 0.87
  Group = -> [C_element122,H_element112]
  conduct = 2
  density = 1
  expand = 3
  formula = G4_XYLENE
  name = G4_XYLENE
  specific = 4
FEATURE [App::DocumentObjectGroupPython] C_element123  label="C_element : 069"  # scripted group (container) (typed FeaturePython)
  n = 1
  ref = C_element
FEATURE [App::DocumentObjectGroupPython] G4_GRAPHITE  # scripted group (container) (typed FeaturePython)
  Dunit = g/cm3
  Dvalue = 2.21
  Group = -> [C_element123]
  conduct = 2
  density = 1
  expand = 3
  formula = G4_GRAPHITE
  name = G4_GRAPHITE
  specific = 4
FEATURE [App::DocumentObjectGroupPython] NIST  # scripted group (container) (typed FeaturePython)
  Group = -> [G4_A_150_TISSUE,G4_ACETONE,G4_ACETYLENE,G4_ADENINE,G4_ADIPOSE_TISSUE_ICRP,G4_AIR,G4_ALANINE,G4_ALUMINUM_OXIDE,G4_AMBER,G4_AMMONIA,G4_ANILINE,G4_ANTHRACENE,G4_B_100_BONE,G4_BAKELITE,G4_BARIUM_FLUORIDE,G4_BARIUM_SULFATE,G4_BENZENE,G4_BERYLLIUM_OXIDE,G4_BGO,G4_BLOOD_ICRP,G4_BONE_COMPACT_ICRU,G4_BONE_CORTICAL_ICRP,G4_BORON_CARBIDE,G4_BORON_OXIDE,G4_BRAIN_ICRP,G4_BUTANE,G4_N_BUTYL_ALCOHOL,G4_C_552,+152 more]
FEATURE [App::DocumentObjectGroupPython] H_element113  label="H_element : 062"  # scripted group (container) (typed FeaturePython)
  n = 1
  ref = H_element
FEATURE [App::DocumentObjectGroupPython] G4_H  # scripted group (container) (typed FeaturePython)
  Dunit = g/cm3
  Dvalue = 8.3748e-05
  Group = -> [H_element113]
  conduct = 2
  density = 1
  expand = 3
  formula = H
  name = G4_H
  specific = 4
FEATURE [App::DocumentObjectGroupPython] He_element001  label="He_element : 1"  # scripted group (container) (typed FeaturePython)
  n = 1
  ref = He_element
FEATURE [App::DocumentObjectGroupPython] G4_He  # scripted group (container) (typed FeaturePython)
  Dunit = g/cm3
  Dvalue = 0.000166322
  Group = -> [He_element001]
  conduct = 2
  density = 1
  expand = 3
  formula = He
  name = G4_He
  specific = 4
FEATURE [App::DocumentObjectGroupPython] Li_element008  label="Li_element : 008"  # scripted group (container) (typed FeaturePython)
  n = 1
  ref = Li_element
FEATURE [App::DocumentObjectGroupPython] G4_Li  # scripted group (container) (typed FeaturePython)
  Dunit = g/cm3
  Dvalue = 0.534
  Group = -> [Li_element008]
  conduct = 2
  density = 1
  expand = 3
  formula = Li
  name = G4_Li
  specific = 4
FEATURE [App::DocumentObjectGroupPython] Be_element002  label="Be_element : 002"  # scripted group (container) (typed FeaturePython)
  n = 1
  ref = Be_element
FEATURE [App::DocumentObjectGroupPython] G4_Be  # scripted group (container) (typed FeaturePython)
  Dunit = g/cm3
  Dvalue = 1.848
  Group = -> [Be_element002]
  conduct = 2
  density = 1
  expand = 3
  formula = Be
  name = G4_Be
  specific = 4
FEATURE [App::DocumentObjectGroupPython] B_element007  label="B_element : 007"  # scripted group (container) (typed FeaturePython)
  n = 1
  ref = B_element
FEATURE [App::DocumentObjectGroupPython] G4_B  # scripted group (container) (typed FeaturePython)
  Dunit = g/cm3
  Dvalue = 2.37
  Group = -> [B_element007]
  conduct = 2
  density = 1
  expand = 3
  formula = B
  name = G4_B
  specific = 4
FEATURE [App::DocumentObjectGroupPython] C_element124  label="C_element : 070"  # scripted group (container) (typed FeaturePython)
  n = 1
  ref = C_element
FEATURE [App::DocumentObjectGroupPython] G4_C  # scripted group (container) (typed FeaturePython)
  Dunit = g/cm3
  Dvalue = 2
  Group = -> [C_element124]
  conduct = 2
  density = 1
  expand = 3
  formula = C
  name = G4_C
  specific = 4
FEATURE [App::DocumentObjectGroupPython] N_element048  label="N_element : 021"  # scripted group (container) (typed FeaturePython)
  n = 1
  ref = N_element
FEATURE [App::DocumentObjectGroupPython] G4_N  # scripted group (container) (typed FeaturePython)
  Dunit = g/cm3
  Dvalue = 0.0011652
  Group = -> [N_element048]
  conduct = 2
  density = 1
  expand = 3
  formula = N
  name = G4_N
  specific = 4
FEATURE [App::DocumentObjectGroupPython] O_element105  label="O_element : 059"  # scripted group (container) (typed FeaturePython)
  n = 1
  ref = O_element
FEATURE [App::DocumentObjectGroupPython] G4_O  # scripted group (container) (typed FeaturePython)
  Dunit = g/cm3
  Dvalue = 0.00133151
  Group = -> [O_element105]
  conduct = 2
  density = 1
  expand = 3
  formula = O
  name = G4_O
  specific = 4
FEATURE [App::DocumentObjectGroupPython] F_element019  label="F_element : 008"  # scripted group (container) (typed FeaturePython)
  n = 1
  ref = F_element
FEATURE [App::DocumentObjectGroupPython] G4_F  # scripted group (container) (typed FeaturePython)
  Dunit = g/cm3
  Dvalue = 0.00158029
  Group = -> [F_element019]
  conduct = 2
  density = 1
  expand = 3
  formula = F
  name = G4_F
  specific = 4
FEATURE [App::DocumentObjectGroupPython] Ne_element001  label="Ne_element : 1"  # scripted group (container) (typed FeaturePython)
  n = 1
  ref = Ne_element
FEATURE [App::DocumentObjectGroupPython] G4_Ne  # scripted group (container) (typed FeaturePython)
  Dunit = g/cm3
  Dvalue = 0.000838505
  Group = -> [Ne_element001]
  conduct = 2
  density = 1
  expand = 3
  formula = Ne
  name = G4_Ne
  specific = 4
FEATURE [App::DocumentObjectGroupPython] Na_element020  label="Na_element : 005"  # scripted group (container) (typed FeaturePython)
  n = 1
  ref = Na_element
FEATURE [App::DocumentObjectGroupPython] G4_Na  # scripted group (container) (typed FeaturePython)
  Dunit = g/cm3
  Dvalue = 0.971
  Group = -> [Na_element020]
  conduct = 2
  density = 1
  expand = 3
  formula = Na
  name = G4_Na
  specific = 4
FEATURE [App::DocumentObjectGroupPython] Mg_element011  label="Mg_element : 005"  # scripted group (container) (typed FeaturePython)
  n = 1
  ref = Mg_element
FEATURE [App::DocumentObjectGroupPython] G4_Mg  # scripted group (container) (typed FeaturePython)
  Dunit = g/cm3
  Dvalue = 1.74
  Group = -> [Mg_element011]
  conduct = 2
  density = 1
  expand = 3
  formula = Mg
  name = G4_Mg
  specific = 4
FEATURE [App::DocumentObjectGroupPython] Al_element004  label="Al_element : 1"  # scripted group (container) (typed FeaturePython)
  n = 1
  ref = Al_element
FEATURE [App::DocumentObjectGroupPython] G4_Al  # scripted group (container) (typed FeaturePython)
  Dunit = g/cm3
  Dvalue = 2.699
  Group = -> [Al_element004]
  conduct = 2
  density = 1
  expand = 3
  formula = Al
  name = G4_Al
  specific = 4
FEATURE [App::DocumentObjectGroupPython] Si_element007  label="Si_element : 002"  # scripted group (container) (typed FeaturePython)
  n = 1
  ref = Si_element
FEATURE [App::DocumentObjectGroupPython] G4_Si  # scripted group (container) (typed FeaturePython)
  Dunit = g/cm3
  Dvalue = 2.33
  Group = -> [Si_element007]
  conduct = 2
  density = 1
  expand = 3
  formula = Si
  name = G4_Si
  specific = 4
FEATURE [App::DocumentObjectGroupPython] P_element013  label="P_element : 002"  # scripted group (container) (typed FeaturePython)
  n = 1
  ref = P_element
FEATURE [App::DocumentObjectGroupPython] G4_P  # scripted group (container) (typed FeaturePython)
  Dunit = g/cm3
  Dvalue = 2.2
  Group = -> [P_element013]
  conduct = 2
  density = 1
  expand = 3
  formula = P
  name = G4_P
  specific = 4
FEATURE [App::DocumentObjectGroupPython] S_element023  label="S_element : 007"  # scripted group (container) (typed FeaturePython)
  n = 1
  ref = S_element
FEATURE [App::DocumentObjectGroupPython] G4_S  # scripted group (container) (typed FeaturePython)
  Dunit = g/cm3
  Dvalue = 2
  Group = -> [S_element023]
  conduct = 2
  density = 1
  expand = 3
  formula = S
  name = G4_S
  specific = 4
FEATURE [App::DocumentObjectGroupPython] Cl_element029  label="Cl_element : 015"  # scripted group (container) (typed FeaturePython)
  n = 1
  ref = Cl_element
FEATURE [App::DocumentObjectGroupPython] G4_Cl  # scripted group (container) (typed FeaturePython)
  Dunit = g/cm3
  Dvalue = 0.00299473
  Group = -> [Cl_element029]
  conduct = 2
  density = 1
  expand = 3
  formula = Cl
  name = G4_Cl
  specific = 4
FEATURE [App::DocumentObjectGroupPython] Ar_element002  label="Ar_element : 1"  # scripted group (container) (typed FeaturePython)
  n = 1
  ref = Ar_element
FEATURE [App::DocumentObjectGroupPython] G4_Ar  # scripted group (container) (typed FeaturePython)
  Dunit = g/cm3
  Dvalue = 0.00166201
  Group = -> [Ar_element002]
  conduct = 2
  density = 1
  expand = 3
  formula = Ar
  name = G4_Ar
  specific = 4
FEATURE [App::DocumentObjectGroupPython] K_element013  label="K_element : 003"  # scripted group (container) (typed FeaturePython)
  n = 1
  ref = K_element
FEATURE [App::DocumentObjectGroupPython] G4_K  # scripted group (container) (typed FeaturePython)
  Dunit = g/cm3
  Dvalue = 0.862
  Group = -> [K_element013]
  conduct = 2
  density = 1
  expand = 3
  formula = K
  name = G4_K
  specific = 4
FEATURE [App::DocumentObjectGroupPython] Ca_element014  label="Ca_element : 007"  # scripted group (container) (typed FeaturePython)
  n = 1
  ref = Ca_element
FEATURE [App::DocumentObjectGroupPython] G4_Ca  # scripted group (container) (typed FeaturePython)
  Dunit = g/cm3
  Dvalue = 1.55
  Group = -> [Ca_element014]
  conduct = 2
  density = 1
  expand = 3
  formula = Ca
  name = G4_Ca
  specific = 4
FEATURE [App::DocumentObjectGroupPython] Sc_element001  label="Sc_element : 1"  # scripted group (container) (typed FeaturePython)
  n = 1
  ref = Sc_element
FEATURE [App::DocumentObjectGroupPython] G4_Sc  # scripted group (container) (typed FeaturePython)
  Dunit = g/cm3
  Dvalue = 2.989
  Group = -> [Sc_element001]
  conduct = 2
  density = 1
  expand = 3
  formula = Sc
  name = G4_Sc
  specific = 4
FEATURE [App::DocumentObjectGroupPython] Ti_element004  label="Ti_element : 002"  # scripted group (container) (typed FeaturePython)
  n = 1
  ref = Ti_element
FEATURE [App::DocumentObjectGroupPython] G4_Ti  # scripted group (container) (typed FeaturePython)
  Dunit = g/cm3
  Dvalue = 4.54
  Group = -> [Ti_element004]
  conduct = 2
  density = 1
  expand = 3
  formula = Ti
  name = G4_Ti
  specific = 4
FEATURE [App::DocumentObjectGroupPython] V_element001  label="V_element : 1"  # scripted group (container) (typed FeaturePython)
  n = 1
  ref = V_element
FEATURE [App::DocumentObjectGroupPython] G4_V  # scripted group (container) (typed FeaturePython)
  Dunit = g/cm3
  Dvalue = 6.11
  Group = -> [V_element001]
  conduct = 2
  density = 1
  expand = 3
  formula = V
  name = G4_V
  specific = 4
FEATURE [App::DocumentObjectGroupPython] Cr_element001  label="Cr_element : 1"  # scripted group (container) (typed FeaturePython)
  n = 1
  ref = Cr_element
FEATURE [App::DocumentObjectGroupPython] G4_Cr  # scripted group (container) (typed FeaturePython)
  Dunit = g/cm3
  Dvalue = 7.18
  Group = -> [Cr_element001]
  conduct = 2
  density = 1
  expand = 3
  formula = Cr
  name = G4_Cr
  specific = 4
FEATURE [App::DocumentObjectGroupPython] Mn_element001  label="Mn_element : 1"  # scripted group (container) (typed FeaturePython)
  n = 1
  ref = Mn_element
FEATURE [App::DocumentObjectGroupPython] G4_Mn  # scripted group (container) (typed FeaturePython)
  Dunit = g/cm3
  Dvalue = 7.44
  Group = -> [Mn_element001]
  conduct = 2
  density = 1
  expand = 3
  formula = Mn
  name = G4_Mn
  specific = 4
FEATURE [App::DocumentObjectGroupPython] Fe_element007  label="Fe_element : 004"  # scripted group (container) (typed FeaturePython)
  n = 1
  ref = Fe_element
FEATURE [App::DocumentObjectGroupPython] G4_Fe  # scripted group (container) (typed FeaturePython)
  Dunit = g/cm3
  Dvalue = 7.874
  Group = -> [Fe_element007]
  conduct = 2
  density = 1
  expand = 3
  formula = Fe
  name = G4_Fe
  specific = 4
FEATURE [App::DocumentObjectGroupPython] Co_element001  label="Co_element : 1"  # scripted group (container) (typed FeaturePython)
  n = 1
  ref = Co_element
FEATURE [App::DocumentObjectGroupPython] G4_Co  # scripted group (container) (typed FeaturePython)
  Dunit = g/cm3
  Dvalue = 8.9
  Group = -> [Co_element001]
  conduct = 2
  density = 1
  expand = 3
  formula = Co
  name = G4_Co
  specific = 4
FEATURE [App::DocumentObjectGroupPython] Ni_element001  label="Ni_element : 1"  # scripted group (container) (typed FeaturePython)
  n = 1
  ref = Ni_element
FEATURE [App::DocumentObjectGroupPython] G4_Ni  # scripted group (container) (typed FeaturePython)
  Dunit = g/cm3
  Dvalue = 8.902
  Group = -> [Ni_element001]
  conduct = 2
  density = 1
  expand = 3
  formula = Ni
  name = G4_Ni
  specific = 4
FEATURE [App::DocumentObjectGroupPython] Cu_element001  label="Cu_element : 1"  # scripted group (container) (typed FeaturePython)
  n = 1
  ref = Cu_element
FEATURE [App::DocumentObjectGroupPython] G4_Cu  # scripted group (container) (typed FeaturePython)
  Dunit = g/cm3
  Dvalue = 8.96
  Group = -> [Cu_element001]
  conduct = 2
  density = 1
  expand = 3
  formula = Cu
  name = G4_Cu
  specific = 4
FEATURE [App::DocumentObjectGroupPython] Zn_element001  label="Zn_element : 1"  # scripted group (container) (typed FeaturePython)
  n = 1
  ref = Zn_element
FEATURE [App::DocumentObjectGroupPython] G4_Zn  # scripted group (container) (typed FeaturePython)
  Dunit = g/cm3
  Dvalue = 7.133
  Group = -> [Zn_element001]
  conduct = 2
  density = 1
  expand = 3
  formula = Zn
  name = G4_Zn
  specific = 4
FEATURE [App::DocumentObjectGroupPython] Ga_element002  label="Ga_element : 002"  # scripted group (container) (typed FeaturePython)
  n = 1
  ref = Ga_element
FEATURE [App::DocumentObjectGroupPython] G4_Ga  # scripted group (container) (typed FeaturePython)
  Dunit = g/cm3
  Dvalue = 5.904
  Group = -> [Ga_element002]
  conduct = 2
  density = 1
  expand = 3
  formula = Ga
  name = G4_Ga
  specific = 4
FEATURE [App::DocumentObjectGroupPython] Ge_element002  label="Ge_element : 1"  # scripted group (container) (typed FeaturePython)
  n = 1
  ref = Ge_element
FEATURE [App::DocumentObjectGroupPython] G4_Ge  # scripted group (container) (typed FeaturePython)
  Dunit = g/cm3
  Dvalue = 5.323
  Group = -> [Ge_element002]
  conduct = 2
  density = 1
  expand = 3
  formula = Ge
  name = G4_Ge
  specific = 4
FEATURE [App::DocumentObjectGroupPython] As_element003  label="As_element : 002"  # scripted group (container) (typed FeaturePython)
  n = 1
  ref = As_element
FEATURE [App::DocumentObjectGroupPython] G4_As  # scripted group (container) (typed FeaturePython)
  Dunit = g/cm3
  Dvalue = 5.73
  Group = -> [As_element003]
  conduct = 2
  density = 1
  expand = 3
  formula = As
  name = G4_As
  specific = 4
FEATURE [App::DocumentObjectGroupPython] Se_element001  label="Se_element : 1"  # scripted group (container) (typed FeaturePython)
  n = 1
  ref = Se_element
FEATURE [App::DocumentObjectGroupPython] G4_Se  # scripted group (container) (typed FeaturePython)
  Dunit = g/cm3
  Dvalue = 4.5
  Group = -> [Se_element001]
  conduct = 2
  density = 1
  expand = 3
  formula = Se
  name = G4_Se
  specific = 4
FEATURE [App::DocumentObjectGroupPython] Br_element007  label="Br_element : 004"  # scripted group (container) (typed FeaturePython)
  n = 1
  ref = Br_element
FEATURE [App::DocumentObjectGroupPython] G4_Br  # scripted group (container) (typed FeaturePython)
  Dunit = g/cm3
  Dvalue = 0.0070721
  Group = -> [Br_element007]
  conduct = 2
  density = 1
  expand = 3
  formula = Br
  name = G4_Br
  specific = 4
FEATURE [App::DocumentObjectGroupPython] Kr_element001  label="Kr_element : 1"  # scripted group (container) (typed FeaturePython)
  n = 1
  ref = Kr_element
FEATURE [App::DocumentObjectGroupPython] G4_Kr  # scripted group (container) (typed FeaturePython)
  Dunit = g/cm3
  Dvalue = 0.00347832
  Group = -> [Kr_element001]
  conduct = 2
  density = 1
  expand = 3
  formula = Kr
  name = G4_Kr
  specific = 4
FEATURE [App::DocumentObjectGroupPython] Rb_element001  label="Rb_element : 1"  # scripted group (container) (typed FeaturePython)
  n = 1
  ref = Rb_element
FEATURE [App::DocumentObjectGroupPython] G4_Rb  # scripted group (container) (typed FeaturePython)
  Dunit = g/cm3
  Dvalue = 1.532
  Group = -> [Rb_element001]
  conduct = 2
  density = 1
  expand = 3
  formula = Rb
  name = G4_Rb
  specific = 4
FEATURE [App::DocumentObjectGroupPython] Sr_element001  label="Sr_element : 1"  # scripted group (container) (typed FeaturePython)
  n = 1
  ref = Sr_element
FEATURE [App::DocumentObjectGroupPython] G4_Sr  # scripted group (container) (typed FeaturePython)
  Dunit = g/cm3
  Dvalue = 2.54
  Group = -> [Sr_element001]
  conduct = 2
  density = 1
  expand = 3
  formula = Sr
  name = G4_Sr
  specific = 4
FEATURE [App::DocumentObjectGroupPython] Y_element001  label="Y_element : 1"  # scripted group (container) (typed FeaturePython)
  n = 1
  ref = Y_element
FEATURE [App::DocumentObjectGroupPython] G4_Y  # scripted group (container) (typed FeaturePython)
  Dunit = g/cm3
  Dvalue = 4.469
  Group = -> [Y_element001]
  conduct = 2
  density = 1
  expand = 3
  formula = Y
  name = G4_Y
  specific = 4
FEATURE [App::DocumentObjectGroupPython] Zr_element001  label="Zr_element : 1"  # scripted group (container) (typed FeaturePython)
  n = 1
  ref = Zr_element
FEATURE [App::DocumentObjectGroupPython] G4_Zr  # scripted group (container) (typed FeaturePython)
  Dunit = g/cm3
  Dvalue = 6.506
  Group = -> [Zr_element001]
  conduct = 2
  density = 1
  expand = 3
  formula = Zr
  name = G4_Zr
  specific = 4
FEATURE [App::DocumentObjectGroupPython] Nb_element001  label="Nb_element : 1"  # scripted group (container) (typed FeaturePython)
  n = 1
  ref = Nb_element
FEATURE [App::DocumentObjectGroupPython] G4_Nb  # scripted group (container) (typed FeaturePython)
  Dunit = g/cm3
  Dvalue = 8.57
  Group = -> [Nb_element001]
  conduct = 2
  density = 1
  expand = 3
  formula = Nb
  name = G4_Nb
  specific = 4
FEATURE [App::DocumentObjectGroupPython] Mo_element001  label="Mo_element : 1"  # scripted group (container) (typed FeaturePython)
  n = 1
  ref = Mo_element
FEATURE [App::DocumentObjectGroupPython] G4_Mo  # scripted group (container) (typed FeaturePython)
  Dunit = g/cm3
  Dvalue = 10.22
  Group = -> [Mo_element001]
  conduct = 2
  density = 1
  expand = 3
  formula = Mo
  name = G4_Mo
  specific = 4
FEATURE [App::DocumentObjectGroupPython] Tc_element001  label="Tc_element : 1"  # scripted group (container) (typed FeaturePython)
  n = 1
  ref = Tc_element
FEATURE [App::DocumentObjectGroupPython] G4_Tc  # scripted group (container) (typed FeaturePython)
  Dunit = g/cm3
  Dvalue = 11.5
  Group = -> [Tc_element001]
  conduct = 2
  density = 1
  expand = 3
  formula = Tc
  name = G4_Tc
  specific = 4
FEATURE [App::DocumentObjectGroupPython] Ru_element001  label="Ru_element : 1"  # scripted group (container) (typed FeaturePython)
  n = 1
  ref = Ru_element
FEATURE [App::DocumentObjectGroupPython] G4_Ru  # scripted group (container) (typed FeaturePython)
  Dunit = g/cm3
  Dvalue = 12.41
  Group = -> [Ru_element001]
  conduct = 2
  density = 1
  expand = 3
  formula = Ru
  name = G4_Ru
  specific = 4
FEATURE [App::DocumentObjectGroupPython] Rh_element001  label="Rh_element : 1"  # scripted group (container) (typed FeaturePython)
  n = 1
  ref = Rh_element
FEATURE [App::DocumentObjectGroupPython] G4_Rh  # scripted group (container) (typed FeaturePython)
  Dunit = g/cm3
  Dvalue = 12.41
  Group = -> [Rh_element001]
  conduct = 2
  density = 1
  expand = 3
  formula = Rh
  name = G4_Rh
  specific = 4
FEATURE [App::DocumentObjectGroupPython] Pd_element001  label="Pd_element : 1"  # scripted group (container) (typed FeaturePython)
  n = 1
  ref = Pd_element
FEATURE [App::DocumentObjectGroupPython] G4_Pd  # scripted group (container) (typed FeaturePython)
  Dunit = g/cm3
  Dvalue = 12.02
  Group = -> [Pd_element001]
  conduct = 2
  density = 1
  expand = 3
  formula = Pd
  name = G4_Pd
  specific = 4
FEATURE [App::DocumentObjectGroupPython] Ag_element006  label="Ag_element : 004"  # scripted group (container) (typed FeaturePython)
  n = 1
  ref = Ag_element
FEATURE [App::DocumentObjectGroupPython] G4_Ag  # scripted group (container) (typed FeaturePython)
  Dunit = g/cm3
  Dvalue = 10.5
  Group = -> [Ag_element006]
  conduct = 2
  density = 1
  expand = 3
  formula = Ag
  name = G4_Ag
  specific = 4
FEATURE [App::DocumentObjectGroupPython] Cd_element003  label="Cd_element : 003"  # scripted group (container) (typed FeaturePython)
  n = 1
  ref = Cd_element
FEATURE [App::DocumentObjectGroupPython] G4_Cd  # scripted group (container) (typed FeaturePython)
  Dunit = g/cm3
  Dvalue = 8.65
  Group = -> [Cd_element003]
  conduct = 2
  density = 1
  expand = 3
  formula = Cd
  name = G4_Cd
  specific = 4
FEATURE [App::DocumentObjectGroupPython] In_element001  label="In_element : 1"  # scripted group (container) (typed FeaturePython)
  n = 1
  ref = In_element
FEATURE [App::DocumentObjectGroupPython] G4_In  # scripted group (container) (typed FeaturePython)
  Dunit = g/cm3
  Dvalue = 7.31
  Group = -> [In_element001]
  conduct = 2
  density = 1
  expand = 3
  formula = In
  name = G4_In
  specific = 4
FEATURE [App::DocumentObjectGroupPython] Sn_element001  label="Sn_element : 1"  # scripted group (container) (typed FeaturePython)
  n = 1
  ref = Sn_element
FEATURE [App::DocumentObjectGroupPython] G4_Sn  # scripted group (container) (typed FeaturePython)
  Dunit = g/cm3
  Dvalue = 7.31
  Group = -> [Sn_element001]
  conduct = 2
  density = 1
  expand = 3
  formula = Sn
  name = G4_Sn
  specific = 4
FEATURE [App::DocumentObjectGroupPython] Sb_element001  label="Sb_element : 1"  # scripted group (container) (typed FeaturePython)
  n = 1
  ref = Sb_element
FEATURE [App::DocumentObjectGroupPython] G4_Sb  # scripted group (container) (typed FeaturePython)
  Dunit = g/cm3
  Dvalue = 6.691
  Group = -> [Sb_element001]
  conduct = 2
  density = 1
  expand = 3
  formula = Sb
  name = G4_Sb
  specific = 4
FEATURE [App::DocumentObjectGroupPython] Te_element002  label="Te_element : 002"  # scripted group (container) (typed FeaturePython)
  n = 1
  ref = Te_element
FEATURE [App::DocumentObjectGroupPython] G4_Te  # scripted group (container) (typed FeaturePython)
  Dunit = g/cm3
  Dvalue = 6.24
  Group = -> [Te_element002]
  conduct = 2
  density = 1
  expand = 3
  formula = Te
  name = G4_Te
  specific = 4
FEATURE [App::DocumentObjectGroupPython] I_element010  label="I_element : 006"  # scripted group (container) (typed FeaturePython)
  n = 1
  ref = I_element
FEATURE [App::DocumentObjectGroupPython] G4_I  # scripted group (container) (typed FeaturePython)
  Dunit = g/cm3
  Dvalue = 4.93
  Group = -> [I_element010]
  conduct = 2
  density = 1
  expand = 3
  formula = I
  name = G4_I
  specific = 4
FEATURE [App::DocumentObjectGroupPython] Xe_element001  label="Xe_element : 1"  # scripted group (container) (typed FeaturePython)
  n = 1
  ref = Xe_element
FEATURE [App::DocumentObjectGroupPython] G4_Xe  # scripted group (container) (typed FeaturePython)
  Dunit = g/cm3
  Dvalue = 0.00548536
  Group = -> [Xe_element001]
  conduct = 2
  density = 1
  expand = 3
  formula = Xe
  name = G4_Xe
  specific = 4
FEATURE [App::DocumentObjectGroupPython] Cs_element003  label="Cs_element : 003"  # scripted group (container) (typed FeaturePython)
  n = 1
  ref = Cs_element
FEATURE [App::DocumentObjectGroupPython] G4_Cs  # scripted group (container) (typed FeaturePython)
  Dunit = g/cm3
  Dvalue = 1.873
  Group = -> [Cs_element003]
  conduct = 2
  density = 1
  expand = 3
  formula = Cs
  name = G4_Cs
  specific = 4
FEATURE [App::DocumentObjectGroupPython] Ba_element003  label="Ba_element : 003"  # scripted group (container) (typed FeaturePython)
  n = 1
  ref = Ba_element
FEATURE [App::DocumentObjectGroupPython] G4_Ba  # scripted group (container) (typed FeaturePython)
  Dunit = g/cm3
  Dvalue = 3.5
  Group = -> [Ba_element003]
  conduct = 2
  density = 1
  expand = 3
  formula = Ba
  name = G4_Ba
  specific = 4
FEATURE [App::DocumentObjectGroupPython] La_element003  label="La_element : 003"  # scripted group (container) (typed FeaturePython)
  n = 1
  ref = La_element
FEATURE [App::DocumentObjectGroupPython] G4_La  # scripted group (container) (typed FeaturePython)
  Dunit = g/cm3
  Dvalue = 6.154
  Group = -> [La_element003]
  conduct = 2
  density = 1
  expand = 3
  formula = La
  name = G4_La
  specific = 4
FEATURE [App::DocumentObjectGroupPython] Ce_element002  label="Ce_element : 1"  # scripted group (container) (typed FeaturePython)
  n = 1
  ref = Ce_element
FEATURE [App::DocumentObjectGroupPython] G4_Ce  # scripted group (container) (typed FeaturePython)
  Dunit = g/cm3
  Dvalue = 6.657
  Group = -> [Ce_element002]
  conduct = 2
  density = 1
  expand = 3
  formula = Ce
  name = G4_Ce
  specific = 4
FEATURE [App::DocumentObjectGroupPython] Pr_element001  label="Pr_element : 1"  # scripted group (container) (typed FeaturePython)
  n = 1
  ref = Pr_element
FEATURE [App::DocumentObjectGroupPython] G4_Pr  # scripted group (container) (typed FeaturePython)
  Dunit = g/cm3
  Dvalue = 6.71
  Group = -> [Pr_element001]
  conduct = 2
  density = 1
  expand = 3
  formula = Pr
  name = G4_Pr
  specific = 4
FEATURE [App::DocumentObjectGroupPython] Nd_element001  label="Nd_element : 1"  # scripted group (container) (typed FeaturePython)
  n = 1
  ref = Nd_element
FEATURE [App::DocumentObjectGroupPython] G4_Nd  # scripted group (container) (typed FeaturePython)
  Dunit = g/cm3
  Dvalue = 6.9
  Group = -> [Nd_element001]
  conduct = 2
  density = 1
  expand = 3
  formula = Nd
  name = G4_Nd
  specific = 4
FEATURE [App::DocumentObjectGroupPython] Pm_element001  label="Pm_element : 1"  # scripted group (container) (typed FeaturePython)
  n = 1
  ref = Pm_element
FEATURE [App::DocumentObjectGroupPython] G4_Pm  # scripted group (container) (typed FeaturePython)
  Dunit = g/cm3
  Dvalue = 7.22
  Group = -> [Pm_element001]
  conduct = 2
  density = 1
  expand = 3
  formula = Pm
  name = G4_Pm
  specific = 4
FEATURE [App::DocumentObjectGroupPython] Sm_element001  label="Sm_element : 1"  # scripted group (container) (typed FeaturePython)
  n = 1
  ref = Sm_element
FEATURE [App::DocumentObjectGroupPython] G4_Sm  # scripted group (container) (typed FeaturePython)
  Dunit = g/cm3
  Dvalue = 7.46
  Group = -> [Sm_element001]
  conduct = 2
  density = 1
  expand = 3
  formula = Sm
  name = G4_Sm
  specific = 4
FEATURE [App::DocumentObjectGroupPython] Eu_element001  label="Eu_element : 1"  # scripted group (container) (typed FeaturePython)
  n = 1
  ref = Eu_element
FEATURE [App::DocumentObjectGroupPython] G4_Eu  # scripted group (container) (typed FeaturePython)
  Dunit = g/cm3
  Dvalue = 5.243
  Group = -> [Eu_element001]
  conduct = 2
  density = 1
  expand = 3
  formula = Eu
  name = G4_Eu
  specific = 4
FEATURE [App::DocumentObjectGroupPython] Gd_element002  label="Gd_element : 1"  # scripted group (container) (typed FeaturePython)
  n = 1
  ref = Gd_element
FEATURE [App::DocumentObjectGroupPython] G4_Gd  # scripted group (container) (typed FeaturePython)
  Dunit = g/cm3
  Dvalue = 7.9004
  Group = -> [Gd_element002]
  conduct = 2
  density = 1
  expand = 3
  formula = Gd
  name = G4_Gd
  specific = 4
FEATURE [App::DocumentObjectGroupPython] Tb_element001  label="Tb_element : 1"  # scripted group (container) (typed FeaturePython)
  n = 1
  ref = Tb_element
FEATURE [App::DocumentObjectGroupPython] G4_Tb  # scripted group (container) (typed FeaturePython)
  Dunit = g/cm3
  Dvalue = 8.229
  Group = -> [Tb_element001]
  conduct = 2
  density = 1
  expand = 3
  formula = Tb
  name = G4_Tb
  specific = 4
FEATURE [App::DocumentObjectGroupPython] Dy_element001  label="Dy_element : 1"  # scripted group (container) (typed FeaturePython)
  n = 1
  ref = Dy_element
FEATURE [App::DocumentObjectGroupPython] G4_Dy  # scripted group (container) (typed FeaturePython)
  Dunit = g/cm3
  Dvalue = 8.55
  Group = -> [Dy_element001]
  conduct = 2
  density = 1
  expand = 3
  formula = Dy
  name = G4_Dy
  specific = 4
FEATURE [App::DocumentObjectGroupPython] Ho_element001  label="Ho_element : 1"  # scripted group (container) (typed FeaturePython)
  n = 1
  ref = Ho_element
FEATURE [App::DocumentObjectGroupPython] G4_Ho  # scripted group (container) (typed FeaturePython)
  Dunit = g/cm3
  Dvalue = 8.795
  Group = -> [Ho_element001]
  conduct = 2
  density = 1
  expand = 3
  formula = Ho
  name = G4_Ho
  specific = 4
FEATURE [App::DocumentObjectGroupPython] Er_element001  label="Er_element : 1"  # scripted group (container) (typed FeaturePython)
  n = 1
  ref = Er_element
FEATURE [App::DocumentObjectGroupPython] G4_Er  # scripted group (container) (typed FeaturePython)
  Dunit = g/cm3
  Dvalue = 9.066
  Group = -> [Er_element001]
  conduct = 2
  density = 1
  expand = 3
  formula = Er
  name = G4_Er
  specific = 4
FEATURE [App::DocumentObjectGroupPython] Tm_element001  label="Tm_element : 1"  # scripted group (container) (typed FeaturePython)
  n = 1
  ref = Tm_element
FEATURE [App::DocumentObjectGroupPython] G4_Tm  # scripted group (container) (typed FeaturePython)
  Dunit = g/cm3
  Dvalue = 9.321
  Group = -> [Tm_element001]
  conduct = 2
  density = 1
  expand = 3
  formula = Tm
  name = G4_Tm
  specific = 4
FEATURE [App::DocumentObjectGroupPython] Yb_element001  label="Yb_element : 1"  # scripted group (container) (typed FeaturePython)
  n = 1
  ref = Yb_element
FEATURE [App::DocumentObjectGroupPython] G4_Yb  # scripted group (container) (typed FeaturePython)
  Dunit = g/cm3
  Dvalue = 6.73
  Group = -> [Yb_element001]
  conduct = 2
  density = 1
  expand = 3
  formula = Yb
  name = G4_Yb
  specific = 4
FEATURE [App::DocumentObjectGroupPython] Lu_element001  label="Lu_element : 1"  # scripted group (container) (typed FeaturePython)
  n = 1
  ref = Lu_element
FEATURE [App::DocumentObjectGroupPython] G4_Lu  # scripted group (container) (typed FeaturePython)
  Dunit = g/cm3
  Dvalue = 9.84
  Group = -> [Lu_element001]
  conduct = 2
  density = 1
  expand = 3
  formula = Lu
  name = G4_Lu
  specific = 4
FEATURE [App::DocumentObjectGroupPython] Hf_element001  label="Hf_element : 1"  # scripted group (container) (typed FeaturePython)
  n = 1
  ref = Hf_element
FEATURE [App::DocumentObjectGroupPython] G4_Hf  # scripted group (container) (typed FeaturePython)
  Dunit = g/cm3
  Dvalue = 13.31
  Group = -> [Hf_element001]
  conduct = 2
  density = 1
  expand = 3
  formula = Hf
  name = G4_Hf
  specific = 4
FEATURE [App::DocumentObjectGroupPython] Ta_element001  label="Ta_element : 1"  # scripted group (container) (typed FeaturePython)
  n = 1
  ref = Ta_element
FEATURE [App::DocumentObjectGroupPython] G4_Ta  # scripted group (container) (typed FeaturePython)
  Dunit = g/cm3
  Dvalue = 16.654
  Group = -> [Ta_element001]
  conduct = 2
  density = 1
  expand = 3
  formula = Ta
  name = G4_Ta
  specific = 4
FEATURE [App::DocumentObjectGroupPython] W_element004  label="W_element : 004"  # scripted group (container) (typed FeaturePython)
  n = 1
  ref = W_element
FEATURE [App::DocumentObjectGroupPython] G4_W  # scripted group (container) (typed FeaturePython)
  Dunit = g/cm3
  Dvalue = 19.3
  Group = -> [W_element004]
  conduct = 2
  density = 1
  expand = 3
  formula = W
  name = G4_W
  specific = 4
FEATURE [App::DocumentObjectGroupPython] Re_element001  label="Re_element : 1"  # scripted group (container) (typed FeaturePython)
  n = 1
  ref = Re_element
FEATURE [App::DocumentObjectGroupPython] G4_Re  # scripted group (container) (typed FeaturePython)
  Dunit = g/cm3
  Dvalue = 21.02
  Group = -> [Re_element001]
  conduct = 2
  density = 1
  expand = 3
  formula = Re
  name = G4_Re
  specific = 4
FEATURE [App::DocumentObjectGroupPython] Os_element001  label="Os_element : 1"  # scripted group (container) (typed FeaturePython)
  n = 1
  ref = Os_element
FEATURE [App::DocumentObjectGroupPython] G4_Os  # scripted group (container) (typed FeaturePython)
  Dunit = g/cm3
  Dvalue = 22.57
  Group = -> [Os_element001]
  conduct = 2
  density = 1
  expand = 3
  formula = Os
  name = G4_Os
  specific = 4
FEATURE [App::DocumentObjectGroupPython] Ir_element001  label="Ir_element : 1"  # scripted group (container) (typed FeaturePython)
  n = 1
  ref = Ir_element
FEATURE [App::DocumentObjectGroupPython] G4_Ir  # scripted group (container) (typed FeaturePython)
  Dunit = g/cm3
  Dvalue = 22.42
  Group = -> [Ir_element001]
  conduct = 2
  density = 1
  expand = 3
  formula = Ir
  name = G4_Ir
  specific = 4
FEATURE [App::DocumentObjectGroupPython] Pt_element001  label="Pt_element : 1"  # scripted group (container) (typed FeaturePython)
  n = 1
  ref = Pt_element
FEATURE [App::DocumentObjectGroupPython] G4_Pt  # scripted group (container) (typed FeaturePython)
  Dunit = g/cm3
  Dvalue = 21.45
  Group = -> [Pt_element001]
  conduct = 2
  density = 1
  expand = 3
  formula = Pt
  name = G4_Pt
  specific = 4
FEATURE [App::DocumentObjectGroupPython] Au_element001  label="Au_element : 1"  # scripted group (container) (typed FeaturePython)
  n = 1
  ref = Au_element
FEATURE [App::DocumentObjectGroupPython] G4_Au  # scripted group (container) (typed FeaturePython)
  Dunit = g/cm3
  Dvalue = 19.32
  Group = -> [Au_element001]
  conduct = 2
  density = 1
  expand = 3
  formula = Au
  name = G4_Au
  specific = 4
FEATURE [App::DocumentObjectGroupPython] Hg_element002  label="Hg_element : 002"  # scripted group (container) (typed FeaturePython)
  n = 1
  ref = Hg_element
FEATURE [App::DocumentObjectGroupPython] G4_Hg  # scripted group (container) (typed FeaturePython)
  Dunit = g/cm3
  Dvalue = 13.546
  Group = -> [Hg_element002]
  conduct = 2
  density = 1
  expand = 3
  formula = Hg
  name = G4_Hg
  specific = 4
FEATURE [App::DocumentObjectGroupPython] Tl_element002  label="Tl_element : 002"  # scripted group (container) (typed FeaturePython)
  n = 1
  ref = Tl_element
FEATURE [App::DocumentObjectGroupPython] G4_Tl  # scripted group (container) (typed FeaturePython)
  Dunit = g/cm3
  Dvalue = 11.72
  Group = -> [Tl_element002]
  conduct = 2
  density = 1
  expand = 3
  formula = Tl
  name = G4_Tl
  specific = 4
FEATURE [App::DocumentObjectGroupPython] Pb_element003  label="Pb_element : 1"  # scripted group (container) (typed FeaturePython)
  n = 1
  ref = Pb_element
FEATURE [App::DocumentObjectGroupPython] G4_Pb  # scripted group (container) (typed FeaturePython)
  Dunit = g/cm3
  Dvalue = 11.35
  Group = -> [Pb_element003]
  conduct = 2
  density = 1
  expand = 3
  formula = Pb
  name = G4_Pb
  specific = 4
FEATURE [App::DocumentObjectGroupPython] Bi_element002  label="Bi_element : 1"  # scripted group (container) (typed FeaturePython)
  n = 1
  ref = Bi_element
FEATURE [App::DocumentObjectGroupPython] G4_Bi  # scripted group (container) (typed FeaturePython)
  Dunit = g/cm3
  Dvalue = 9.747
  Group = -> [Bi_element002]
  conduct = 2
  density = 1
  expand = 3
  formula = Bi
  name = G4_Bi
  specific = 4
FEATURE [App::DocumentObjectGroupPython] Po_element001  label="Po_element : 1"  # scripted group (container) (typed FeaturePython)
  n = 1
  ref = Po_element
FEATURE [App::DocumentObjectGroupPython] G4_Po  # scripted group (container) (typed FeaturePython)
  Dunit = g/cm3
  Dvalue = 9.32
  Group = -> [Po_element001]
  conduct = 2
  density = 1
  expand = 3
  formula = Po
  name = G4_Po
  specific = 4
FEATURE [App::DocumentObjectGroupPython] At_element001  label="At_element : 1"  # scripted group (container) (typed FeaturePython)
  n = 1
  ref = At_element
FEATURE [App::DocumentObjectGroupPython] G4_At  # scripted group (container) (typed FeaturePython)
  Dunit = g/cm3
  Dvalue = 9.32
  Group = -> [At_element001]
  conduct = 2
  density = 1
  expand = 3
  formula = At
  name = G4_At
  specific = 4
FEATURE [App::DocumentObjectGroupPython] Rn_element001  label="Rn_element : 1"  # scripted group (container) (typed FeaturePython)
  n = 1
  ref = Rn_element
FEATURE [App::DocumentObjectGroupPython] G4_Rn  # scripted group (container) (typed FeaturePython)
  Dunit = g/cm3
  Dvalue = 0.00900662
  Group = -> [Rn_element001]
  conduct = 2
  density = 1
  expand = 3
  formula = Rn
  name = G4_Rn
  specific = 4
FEATURE [App::DocumentObjectGroupPython] Fr_element001  label="Fr_element : 1"  # scripted group (container) (typed FeaturePython)
  n = 1
  ref = Fr_element
FEATURE [App::DocumentObjectGroupPython] G4_Fr  # scripted group (container) (typed FeaturePython)
  Dunit = g/cm3
  Dvalue = 1
  Group = -> [Fr_element001]
  conduct = 2
  density = 1
  expand = 3
  formula = Fr
  name = G4_Fr
  specific = 4
FEATURE [App::DocumentObjectGroupPython] Ra_element001  label="Ra_element : 1"  # scripted group (container) (typed FeaturePython)
  n = 1
  ref = Ra_element
FEATURE [App::DocumentObjectGroupPython] G4_Ra  # scripted group (container) (typed FeaturePython)
  Dunit = g/cm3
  Dvalue = 5
  Group = -> [Ra_element001]
  conduct = 2
  density = 1
  expand = 3
  formula = Ra
  name = G4_Ra
  specific = 4
FEATURE [App::DocumentObjectGroupPython] Ac_element001  label="Ac_element : 1"  # scripted group (container) (typed FeaturePython)
  n = 1
  ref = Ac_element
FEATURE [App::DocumentObjectGroupPython] G4_Ac  # scripted group (container) (typed FeaturePython)
  Dunit = g/cm3
  Dvalue = 10.07
  Group = -> [Ac_element001]
  conduct = 2
  density = 1
  expand = 3
  formula = Ac
  name = G4_Ac
  specific = 4
FEATURE [App::DocumentObjectGroupPython] Th_element001  label="Th_element : 1"  # scripted group (container) (typed FeaturePython)
  n = 1
  ref = Th_element
FEATURE [App::DocumentObjectGroupPython] G4_Th  # scripted group (container) (typed FeaturePython)
  Dunit = g/cm3
  Dvalue = 11.72
  Group = -> [Th_element001]
  conduct = 2
  density = 1
  expand = 3
  formula = Th
  name = G4_Th
  specific = 4
FEATURE [App::DocumentObjectGroupPython] Pa_element001  label="Pa_element : 1"  # scripted group (container) (typed FeaturePython)
  n = 1
  ref = Pa_element
FEATURE [App::DocumentObjectGroupPython] G4_Pa  # scripted group (container) (typed FeaturePython)
  Dunit = g/cm3
  Dvalue = 15.37
  Group = -> [Pa_element001]
  conduct = 2
  density = 1
  expand = 3
  formula = Pa
  name = G4_Pa
  specific = 4
FEATURE [App::DocumentObjectGroupPython] U_element004  label="U_element : 004"  # scripted group (container) (typed FeaturePython)
  n = 1
  ref = U_element
FEATURE [App::DocumentObjectGroupPython] G4_U  # scripted group (container) (typed FeaturePython)
  Dunit = g/cm3
  Dvalue = 18.95
  Group = -> [U_element004]
  conduct = 2
  density = 1
  expand = 3
  formula = U
  name = G4_U
  specific = 4
FEATURE [App::DocumentObjectGroupPython] Np_element001  label="Np_element : 1"  # scripted group (container) (typed FeaturePython)
  n = 1
  ref = Np_element
FEATURE [App::DocumentObjectGroupPython] G4_Np  # scripted group (container) (typed FeaturePython)
  Dunit = g/cm3
  Dvalue = 20.25
  Group = -> [Np_element001]
  conduct = 2
  density = 1
  expand = 3
  formula = Np
  name = G4_Np
  specific = 4
FEATURE [App::DocumentObjectGroupPython] Pu_element002  label="Pu_element : 002"  # scripted group (container) (typed FeaturePython)
  n = 1
  ref = Pu_element
FEATURE [App::DocumentObjectGroupPython] G4_Pu  # scripted group (container) (typed FeaturePython)
  Dunit = g/cm3
  Dvalue = 19.84
  Group = -> [Pu_element002]
  conduct = 2
  density = 1
  expand = 3
  formula = Pu
  name = G4_Pu
  specific = 4
FEATURE [App::DocumentObjectGroupPython] Am_element001  label="Am_element : 1"  # scripted group (container) (typed FeaturePython)
  n = 1
  ref = Am_element
FEATURE [App::DocumentObjectGroupPython] G4_Am  # scripted group (container) (typed FeaturePython)
  Dunit = g/cm3
  Dvalue = 13.67
  Group = -> [Am_element001]
  conduct = 2
  density = 1
  expand = 3
  formula = Am
  name = G4_Am
  specific = 4
FEATURE [App::DocumentObjectGroupPython] Cm_element001  label="Cm_element : 1"  # scripted group (container) (typed FeaturePython)
  n = 1
  ref = Cm_element
FEATURE [App::DocumentObjectGroupPython] G4_Cm  # scripted group (container) (typed FeaturePython)
  Dunit = g/cm3
  Dvalue = 13.51
  Group = -> [Cm_element001]
  conduct = 2
  density = 1
  expand = 3
  formula = Cm
  name = G4_Cm
  specific = 4
FEATURE [App::DocumentObjectGroupPython] Bk_element001  label="Bk_element : 1"  # scripted group (container) (typed FeaturePython)
  n = 1
  ref = Bk_element
FEATURE [App::DocumentObjectGroupPython] G4_Bk  # scripted group (container) (typed FeaturePython)
  Dunit = g/cm3
  Dvalue = 14
  Group = -> [Bk_element001]
  conduct = 2
  density = 1
  expand = 3
  formula = Bk
  name = G4_Bk
  specific = 4
FEATURE [App::DocumentObjectGroupPython] Cf_element001  label="Cf_element : 1"  # scripted group (container) (typed FeaturePython)
  n = 1
  ref = Cf_element
FEATURE [App::DocumentObjectGroupPython] G4_Cf  # scripted group (container) (typed FeaturePython)
  Dunit = g/cm3
  Dvalue = 10
  Group = -> [Cf_element001]
  conduct = 2
  density = 1
  expand = 3
  formula = Cf
  name = G4_Cf
  specific = 4
FEATURE [App::DocumentObjectGroupPython] Element  # scripted group (container) (typed FeaturePython)
  Group = -> [G4_H,G4_He,G4_Li,G4_Be,G4_B,G4_C,G4_N,G4_O,G4_F,G4_Ne,G4_Na,G4_Mg,G4_Al,G4_Si,G4_P,G4_S,G4_Cl,G4_Ar,G4_K,G4_Ca,G4_Sc,G4_Ti,G4_V,G4_Cr,G4_Mn,G4_Fe,G4_Co,G4_Ni,G4_Cu,G4_Zn,G4_Ga,G4_Ge,G4_As,G4_Se,G4_Br,G4_Kr,G4_Rb,G4_Sr,G4_Y,G4_Zr,G4_Nb,G4_Mo,G4_Tc,G4_Ru,G4_Rh,G4_Pd,G4_Ag,G4_Cd,G4_In,G4_Sn,G4_Sb,G4_Te,G4_I,G4_Xe,G4_Cs,G4_Ba,G4_La,G4_Ce,G4_Pr,G4_Nd,G4_Pm,G4_Sm,G4_Eu,G4_Gd,G4_Tb,G4_Dy,G4_Ho,G4_Er,+30 more]
FEATURE [App::DocumentObjectGroupPython] H_element114  label="H_element : 063"  # scripted group (container) (typed FeaturePython)
  n = 2
  ref = H_element
FEATURE [App::DocumentObjectGroupPython] G4_lH2  # scripted group (container) (typed FeaturePython)
  Dunit = g/cm3
  Dvalue = 0.0708
  Group = -> [H_element114]
  conduct = 2
  density = 1
  expand = 3
  formula = G4_lH2
  name = G4_lH2
  specific = 4
FEATURE [App::DocumentObjectGroupPython] N_element049  label="N_element : 022"  # scripted group (container) (typed FeaturePython)
  n = 2
  ref = N_element
FEATURE [App::DocumentObjectGroupPython] G4_lN2  # scripted group (container) (typed FeaturePython)
  Dunit = g/cm3
  Dvalue = 0.807
  Group = -> [N_element049]
  conduct = 2
  density = 1
  expand = 3
  formula = G4_lN2
  name = G4_lN2
  specific = 4
FEATURE [App::DocumentObjectGroupPython] O_element106  label="O_element : 060"  # scripted group (container) (typed FeaturePython)
  n = 2
  ref = O_element
FEATURE [App::DocumentObjectGroupPython] G4_lO2  # scripted group (container) (typed FeaturePython)
  Dunit = g/cm3
  Dvalue = 1.141
  Group = -> [O_element106]
  conduct = 2
  density = 1
  expand = 3
  formula = G4_lO2
  name = G4_lO2
  specific = 4
FEATURE [App::DocumentObjectGroupPython] Ar  label="Ar : 1"  # scripted group (container) (typed FeaturePython)
  n = 1
  ref = Ar
FEATURE [App::DocumentObjectGroupPython] G4_lAr  # scripted group (container) (typed FeaturePython)
  Dunit = g/cm3
  Dvalue = 1.396
  Group = -> [Ar]
  conduct = 2
  density = 1
  expand = 3
  formula = G4_lAr
  name = G4_lAr
  specific = 4
FEATURE [App::DocumentObjectGroupPython] Br  label="Br : 1"  # scripted group (container) (typed FeaturePython)
  n = 1
  ref = Br
FEATURE [App::DocumentObjectGroupPython] G4_lBr  # scripted group (container) (typed FeaturePython)
  Dunit = g/cm3
  Dvalue = 3.1028
  Group = -> [Br]
  conduct = 2
  density = 1
  expand = 3
  formula = G4_lBr
  name = G4_lBr
  specific = 4
FEATURE [App::DocumentObjectGroupPython] Kr  label="Kr : 1"  # scripted group (container) (typed FeaturePython)
  n = 1
  ref = Kr
FEATURE [App::DocumentObjectGroupPython] G4_lKr  # scripted group (container) (typed FeaturePython)
  Dunit = g/cm3
  Dvalue = 2.418
  Group = -> [Kr]
  conduct = 2
  density = 1
  expand = 3
  formula = G4_lKr
  name = G4_lKr
  specific = 4
FEATURE [App::DocumentObjectGroupPython] Xe  label="Xe : 1"  # scripted group (container) (typed FeaturePython)
  n = 1
  ref = Xe
FEATURE [App::DocumentObjectGroupPython] G4_lXe  # scripted group (container) (typed FeaturePython)
  Dunit = g/cm3
  Dvalue = 2.953
  Group = -> [Xe]
  conduct = 2
  density = 1
  expand = 3
  formula = G4_lXe
  name = G4_lXe
  specific = 4
FEATURE [App::DocumentObjectGroupPython] O_element107  label="O_element : 061"  # scripted group (container) (typed FeaturePython)
  n = 4
  ref = O_element
FEATURE [App::DocumentObjectGroupPython] Pb_element004  label="Pb_element : 002"  # scripted group (container) (typed FeaturePython)
  n = 1
  ref = Pb_element
FEATURE [App::DocumentObjectGroupPython] W_element005  label="W_element : 005"  # scripted group (container) (typed FeaturePython)
  n = 1
  ref = W_element
FEATURE [App::DocumentObjectGroupPython] G4_PbWO4  # scripted group (container) (typed FeaturePython)
  Dunit = g/cm3
  Dvalue = 8.28
  Group = -> [O_element107,Pb_element004,W_element005]
  conduct = 2
  density = 1
  expand = 3
  formula = G4_PbWO4
  name = G4_PbWO4
  specific = 4
FEATURE [App::DocumentObjectGroupPython] alactic  label="alactic : 1"  # scripted group (container) (typed FeaturePython)
  n = 1
  ref = alactic
FEATURE [App::DocumentObjectGroupPython] G4_Galactic  # scripted group (container) (typed FeaturePython)
  Dunit = g/cm3
  Dvalue = 0
  Group = -> [alactic]
  conduct = 2
  density = 1
  expand = 3
  formula = G4_Galactic
  name = G4_Galactic
  specific = 4
FEATURE [App::DocumentObjectGroupPython] RAPHITE_POROUS  label="RAPHITE_POROUS : 1"  # scripted group (container) (typed FeaturePython)
  n = 1
  ref = RAPHITE_POROUS
FEATURE [App::DocumentObjectGroupPython] G4_GRAPHITE_POROUS  # scripted group (container) (typed FeaturePython)
  Dunit = g/cm3
  Dvalue = 1.7
  Group = -> [RAPHITE_POROUS]
  conduct = 2
  density = 1
  expand = 3
  formula = G4_GRAPHITE_POROUS
  name = G4_GRAPHITE_POROUS
  specific = 4
FEATURE [App::DocumentObjectGroupPython] H_element115  label="H_element : 0.150"  # scripted group (container) (typed FeaturePython)
  n = 0.080538
FEATURE [App::DocumentObjectGroupPython] C_element125  label="C_element : 0.600"  # scripted group (container) (typed FeaturePython)
  n = 0.599848
FEATURE [App::DocumentObjectGroupPython] O_element108  label="O_element : 0.320"  # scripted group (container) (typed FeaturePython)
  n = 0.319614
FEATURE [App::DocumentObjectGroupPython] G4_LUCITE  # scripted group (container) (typed FeaturePython)
  Dunit = g/cm3
  Dvalue = 1.19
  Group = -> [H_element115,C_element125,O_element108]
  conduct = 2
  density = 1
  expand = 3
  formula = G4_LUCITE
  name = G4_LUCITE
  specific = 4
FEATURE [App::DocumentObjectGroupPython] Cu_element002  label="Cu_element : 62"  # scripted group (container) (typed FeaturePython)
  n = 62
  ref = Cu_element
FEATURE [App::DocumentObjectGroupPython] Zn_element002  label="Zn_element : 35"  # scripted group (container) (typed FeaturePython)
  n = 35
  ref = Zn_element
FEATURE [App::DocumentObjectGroupPython] Pb_element005  label="Pb_element : 3"  # scripted group (container) (typed FeaturePython)
  n = 3
  ref = Pb_element
FEATURE [App::DocumentObjectGroupPython] G4_BRASS  # scripted group (container) (typed FeaturePython)
  Dunit = g/cm3
  Dvalue = 8.52
  Group = -> [Cu_element002,Zn_element002,Pb_element005]
  conduct = 2
  density = 1
  expand = 3
  formula = G4_BRASS
  name = G4_BRASS
  specific = 4
FEATURE [App::DocumentObjectGroupPython] Cu_element003  label="Cu_element : 89"  # scripted group (container) (typed FeaturePython)
  n = 89
  ref = Cu_element
FEATURE [App::DocumentObjectGroupPython] Zn_element003  label="Zn_element : 9"  # scripted group (container) (typed FeaturePython)
  n = 9
  ref = Zn_element
FEATURE [App::DocumentObjectGroupPython] Pb_element006  label="Pb_element : 2"  # scripted group (container) (typed FeaturePython)
  n = 2
  ref = Pb_element
FEATURE [App::DocumentObjectGroupPython] G4_BRONZE  # scripted group (container) (typed FeaturePython)
  Dunit = g/cm3
  Dvalue = 8.82
  Group = -> [Cu_element003,Zn_element003,Pb_element006]
  conduct = 2
  density = 1
  expand = 3
  formula = G4_BRONZE
  name = G4_BRONZE
  specific = 4
FEATURE [App::DocumentObjectGroupPython] Fe_element008  label="Fe_element : 74"  # scripted group (container) (typed FeaturePython)
  n = 74
  ref = Fe_element
FEATURE [App::DocumentObjectGroupPython] Cr_element002  label="Cr_element : 18"  # scripted group (container) (typed FeaturePython)
  n = 18
  ref = Cr_element
FEATURE [App::DocumentObjectGroupPython] Ni_element002  label="Ni_element : 8"  # scripted group (container) (typed FeaturePython)
  n = 8
  ref = Ni_element
FEATURE [App::DocumentObjectGroupPython] G4_STAINLESS_STEEL  label="G4_STAINLESS-STEEL"  # scripted group (container) (typed FeaturePython)
  Dunit = g/cm3
  Dvalue = 8
  Group = -> [Fe_element008,Cr_element002,Ni_element002]
  conduct = 2
  density = 1
  expand = 3
  formula = G4_STAINLESS-STEEL
  name = G4_STAINLESS-STEEL
  specific = 4
FEATURE [App::DocumentObjectGroupPython] H_element116  label="H_element : 064"  # scripted group (container) (typed FeaturePython)
  n = 18
  ref = H_element
FEATURE [App::DocumentObjectGroupPython] C_element126  label="C_element : 071"  # scripted group (container) (typed FeaturePython)
  n = 12
  ref = C_element
FEATURE [App::DocumentObjectGroupPython] O_element109  label="O_element : 062"  # scripted group (container) (typed FeaturePython)
  n = 7
  ref = O_element
FEATURE [App::DocumentObjectGroupPython] G4_CR39  # scripted group (container) (typed FeaturePython)
  Dunit = g/cm3
  Dvalue = 1.32
  Group = -> [H_element116,C_element126,O_element109]
  conduct = 2
  density = 1
  expand = 3
  formula = G4_CR39
  name = G4_CR39
  specific = 4
FEATURE [App::DocumentObjectGroupPython] H_element117  label="H_element : 38"  # scripted group (container) (typed FeaturePython)
  n = 38
  ref = H_element
FEATURE [App::DocumentObjectGroupPython] C_element127  label="C_element : 072"  # scripted group (container) (typed FeaturePython)
  n = 18
  ref = C_element
FEATURE [App::DocumentObjectGroupPython] O_element110  label="O_element : 063"  # scripted group (container) (typed FeaturePython)
  n = 1
  ref = O_element
FEATURE [App::DocumentObjectGroupPython] G4_OCTADECANOL  # scripted group (container) (typed FeaturePython)
  Dunit = g/cm3
  Dvalue = 0.812
  Group = -> [H_element117,C_element127,O_element110]
  conduct = 2
  density = 1
  expand = 3
  formula = G4_OCTADECANOL
  name = G4_OCTADECANOL
  specific = 4
FEATURE [App::DocumentObjectGroupPython] HEP  # scripted group (container) (typed FeaturePython)
  Group = -> [G4_lH2,G4_lN2,G4_lO2,G4_lAr,G4_lBr,G4_lKr,G4_lXe,G4_PbWO4,G4_Galactic,G4_GRAPHITE_POROUS,G4_LUCITE,G4_BRASS,G4_BRONZE,G4_STAINLESS_STEEL,G4_CR39,G4_OCTADECANOL]
FEATURE [App::DocumentObjectGroupPython] C_element128  label="C_element : 073"  # scripted group (container) (typed FeaturePython)
  n = 14
  ref = C_element
FEATURE [App::DocumentObjectGroupPython] H_element118  label="H_element : 065"  # scripted group (container) (typed FeaturePython)
  n = 10
  ref = H_element
FEATURE [App::DocumentObjectGroupPython] O_element111  label="O_element : 064"  # scripted group (container) (typed FeaturePython)
  n = 2
  ref = O_element
FEATURE [App::DocumentObjectGroupPython] N_element050  label="N_element : 023"  # scripted group (container) (typed FeaturePython)
  n = 2
  ref = N_element
FEATURE [App::DocumentObjectGroupPython] G4_KEVLAR  # scripted group (container) (typed FeaturePython)
  Dunit = g/cm3
  Dvalue = 1.44
  Group = -> [C_element128,H_element118,O_element111,N_element050]
  conduct = 2
  density = 1
  expand = 3
  formula = G4_KEVLAR
  name = G4_KEVLAR
  specific = 4
FEATURE [App::DocumentObjectGroupPython] C_element129  label="C_element : 074"  # scripted group (container) (typed FeaturePython)
  n = 10
  ref = C_element
FEATURE [App::DocumentObjectGroupPython] H_element119  label="H_element : 066"  # scripted group (container) (typed FeaturePython)
  n = 8
  ref = H_element
FEATURE [App::DocumentObjectGroupPython] O_element112  label="O_element : 065"  # scripted group (container) (typed FeaturePython)
  n = 4
  ref = O_element
FEATURE [App::DocumentObjectGroupPython] G4_DACRON  # scripted group (container) (typed FeaturePython)
  Dunit = g/cm3
  Dvalue = 1.4
  Group = -> [C_element129,H_element119,O_element112]
  conduct = 2
  density = 1
  expand = 3
  formula = G4_DACRON
  name = G4_DACRON
  specific = 4
FEATURE [App::DocumentObjectGroupPython] C_element130  label="C_element : 075"  # scripted group (container) (typed FeaturePython)
  n = 4
  ref = C_element
FEATURE [App::DocumentObjectGroupPython] H_element120  label="H_element : 067"  # scripted group (container) (typed FeaturePython)
  n = 5
  ref = H_element
FEATURE [App::DocumentObjectGroupPython] Cl_element030  label="Cl_element : 016"  # scripted group (container) (typed FeaturePython)
  n = 1
  ref = Cl_element
FEATURE [App::DocumentObjectGroupPython] G4_NEOPRENE  # scripted group (container) (typed FeaturePython)
  Dunit = g/cm3
  Dvalue = 1.23
  Group = -> [C_element130,H_element120,Cl_element030]
  conduct = 2
  density = 1
  expand = 3
  formula = G4_NEOPRENE
  name = G4_NEOPRENE
  specific = 4
FEATURE [App::DocumentObjectGroupPython] Space  # scripted group (container) (typed FeaturePython)
  Group = -> [G4_KEVLAR,G4_DACRON,G4_NEOPRENE]
FEATURE [App::DocumentObjectGroupPython] H_element121  label="H_element : 068"  # scripted group (container) (typed FeaturePython)
  n = 5
  ref = H_element
FEATURE [App::DocumentObjectGroupPython] C_element131  label="C_element : 076"  # scripted group (container) (typed FeaturePython)
  n = 4
  ref = C_element
FEATURE [App::DocumentObjectGroupPython] N_element051  label="N_element : 3"  # scripted group (container) (typed FeaturePython)
  n = 3
  ref = N_element
FEATURE [App::DocumentObjectGroupPython] O_element113  label="O_element : 066"  # scripted group (container) (typed FeaturePython)
  n = 1
  ref = O_element
FEATURE [App::DocumentObjectGroupPython] G4_CYTOSINE  # scripted group (container) (typed FeaturePython)
  Dunit = g/cm3
  Dvalue = 1.55
  Group = -> [H_element121,C_element131,N_element051,O_element113]
  conduct = 2
  density = 1
  expand = 3
  formula = G4_CYTOSINE
  name = G4_CYTOSINE
  specific = 4
FEATURE [App::DocumentObjectGroupPython] H_element122  label="H_element : 069"  # scripted group (container) (typed FeaturePython)
  n = 6
  ref = H_element
FEATURE [App::DocumentObjectGroupPython] C_element132  label="C_element : 077"  # scripted group (container) (typed FeaturePython)
  n = 5
  ref = C_element
FEATURE [App::DocumentObjectGroupPython] N_element052  label="N_element : 024"  # scripted group (container) (typed FeaturePython)
  n = 2
  ref = N_element
FEATURE [App::DocumentObjectGroupPython] O_element114  label="O_element : 067"  # scripted group (container) (typed FeaturePython)
  n = 2
  ref = O_element
FEATURE [App::DocumentObjectGroupPython] G4_THYMINE  # scripted group (container) (typed FeaturePython)
  Dunit = g/cm3
  Dvalue = 1.23
  Group = -> [H_element122,C_element132,N_element052,O_element114]
  conduct = 2
  density = 1
  expand = 3
  formula = G4_THYMINE
  name = G4_THYMINE
  specific = 4
FEATURE [App::DocumentObjectGroupPython] H_element123  label="H_element : 070"  # scripted group (container) (typed FeaturePython)
  n = 4
  ref = H_element
FEATURE [App::DocumentObjectGroupPython] C_element133  label="C_element : 078"  # scripted group (container) (typed FeaturePython)
  n = 4
  ref = C_element
FEATURE [App::DocumentObjectGroupPython] N_element053  label="N_element : 025"  # scripted group (container) (typed FeaturePython)
  n = 2
  ref = N_element
FEATURE [App::DocumentObjectGroupPython] O_element115  label="O_element : 068"  # scripted group (container) (typed FeaturePython)
  n = 2
  ref = O_element
FEATURE [App::DocumentObjectGroupPython] G4_URACIL  # scripted group (container) (typed FeaturePython)
  Dunit = g/cm3
  Dvalue = 1.32
  Group = -> [H_element123,C_element133,N_element053,O_element115]
  conduct = 2
  density = 1
  expand = 3
  formula = G4_URACIL
  name = G4_URACIL
  specific = 4
FEATURE [App::DocumentObjectGroupPython] H_element124  label="H_element : 071"  # scripted group (container) (typed FeaturePython)
  n = 4
  ref = H_element
FEATURE [App::DocumentObjectGroupPython] C_element134  label="C_element : 079"  # scripted group (container) (typed FeaturePython)
  n = 5
  ref = C_element
FEATURE [App::DocumentObjectGroupPython] N_element054  label="N_element : 026"  # scripted group (container) (typed FeaturePython)
  n = 5
  ref = N_element
FEATURE [App::DocumentObjectGroupPython] G4_DNA_ADENINE  # scripted group (container) (typed FeaturePython)
  Dunit = g/cm3
  Dvalue = 1
  Group = -> [H_element124,C_element134,N_element054]
  conduct = 2
  density = 1
  expand = 3
  formula = G4_DNA_ADENINE
  name = G4_DNA_ADENINE
  specific = 4
FEATURE [App::DocumentObjectGroupPython] H_element125  label="H_element : 072"  # scripted group (container) (typed FeaturePython)
  n = 4
  ref = H_element
FEATURE [App::DocumentObjectGroupPython] C_element135  label="C_element : 080"  # scripted group (container) (typed FeaturePython)
  n = 5
  ref = C_element
FEATURE [App::DocumentObjectGroupPython] N_element055  label="N_element : 027"  # scripted group (container) (typed FeaturePython)
  n = 5
  ref = N_element
FEATURE [App::DocumentObjectGroupPython] O_element116  label="O_element : 069"  # scripted group (container) (typed FeaturePython)
  n = 1
  ref = O_element
FEATURE [App::DocumentObjectGroupPython] G4_DNA_GUANINE  # scripted group (container) (typed FeaturePython)
  Dunit = g/cm3
  Dvalue = 1
  Group = -> [H_element125,C_element135,N_element055,O_element116]
  conduct = 2
  density = 1
  expand = 3
  formula = G4_DNA_GUANINE
  name = G4_DNA_GUANINE
  specific = 4
FEATURE [App::DocumentObjectGroupPython] H_element126  label="H_element : 073"  # scripted group (container) (typed FeaturePython)
  n = 4
  ref = H_element
FEATURE [App::DocumentObjectGroupPython] C_element136  label="C_element : 081"  # scripted group (container) (typed FeaturePython)
  n = 4
  ref = C_element
FEATURE [App::DocumentObjectGroupPython] N_element056  label="N_element : 028"  # scripted group (container) (typed FeaturePython)
  n = 3
  ref = N_element
FEATURE [App::DocumentObjectGroupPython] O_element117  label="O_element : 070"  # scripted group (container) (typed FeaturePython)
  n = 1
  ref = O_element
FEATURE [App::DocumentObjectGroupPython] G4_DNA_CYTOSINE  # scripted group (container) (typed FeaturePython)
  Dunit = g/cm3
  Dvalue = 1
  Group = -> [H_element126,C_element136,N_element056,O_element117]
  conduct = 2
  density = 1
  expand = 3
  formula = G4_DNA_CYTOSINE
  name = G4_DNA_CYTOSINE
  specific = 4
FEATURE [App::DocumentObjectGroupPython] H_element127  label="H_element : 074"  # scripted group (container) (typed FeaturePython)
  n = 5
  ref = H_element
FEATURE [App::DocumentObjectGroupPython] C_element137  label="C_element : 082"  # scripted group (container) (typed FeaturePython)
  n = 5
  ref = C_element
FEATURE [App::DocumentObjectGroupPython] N_element057  label="N_element : 029"  # scripted group (container) (typed FeaturePython)
  n = 2
  ref = N_element
FEATURE [App::DocumentObjectGroupPython] O_element118  label="O_element : 071"  # scripted group (container) (typed FeaturePython)
  n = 2
  ref = O_element
FEATURE [App::DocumentObjectGroupPython] G4_DNA_THYMINE  # scripted group (container) (typed FeaturePython)
  Dunit = g/cm3
  Dvalue = 1
  Group = -> [H_element127,C_element137,N_element057,O_element118]
  conduct = 2
  density = 1
  expand = 3
  formula = G4_DNA_THYMINE
  name = G4_DNA_THYMINE
  specific = 4
FEATURE [App::DocumentObjectGroupPython] H_element128  label="H_element : 075"  # scripted group (container) (typed FeaturePython)
  n = 3
  ref = H_element
FEATURE [App::DocumentObjectGroupPython] C_element138  label="C_element : 083"  # scripted group (container) (typed FeaturePython)
  n = 4
  ref = C_element
FEATURE [App::DocumentObjectGroupPython] N_element058  label="N_element : 030"  # scripted group (container) (typed FeaturePython)
  n = 2
  ref = N_element
FEATURE [App::DocumentObjectGroupPython] O_element119  label="O_element : 072"  # scripted group (container) (typed FeaturePython)
  n = 2
  ref = O_element
FEATURE [App::DocumentObjectGroupPython] G4_DNA_URACIL  # scripted group (container) (typed FeaturePython)
  Dunit = g/cm3
  Dvalue = 1
  Group = -> [H_element128,C_element138,N_element058,O_element119]
  conduct = 2
  density = 1
  expand = 3
  formula = G4_DNA_URACIL
  name = G4_DNA_URACIL
  specific = 4
FEATURE [App::DocumentObjectGroupPython] H_element129  label="H_element : 076"  # scripted group (container) (typed FeaturePython)
  n = 10
  ref = H_element
FEATURE [App::DocumentObjectGroupPython] C_element139  label="C_element : 084"  # scripted group (container) (typed FeaturePython)
  n = 10
  ref = C_element
FEATURE [App::DocumentObjectGroupPython] N_element059  label="N_element : 031"  # scripted group (container) (typed FeaturePython)
  n = 5
  ref = N_element
FEATURE [App::DocumentObjectGroupPython] O_element120  label="O_element : 073"  # scripted group (container) (typed FeaturePython)
  n = 4
  ref = O_element
FEATURE [App::DocumentObjectGroupPython] G4_DNA_ADENOSINE  # scripted group (container) (typed FeaturePython)
  Dunit = g/cm3
  Dvalue = 1
  Group = -> [H_element129,C_element139,N_element059,O_element120]
  conduct = 2
  density = 1
  expand = 3
  formula = G4_DNA_ADENOSINE
  name = G4_DNA_ADENOSINE
  specific = 4
FEATURE [App::DocumentObjectGroupPython] H_element130  label="H_element : 077"  # scripted group (container) (typed FeaturePython)
  n = 10
  ref = H_element
FEATURE [App::DocumentObjectGroupPython] C_element140  label="C_element : 085"  # scripted group (container) (typed FeaturePython)
  n = 10
  ref = C_element
FEATURE [App::DocumentObjectGroupPython] N_element060  label="N_element : 032"  # scripted group (container) (typed FeaturePython)
  n = 5
  ref = N_element
FEATURE [App::DocumentObjectGroupPython] O_element121  label="O_element : 074"  # scripted group (container) (typed FeaturePython)
  n = 5
  ref = O_element
FEATURE [App::DocumentObjectGroupPython] G4_DNA_GUANOSINE  # scripted group (container) (typed FeaturePython)
  Dunit = g/cm3
  Dvalue = 1
  Group = -> [H_element130,C_element140,N_element060,O_element121]
  conduct = 2
  density = 1
  expand = 3
  formula = G4_DNA_GUANOSINE
  name = G4_DNA_GUANOSINE
  specific = 4
FEATURE [App::DocumentObjectGroupPython] H_element131  label="H_element : 078"  # scripted group (container) (typed FeaturePython)
  n = 10
  ref = H_element
FEATURE [App::DocumentObjectGroupPython] C_element141  label="C_element : 086"  # scripted group (container) (typed FeaturePython)
  n = 9
  ref = C_element
FEATURE [App::DocumentObjectGroupPython] N_element061  label="N_element : 033"  # scripted group (container) (typed FeaturePython)
  n = 3
  ref = N_element
FEATURE [App::DocumentObjectGroupPython] O_element122  label="O_element : 075"  # scripted group (container) (typed FeaturePython)
  n = 5
  ref = O_element
FEATURE [App::DocumentObjectGroupPython] G4_DNA_CYTIDINE  # scripted group (container) (typed FeaturePython)
  Dunit = g/cm3
  Dvalue = 1
  Group = -> [H_element131,C_element141,N_element061,O_element122]
  conduct = 2
  density = 1
  expand = 3
  formula = G4_DNA_CYTIDINE
  name = G4_DNA_CYTIDINE
  specific = 4
FEATURE [App::DocumentObjectGroupPython] H_element132  label="H_element : 079"  # scripted group (container) (typed FeaturePython)
  n = 9
  ref = H_element
FEATURE [App::DocumentObjectGroupPython] C_element142  label="C_element : 087"  # scripted group (container) (typed FeaturePython)
  n = 9
  ref = C_element
FEATURE [App::DocumentObjectGroupPython] N_element062  label="N_element : 034"  # scripted group (container) (typed FeaturePython)
  n = 2
  ref = N_element
FEATURE [App::DocumentObjectGroupPython] O_element123  label="O_element : 076"  # scripted group (container) (typed FeaturePython)
  n = 6
  ref = O_element
FEATURE [App::DocumentObjectGroupPython] G4_DNA_URIDINE  # scripted group (container) (typed FeaturePython)
  Dunit = g/cm3
  Dvalue = 1
  Group = -> [H_element132,C_element142,N_element062,O_element123]
  conduct = 2
  density = 1
  expand = 3
  formula = G4_DNA_URIDINE
  name = G4_DNA_URIDINE
  specific = 4
FEATURE [App::DocumentObjectGroupPython] H_element133  label="H_element : 080"  # scripted group (container) (typed FeaturePython)
  n = 11
  ref = H_element
FEATURE [App::DocumentObjectGroupPython] C_element143  label="C_element : 088"  # scripted group (container) (typed FeaturePython)
  n = 10
  ref = C_element
FEATURE [App::DocumentObjectGroupPython] N_element063  label="N_element : 035"  # scripted group (container) (typed FeaturePython)
  n = 2
  ref = N_element
FEATURE [App::DocumentObjectGroupPython] O_element124  label="O_element : 077"  # scripted group (container) (typed FeaturePython)
  n = 6
  ref = O_element
FEATURE [App::DocumentObjectGroupPython] G4_DNA_METHYLURIDINE  # scripted group (container) (typed FeaturePython)
  Dunit = g/cm3
  Dvalue = 1
  Group = -> [H_element133,C_element143,N_element063,O_element124]
  conduct = 2
  density = 1
  expand = 3
  formula = G4_DNA_METHYLURIDINE
  name = G4_DNA_METHYLURIDINE
  specific = 4
FEATURE [App::DocumentObjectGroupPython] P_element014  label="P_element : 003"  # scripted group (container) (typed FeaturePython)
  n = 1
  ref = P_element
FEATURE [App::DocumentObjectGroupPython] O_element125  label="O_element : 078"  # scripted group (container) (typed FeaturePython)
  n = 3
  ref = O_element
FEATURE [App::DocumentObjectGroupPython] G4_DNA_MONOPHOSPHATE  # scripted group (container) (typed FeaturePython)
  Dunit = g/cm3
  Dvalue = 1
  Group = -> [P_element014,O_element125]
  conduct = 2
  density = 1
  expand = 3
  formula = G4_DNA_MONOPHOSPHATE
  name = G4_DNA_MONOPHOSPHATE
  specific = 4
FEATURE [App::DocumentObjectGroupPython] H_element134  label="H_element : 081"  # scripted group (container) (typed FeaturePython)
  n = 10
  ref = H_element
FEATURE [App::DocumentObjectGroupPython] C_element144  label="C_element : 089"  # scripted group (container) (typed FeaturePython)
  n = 10
  ref = C_element
FEATURE [App::DocumentObjectGroupPython] N_element064  label="N_element : 036"  # scripted group (container) (typed FeaturePython)
  n = 5
  ref = N_element
FEATURE [App::DocumentObjectGroupPython] O_element126  label="O_element : 079"  # scripted group (container) (typed FeaturePython)
  n = 7
  ref = O_element
FEATURE [App::DocumentObjectGroupPython] P_element015  label="P_element : 004"  # scripted group (container) (typed FeaturePython)
  n = 1
  ref = P_element
FEATURE [App::DocumentObjectGroupPython] G4_DNA_A  # scripted group (container) (typed FeaturePython)
  Dunit = g/cm3
  Dvalue = 1
  Group = -> [H_element134,C_element144,N_element064,O_element126,P_element015]
  conduct = 2
  density = 1
  expand = 3
  formula = G4_DNA_A
  name = G4_DNA_A
  specific = 4
FEATURE [App::DocumentObjectGroupPython] H_element135  label="H_element : 082"  # scripted group (container) (typed FeaturePython)
  n = 10
  ref = H_element
FEATURE [App::DocumentObjectGroupPython] C_element145  label="C_element : 090"  # scripted group (container) (typed FeaturePython)
  n = 10
  ref = C_element
FEATURE [App::DocumentObjectGroupPython] N_element065  label="N_element : 037"  # scripted group (container) (typed FeaturePython)
  n = 5
  ref = N_element
FEATURE [App::DocumentObjectGroupPython] O_element127  label="O_element : 8"  # scripted group (container) (typed FeaturePython)
  n = 8
  ref = O_element
FEATURE [App::DocumentObjectGroupPython] P_element016  label="P_element : 005"  # scripted group (container) (typed FeaturePython)
  n = 1
  ref = P_element
FEATURE [App::DocumentObjectGroupPython] G4_DNA_G  # scripted group (container) (typed FeaturePython)
  Dunit = g/cm3
  Dvalue = 1
  Group = -> [H_element135,C_element145,N_element065,O_element127,P_element016]
  conduct = 2
  density = 1
  expand = 3
  formula = G4_DNA_G
  name = G4_DNA_G
  specific = 4
FEATURE [App::DocumentObjectGroupPython] H_element136  label="H_element : 083"  # scripted group (container) (typed FeaturePython)
  n = 10
  ref = H_element
FEATURE [App::DocumentObjectGroupPython] C_element146  label="C_element : 091"  # scripted group (container) (typed FeaturePython)
  n = 9
  ref = C_element
FEATURE [App::DocumentObjectGroupPython] N_element066  label="N_element : 038"  # scripted group (container) (typed FeaturePython)
  n = 3
  ref = N_element
FEATURE [App::DocumentObjectGroupPython] O_element128  label="O_element : 080"  # scripted group (container) (typed FeaturePython)
  n = 8
  ref = O_element
FEATURE [App::DocumentObjectGroupPython] P_element017  label="P_element : 006"  # scripted group (container) (typed FeaturePython)
  n = 1
  ref = P_element
FEATURE [App::DocumentObjectGroupPython] G4_DNA_C  # scripted group (container) (typed FeaturePython)
  Dunit = g/cm3
  Dvalue = 1
  Group = -> [H_element136,C_element146,N_element066,O_element128,P_element017]
  conduct = 2
  density = 1
  expand = 3
  formula = G4_DNA_C
  name = G4_DNA_C
  specific = 4
FEATURE [App::DocumentObjectGroupPython] H_element137  label="H_element : 084"  # scripted group (container) (typed FeaturePython)
  n = 9
  ref = H_element
FEATURE [App::DocumentObjectGroupPython] C_element147  label="C_element : 092"  # scripted group (container) (typed FeaturePython)
  n = 9
  ref = C_element
FEATURE [App::DocumentObjectGroupPython] N_element067  label="N_element : 039"  # scripted group (container) (typed FeaturePython)
  n = 2
  ref = N_element
FEATURE [App::DocumentObjectGroupPython] O_element129  label="O_element : 9"  # scripted group (container) (typed FeaturePython)
  n = 9
  ref = O_element
FEATURE [App::DocumentObjectGroupPython] P_element018  label="P_element : 007"  # scripted group (container) (typed FeaturePython)
  n = 1
  ref = P_element
FEATURE [App::DocumentObjectGroupPython] G4_DNA_U  # scripted group (container) (typed FeaturePython)
  Dunit = g/cm3
  Dvalue = 1
  Group = -> [H_element137,C_element147,N_element067,O_element129,P_element018]
  conduct = 2
  density = 1
  expand = 3
  formula = G4_DNA_U
  name = G4_DNA_U
  specific = 4
FEATURE [App::DocumentObjectGroupPython] H_element138  label="H_element : 085"  # scripted group (container) (typed FeaturePython)
  n = 11
  ref = H_element
FEATURE [App::DocumentObjectGroupPython] C_element148  label="C_element : 093"  # scripted group (container) (typed FeaturePython)
  n = 10
  ref = C_element
FEATURE [App::DocumentObjectGroupPython] N_element068  label="N_element : 040"  # scripted group (container) (typed FeaturePython)
  n = 2
  ref = N_element
FEATURE [App::DocumentObjectGroupPython] O_element130  label="O_element : 081"  # scripted group (container) (typed FeaturePython)
  n = 9
  ref = O_element
FEATURE [App::DocumentObjectGroupPython] P_element019  label="P_element : 008"  # scripted group (container) (typed FeaturePython)
  n = 1
  ref = P_element
FEATURE [App::DocumentObjectGroupPython] G4_DNA_MU  # scripted group (container) (typed FeaturePython)
  Dunit = g/cm3
  Dvalue = 1
  Group = -> [H_element138,C_element148,N_element068,O_element130,P_element019]
  conduct = 2
  density = 1
  expand = 3
  formula = G4_DNA_MU
  name = G4_DNA_MU
  specific = 4
FEATURE [App::DocumentObjectGroupPython] BioChemical  # scripted group (container) (typed FeaturePython)
  Group = -> [G4_CYTOSINE,G4_THYMINE,G4_URACIL,G4_DNA_ADENINE,G4_DNA_GUANINE,G4_DNA_CYTOSINE,G4_DNA_THYMINE,G4_DNA_URACIL,G4_DNA_ADENOSINE,G4_DNA_GUANOSINE,G4_DNA_CYTIDINE,G4_DNA_URIDINE,G4_DNA_METHYLURIDINE,G4_DNA_MONOPHOSPHATE,G4_DNA_A,G4_DNA_G,G4_DNA_C,G4_DNA_U,G4_DNA_MU]
FEATURE [App::DocumentObjectGroupPython] G4Materials  # scripted group (container) (typed FeaturePython)
  Group = -> [NIST,Element,HEP,Space,BioChemical]
  version = 1
FEATURE [App::DocumentObjectGroupPython] Geant4  # scripted group (container) (typed FeaturePython)
  Group = -> [G4Isotopes,G4Elements,G4Materials]
FEATURE [App::DocumentObjectGroupPython] Materials  # scripted group (container) (typed FeaturePython)
  Group = -> [Geant4]
FEATURE [Part::FeaturePython] GDMLBox_WorldBox  # WARN: FeaturePython — macro-defined, semantics opaque (R4)
  lunit = 2
  material = 5
  x = 200
  y = 200
  z = 200
FEATURE [Part::FeaturePython] GDMLSphere_Sphere  # WARN: FeaturePython — macro-defined, semantics opaque (R4)
  aunit = 0
  deltaphi = 2.02
  deltatheta = 2.02
  lunit = 2
  material = 18
  rmax = 20
  rmin = 10
  startphi = 0
  starttheta = 0
FEATURE [App::Part] LV_Sphere
  Group = -> [GDMLSphere_Sphere]
  Origin = -> Origin002
  Placement = pos=(30,0,0) rot=(0,0,1;0rad)
FEATURE [Part::FeaturePython] GDMLTorus_Torus  # WARN: FeaturePython — macro-defined, semantics opaque (R4)
  aunit = deg
  deltaphi = 360
  lunit = 2
  material = 5
  rmax = 5
  rmin = 0
  rtor = 10
  startphi = 10
FEATURE [App::Part] LV_Torus
  Group = -> [GDMLTorus_Torus]
  Origin = -> Origin003
FEATURE [App::Part] Part
  Group = -> [LV_Sphere,LV_Torus]
  Origin = -> Origin001
FEATURE [Part::FeaturePython] Array  # Draft array (typed FeaturePython)
  Angle = 360
  ArrayType = 0
  Axis = (0,0,1)
  Base = -> Part
  Center = (0,0,0)
  Fuse = false
  IntervalAxis = (0,0,0)
  IntervalX = (80,0,0)
  IntervalY = (0,80,0)
  IntervalZ = (0,0,100)
  NumberCircles = 3
  NumberPolar = 5
  NumberX = 2
  NumberY = 2
  NumberZ = 1
  Placement = pos=(-49,-28,0) rot=(0,0,1;0rad)
  RadialDistance = 50
  Symmetry = 1
  TangentialDistance = 25
  material = 261
FEATURE [App::Part] Part001
  Group = -> [Part,Array]
  Origin = -> Origin004
FEATURE [App::Part] worldVOL
  Group = -> [GDMLBox_WorldBox,Part001]
  Origin = -> Origin
